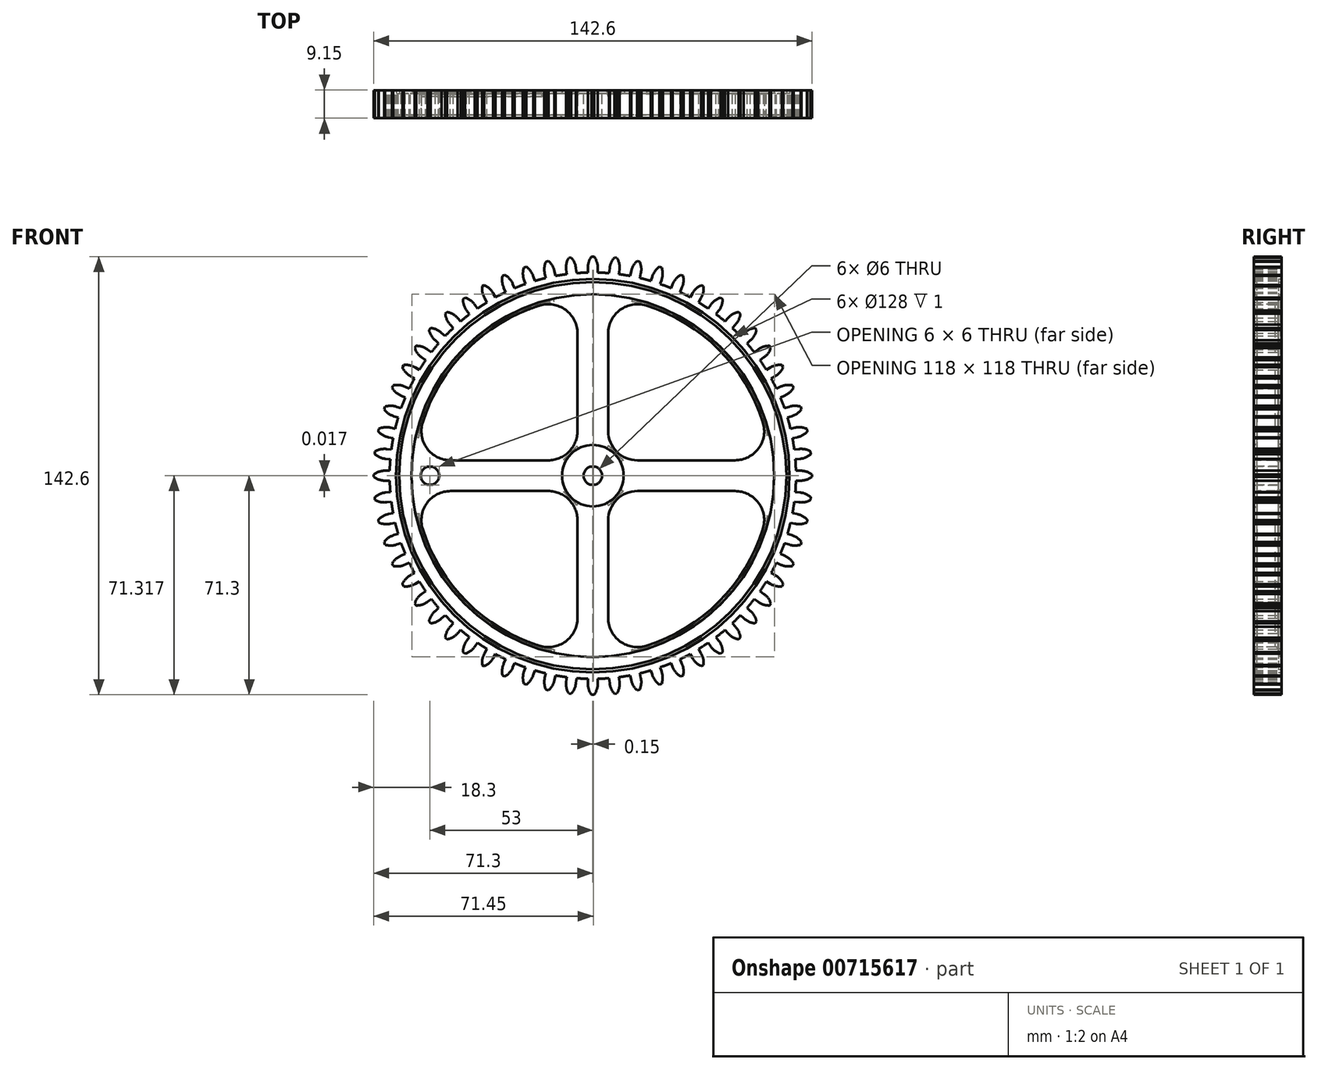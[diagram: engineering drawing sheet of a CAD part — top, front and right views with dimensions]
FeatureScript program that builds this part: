
annotation { "Feature Type Name" : "Feature", "Feature Type Description" : "" }
export const myFeature = defineFeature(function(context is Context, id is Id, definition is map)
    precondition{}
    {
        {
            var Q0;
            Q0=qCreatedBy(makeId("Front.planeOp"),FACE);
            var sketch = newSketch(context, id + "F0", { "sketchPlane" : qUnion([Q0])});
            skCircle(sketch, "E0", {"center": v(0, 0) * mm, "radius": 3 * mm});
            skCircle(sketch, "E1", {"center": v(0, 0) * mm, "radius": 66.1 * mm});
            skLineSegment(sketch, "E2", {"start": v(0, -77.77) * mm, "end": v(0, 74.62) * mm, "construction": true});
            skLineSegment(sketch, "E3", {"start": v(1.6, 66.08) * mm, "end": v(1.6, 67.83) * mm});
            skLineSegment(sketch, "E4", {"start": v(-1.6, 67.83) * mm, "end": v(-1.6, 66.08) * mm});
            skArc(sketch, "E5", {"start": v(-0.4, 71.3) * mm, "mid": v(-1.31, 69.54) * mm, "end": v(-1.6, 67.58) * mm});
            skArc(sketch, "E6.trimOffspring", {"start": v(1.6, 67.58) * mm, "mid": v(1.31, 69.54) * mm, "end": v(0.4, 71.3) * mm});
            skLineSegment(sketch, "E7", {"start": v(-0.4, 71.3) * mm, "end": v(0.4, 71.3) * mm});
            skLineSegment(sketch, "E8.1.0", {"start": v(-7.86, 70.87) * mm, "end": v(-7.05, 70.95) * mm});
            skArc(sketch, "E8.1.1", {"start": v(-5.47, 67.38) * mm, "mid": v(-5.96, 69.3) * mm, "end": v(-7.05, 70.95) * mm});
            skArc(sketch, "E8.1.2", {"start": v(-7.86, 70.87) * mm, "mid": v(-8.58, 69.02) * mm, "end": v(-8.66, 67.05) * mm});
            skLineSegment(sketch, "E8.1.3", {"start": v(-8.68, 67.3) * mm, "end": v(-8.5, 65.55) * mm});
            skLineSegment(sketch, "E8.1.4", {"start": v(-5.32, 65.89) * mm, "end": v(-5.5, 67.63) * mm});
            skLineSegment(sketch, "E8.2.0", {"start": v(-15.22, 69.66) * mm, "end": v(-14.43, 69.83) * mm});
            skArc(sketch, "E8.2.1", {"start": v(-12.49, 66.44) * mm, "mid": v(-13.17, 68.3) * mm, "end": v(-14.43, 69.83) * mm});
            skArc(sketch, "E8.2.2", {"start": v(-15.22, 69.66) * mm, "mid": v(-15.74, 67.75) * mm, "end": v(-15.62, 65.77) * mm});
            skLineSegment(sketch, "E8.2.3", {"start": v(-15.67, 66.02) * mm, "end": v(-15.3, 64.3) * mm});
            skLineSegment(sketch, "E8.2.4", {"start": v(-12.17, 64.97) * mm, "end": v(-12.54, 66.68) * mm});
            skLineSegment(sketch, "E9.1.3.0", {"start": v(-22.42, 67.68) * mm, "end": v(-21.64, 67.94) * mm});
            skArc(sketch, "E9.3.3.0", {"start": v(-19.36, 64.77) * mm, "mid": v(-20.24, 66.54) * mm, "end": v(-21.64, 67.94) * mm});
            skArc(sketch, "E9.7.3.0", {"start": v(-22.42, 67.68) * mm, "mid": v(-22.74, 65.73) * mm, "end": v(-22.4, 63.78) * mm});
            skLineSegment(sketch, "E9.11.3.0", {"start": v(-22.48, 64.02) * mm, "end": v(-21.94, 62.35) * mm});
            skLineSegment(sketch, "E9.14.3.0", {"start": v(-18.9, 63.34) * mm, "end": v(-19.44, 65) * mm});
            skLineSegment(sketch, "E9.1.4.0", {"start": v(-29.37, 64.97) * mm, "end": v(-28.63, 65.3) * mm});
            skArc(sketch, "E9.3.4.0", {"start": v(-26.03, 62.4) * mm, "mid": v(-27.08, 64.06) * mm, "end": v(-28.63, 65.3) * mm});
            skArc(sketch, "E9.7.4.0", {"start": v(-29.37, 64.97) * mm, "mid": v(-29.49, 63) * mm, "end": v(-28.95, 61.09) * mm});
            skLineSegment(sketch, "E9.11.4.0", {"start": v(-29.05, 61.32) * mm, "end": v(-28.34, 59.72) * mm});
            skLineSegment(sketch, "E9.14.4.0", {"start": v(-25.42, 61.02) * mm, "end": v(-26.13, 62.62) * mm});
            skLineSegment(sketch, "E9.1.5.0", {"start": v(-36, 61.54) * mm, "end": v(-35.3, 61.95) * mm});
            skArc(sketch, "E9.3.5.0", {"start": v(-32.4, 59.33) * mm, "mid": v(-33.63, 60.88) * mm, "end": v(-35.3, 61.95) * mm});
            skArc(sketch, "E9.7.5.0", {"start": v(-36, 61.54) * mm, "mid": v(-35.9, 59.57) * mm, "end": v(-35.18, 57.73) * mm});
            skLineSegment(sketch, "E9.11.5.0", {"start": v(-35.3, 57.94) * mm, "end": v(-34.43, 56.43) * mm});
            skLineSegment(sketch, "E9.14.5.0", {"start": v(-31.65, 58.03) * mm, "end": v(-32.53, 59.54) * mm});
            skLineSegment(sketch, "E9.1.6.0", {"start": v(-42.24, 57.44) * mm, "end": v(-41.58, 57.92) * mm});
            skArc(sketch, "E9.3.6.0", {"start": v(-38.43, 55.62) * mm, "mid": v(-39.81, 57.03) * mm, "end": v(-41.58, 57.92) * mm});
            skArc(sketch, "E9.7.6.0", {"start": v(-42.24, 57.44) * mm, "mid": v(-41.94, 55.49) * mm, "end": v(-41.02, 53.74) * mm});
            skLineSegment(sketch, "E9.11.6.0", {"start": v(-41.16, 53.94) * mm, "end": v(-40.14, 52.52) * mm});
            skLineSegment(sketch, "E9.14.6.0", {"start": v(-37.55, 54.4) * mm, "end": v(-38.58, 55.82) * mm});
            skLineSegment(sketch, "E9.1.7.0", {"start": v(-48.01, 52.71) * mm, "end": v(-47.4, 53.26) * mm});
            skArc(sketch, "E9.3.7.0", {"start": v(-44.03, 51.3) * mm, "mid": v(-45.56, 52.56) * mm, "end": v(-47.4, 53.26) * mm});
            skArc(sketch, "E9.7.7.0", {"start": v(-48.01, 52.71) * mm, "mid": v(-47.5, 50.8) * mm, "end": v(-46.41, 49.15) * mm});
            skLineSegment(sketch, "E9.11.7.0", {"start": v(-46.58, 49.34) * mm, "end": v(-45.4, 48.04) * mm});
            skLineSegment(sketch, "E9.14.7.0", {"start": v(-43.03, 50.18) * mm, "end": v(-44.2, 51.48) * mm});
            skLineSegment(sketch, "E9.1.8.0", {"start": v(-53.26, 47.4) * mm, "end": v(-52.71, 48.01) * mm});
            skArc(sketch, "E9.3.8.0", {"start": v(-49.15, 46.41) * mm, "mid": v(-50.8, 47.5) * mm, "end": v(-52.71, 48.01) * mm});
            skArc(sketch, "E9.7.8.0", {"start": v(-53.26, 47.4) * mm, "mid": v(-52.56, 45.56) * mm, "end": v(-51.3, 44.03) * mm});
            skLineSegment(sketch, "E9.11.8.0", {"start": v(-51.48, 44.2) * mm, "end": v(-50.18, 43.03) * mm});
            skLineSegment(sketch, "E9.14.8.0", {"start": v(-48.04, 45.4) * mm, "end": v(-49.34, 46.58) * mm});
            skLineSegment(sketch, "E9.1.9.0", {"start": v(-57.92, 41.58) * mm, "end": v(-57.44, 42.24) * mm});
            skArc(sketch, "E9.3.9.0", {"start": v(-53.74, 41.02) * mm, "mid": v(-55.49, 41.94) * mm, "end": v(-57.44, 42.24) * mm});
            skArc(sketch, "E9.7.9.0", {"start": v(-57.92, 41.58) * mm, "mid": v(-57.03, 39.81) * mm, "end": v(-55.62, 38.43) * mm});
            skLineSegment(sketch, "E9.11.9.0", {"start": v(-55.82, 38.58) * mm, "end": v(-54.4, 37.55) * mm});
            skLineSegment(sketch, "E9.14.9.0", {"start": v(-52.52, 40.14) * mm, "end": v(-53.94, 41.16) * mm});
            skLineSegment(sketch, "E9.1.10.0", {"start": v(-61.95, 35.3) * mm, "end": v(-61.54, 36) * mm});
            skArc(sketch, "E9.3.10.0", {"start": v(-57.73, 35.18) * mm, "mid": v(-59.57, 35.9) * mm, "end": v(-61.54, 36) * mm});
            skArc(sketch, "E9.7.10.0", {"start": v(-61.95, 35.3) * mm, "mid": v(-60.88, 33.63) * mm, "end": v(-59.33, 32.4) * mm});
            skLineSegment(sketch, "E9.11.10.0", {"start": v(-59.54, 32.53) * mm, "end": v(-58.03, 31.65) * mm});
            skLineSegment(sketch, "E9.14.10.0", {"start": v(-56.43, 34.43) * mm, "end": v(-57.94, 35.3) * mm});
            skLineSegment(sketch, "E9.1.11.0", {"start": v(-65.3, 28.63) * mm, "end": v(-64.97, 29.37) * mm});
            skArc(sketch, "E9.3.11.0", {"start": v(-61.09, 28.95) * mm, "mid": v(-63, 29.49) * mm, "end": v(-64.97, 29.37) * mm});
            skArc(sketch, "E9.7.11.0", {"start": v(-65.3, 28.63) * mm, "mid": v(-64.06, 27.08) * mm, "end": v(-62.4, 26.03) * mm});
            skLineSegment(sketch, "E9.11.11.0", {"start": v(-62.62, 26.13) * mm, "end": v(-61.02, 25.42) * mm});
            skLineSegment(sketch, "E9.14.11.0", {"start": v(-59.72, 28.34) * mm, "end": v(-61.32, 29.05) * mm});
            skLineSegment(sketch, "E9.1.12.0", {"start": v(-67.94, 21.64) * mm, "end": v(-67.68, 22.42) * mm});
            skArc(sketch, "E9.3.12.0", {"start": v(-63.78, 22.4) * mm, "mid": v(-65.73, 22.74) * mm, "end": v(-67.68, 22.42) * mm});
            skArc(sketch, "E9.7.12.0", {"start": v(-67.94, 21.64) * mm, "mid": v(-66.54, 20.24) * mm, "end": v(-64.77, 19.36) * mm});
            skLineSegment(sketch, "E9.11.12.0", {"start": v(-65, 19.44) * mm, "end": v(-63.34, 18.9) * mm});
            skLineSegment(sketch, "E9.14.12.0", {"start": v(-62.35, 21.94) * mm, "end": v(-64.02, 22.48) * mm});
            skLineSegment(sketch, "E9.1.13.0", {"start": v(-69.83, 14.43) * mm, "end": v(-69.66, 15.22) * mm});
            skArc(sketch, "E9.3.13.0", {"start": v(-65.77, 15.62) * mm, "mid": v(-67.75, 15.74) * mm, "end": v(-69.66, 15.22) * mm});
            skArc(sketch, "E9.7.13.0", {"start": v(-69.83, 14.43) * mm, "mid": v(-68.3, 13.17) * mm, "end": v(-66.44, 12.49) * mm});
            skLineSegment(sketch, "E9.11.13.0", {"start": v(-66.68, 12.54) * mm, "end": v(-64.97, 12.17) * mm});
            skLineSegment(sketch, "E9.14.13.0", {"start": v(-64.3, 15.3) * mm, "end": v(-66.02, 15.67) * mm});
            skLineSegment(sketch, "E9.1.14.0", {"start": v(-70.95, 7.05) * mm, "end": v(-70.87, 7.86) * mm});
            skArc(sketch, "E9.3.14.0", {"start": v(-67.05, 8.66) * mm, "mid": v(-69.02, 8.58) * mm, "end": v(-70.87, 7.86) * mm});
            skArc(sketch, "E9.7.14.0", {"start": v(-70.95, 7.05) * mm, "mid": v(-69.3, 5.96) * mm, "end": v(-67.38, 5.47) * mm});
            skLineSegment(sketch, "E9.11.14.0", {"start": v(-67.63, 5.5) * mm, "end": v(-65.89, 5.32) * mm});
            skLineSegment(sketch, "E9.14.14.0", {"start": v(-65.55, 8.5) * mm, "end": v(-67.3, 8.68) * mm});
            skLineSegment(sketch, "E9.1.15.0", {"start": v(-71.3, -0.4) * mm, "end": v(-71.3, 0.4) * mm});
            skArc(sketch, "E9.3.15.0", {"start": v(-67.58, 1.6) * mm, "mid": v(-69.54, 1.31) * mm, "end": v(-71.3, 0.4) * mm});
            skArc(sketch, "E9.7.15.0", {"start": v(-71.3, -0.4) * mm, "mid": v(-69.54, -1.31) * mm, "end": v(-67.58, -1.6) * mm});
            skLineSegment(sketch, "E9.11.15.0", {"start": v(-67.83, -1.6) * mm, "end": v(-66.08, -1.6) * mm});
            skLineSegment(sketch, "E9.14.15.0", {"start": v(-66.08, 1.6) * mm, "end": v(-67.83, 1.6) * mm});
            skLineSegment(sketch, "E9.1.16.0", {"start": v(-70.87, -7.86) * mm, "end": v(-70.95, -7.05) * mm});
            skArc(sketch, "E9.3.16.0", {"start": v(-67.38, -5.47) * mm, "mid": v(-69.3, -5.96) * mm, "end": v(-70.95, -7.05) * mm});
            skArc(sketch, "E9.7.16.0", {"start": v(-70.87, -7.86) * mm, "mid": v(-69.02, -8.58) * mm, "end": v(-67.05, -8.66) * mm});
            skLineSegment(sketch, "E9.11.16.0", {"start": v(-67.3, -8.68) * mm, "end": v(-65.55, -8.5) * mm});
            skLineSegment(sketch, "E9.14.16.0", {"start": v(-65.89, -5.32) * mm, "end": v(-67.63, -5.5) * mm});
            skLineSegment(sketch, "E9.1.17.0", {"start": v(-69.66, -15.22) * mm, "end": v(-69.83, -14.43) * mm});
            skArc(sketch, "E9.3.17.0", {"start": v(-66.44, -12.49) * mm, "mid": v(-68.3, -13.17) * mm, "end": v(-69.83, -14.43) * mm});
            skArc(sketch, "E9.7.17.0", {"start": v(-69.66, -15.22) * mm, "mid": v(-67.75, -15.74) * mm, "end": v(-65.77, -15.62) * mm});
            skLineSegment(sketch, "E9.11.17.0", {"start": v(-66.02, -15.67) * mm, "end": v(-64.3, -15.3) * mm});
            skLineSegment(sketch, "E9.14.17.0", {"start": v(-64.97, -12.17) * mm, "end": v(-66.68, -12.54) * mm});
            skLineSegment(sketch, "E9.1.18.0", {"start": v(-67.68, -22.42) * mm, "end": v(-67.94, -21.64) * mm});
            skArc(sketch, "E9.3.18.0", {"start": v(-64.77, -19.36) * mm, "mid": v(-66.54, -20.24) * mm, "end": v(-67.94, -21.64) * mm});
            skArc(sketch, "E9.7.18.0", {"start": v(-67.68, -22.42) * mm, "mid": v(-65.73, -22.74) * mm, "end": v(-63.78, -22.4) * mm});
            skLineSegment(sketch, "E9.11.18.0", {"start": v(-64.02, -22.48) * mm, "end": v(-62.35, -21.94) * mm});
            skLineSegment(sketch, "E9.14.18.0", {"start": v(-63.34, -18.9) * mm, "end": v(-65, -19.44) * mm});
            skLineSegment(sketch, "E9.1.19.0", {"start": v(-64.97, -29.37) * mm, "end": v(-65.3, -28.63) * mm});
            skArc(sketch, "E9.3.19.0", {"start": v(-62.4, -26.03) * mm, "mid": v(-64.06, -27.08) * mm, "end": v(-65.3, -28.63) * mm});
            skArc(sketch, "E9.7.19.0", {"start": v(-64.97, -29.37) * mm, "mid": v(-63, -29.49) * mm, "end": v(-61.09, -28.95) * mm});
            skLineSegment(sketch, "E9.11.19.0", {"start": v(-61.32, -29.05) * mm, "end": v(-59.72, -28.34) * mm});
            skLineSegment(sketch, "E9.14.19.0", {"start": v(-61.02, -25.42) * mm, "end": v(-62.62, -26.13) * mm});
            skLineSegment(sketch, "E9.1.20.0", {"start": v(-61.54, -36) * mm, "end": v(-61.95, -35.3) * mm});
            skArc(sketch, "E9.3.20.0", {"start": v(-59.33, -32.4) * mm, "mid": v(-60.88, -33.63) * mm, "end": v(-61.95, -35.3) * mm});
            skArc(sketch, "E9.7.20.0", {"start": v(-61.54, -36) * mm, "mid": v(-59.57, -35.9) * mm, "end": v(-57.73, -35.18) * mm});
            skLineSegment(sketch, "E9.11.20.0", {"start": v(-57.94, -35.3) * mm, "end": v(-56.43, -34.43) * mm});
            skLineSegment(sketch, "E9.14.20.0", {"start": v(-58.03, -31.65) * mm, "end": v(-59.54, -32.53) * mm});
            skLineSegment(sketch, "E9.1.21.0", {"start": v(-57.44, -42.24) * mm, "end": v(-57.92, -41.58) * mm});
            skArc(sketch, "E9.3.21.0", {"start": v(-55.62, -38.43) * mm, "mid": v(-57.03, -39.81) * mm, "end": v(-57.92, -41.58) * mm});
            skArc(sketch, "E9.7.21.0", {"start": v(-57.44, -42.24) * mm, "mid": v(-55.49, -41.94) * mm, "end": v(-53.74, -41.02) * mm});
            skLineSegment(sketch, "E9.11.21.0", {"start": v(-53.94, -41.16) * mm, "end": v(-52.52, -40.14) * mm});
            skLineSegment(sketch, "E9.14.21.0", {"start": v(-54.4, -37.55) * mm, "end": v(-55.82, -38.58) * mm});
            skLineSegment(sketch, "E9.1.22.0", {"start": v(-52.71, -48.01) * mm, "end": v(-53.26, -47.4) * mm});
            skArc(sketch, "E9.3.22.0", {"start": v(-51.3, -44.03) * mm, "mid": v(-52.56, -45.56) * mm, "end": v(-53.26, -47.4) * mm});
            skArc(sketch, "E9.7.22.0", {"start": v(-52.71, -48.01) * mm, "mid": v(-50.8, -47.5) * mm, "end": v(-49.15, -46.41) * mm});
            skLineSegment(sketch, "E9.11.22.0", {"start": v(-49.34, -46.58) * mm, "end": v(-48.04, -45.4) * mm});
            skLineSegment(sketch, "E9.14.22.0", {"start": v(-50.18, -43.03) * mm, "end": v(-51.48, -44.2) * mm});
            skLineSegment(sketch, "E9.1.23.0", {"start": v(-47.4, -53.26) * mm, "end": v(-48.01, -52.71) * mm});
            skArc(sketch, "E9.3.23.0", {"start": v(-46.41, -49.15) * mm, "mid": v(-47.5, -50.8) * mm, "end": v(-48.01, -52.71) * mm});
            skArc(sketch, "E9.7.23.0", {"start": v(-47.4, -53.26) * mm, "mid": v(-45.56, -52.56) * mm, "end": v(-44.03, -51.3) * mm});
            skLineSegment(sketch, "E9.11.23.0", {"start": v(-44.2, -51.48) * mm, "end": v(-43.03, -50.18) * mm});
            skLineSegment(sketch, "E9.14.23.0", {"start": v(-45.4, -48.04) * mm, "end": v(-46.58, -49.34) * mm});
            skLineSegment(sketch, "E9.1.24.0", {"start": v(-41.58, -57.92) * mm, "end": v(-42.24, -57.44) * mm});
            skArc(sketch, "E9.3.24.0", {"start": v(-41.02, -53.74) * mm, "mid": v(-41.94, -55.49) * mm, "end": v(-42.24, -57.44) * mm});
            skArc(sketch, "E9.7.24.0", {"start": v(-41.58, -57.92) * mm, "mid": v(-39.81, -57.03) * mm, "end": v(-38.43, -55.62) * mm});
            skLineSegment(sketch, "E9.11.24.0", {"start": v(-38.58, -55.82) * mm, "end": v(-37.55, -54.4) * mm});
            skLineSegment(sketch, "E9.14.24.0", {"start": v(-40.14, -52.52) * mm, "end": v(-41.16, -53.94) * mm});
            skLineSegment(sketch, "E9.1.25.0", {"start": v(-35.3, -61.95) * mm, "end": v(-36, -61.54) * mm});
            skArc(sketch, "E9.3.25.0", {"start": v(-35.18, -57.73) * mm, "mid": v(-35.9, -59.57) * mm, "end": v(-36, -61.54) * mm});
            skArc(sketch, "E9.7.25.0", {"start": v(-35.3, -61.95) * mm, "mid": v(-33.63, -60.88) * mm, "end": v(-32.4, -59.33) * mm});
            skLineSegment(sketch, "E9.11.25.0", {"start": v(-32.53, -59.54) * mm, "end": v(-31.65, -58.03) * mm});
            skLineSegment(sketch, "E9.14.25.0", {"start": v(-34.43, -56.43) * mm, "end": v(-35.3, -57.94) * mm});
            skLineSegment(sketch, "E9.1.26.0", {"start": v(-28.63, -65.3) * mm, "end": v(-29.37, -64.97) * mm});
            skArc(sketch, "E9.3.26.0", {"start": v(-28.95, -61.09) * mm, "mid": v(-29.49, -63) * mm, "end": v(-29.37, -64.97) * mm});
            skArc(sketch, "E9.7.26.0", {"start": v(-28.63, -65.3) * mm, "mid": v(-27.08, -64.06) * mm, "end": v(-26.03, -62.4) * mm});
            skLineSegment(sketch, "E9.11.26.0", {"start": v(-26.13, -62.62) * mm, "end": v(-25.42, -61.02) * mm});
            skLineSegment(sketch, "E9.14.26.0", {"start": v(-28.34, -59.72) * mm, "end": v(-29.05, -61.32) * mm});
            skLineSegment(sketch, "E9.1.27.0", {"start": v(-21.64, -67.94) * mm, "end": v(-22.42, -67.68) * mm});
            skArc(sketch, "E9.3.27.0", {"start": v(-22.4, -63.78) * mm, "mid": v(-22.74, -65.73) * mm, "end": v(-22.42, -67.68) * mm});
            skArc(sketch, "E9.7.27.0", {"start": v(-21.64, -67.94) * mm, "mid": v(-20.24, -66.54) * mm, "end": v(-19.36, -64.77) * mm});
            skLineSegment(sketch, "E9.11.27.0", {"start": v(-19.44, -65) * mm, "end": v(-18.9, -63.34) * mm});
            skLineSegment(sketch, "E9.14.27.0", {"start": v(-21.94, -62.35) * mm, "end": v(-22.48, -64.02) * mm});
            skLineSegment(sketch, "E9.1.28.0", {"start": v(-14.43, -69.83) * mm, "end": v(-15.22, -69.66) * mm});
            skArc(sketch, "E9.3.28.0", {"start": v(-15.62, -65.77) * mm, "mid": v(-15.74, -67.75) * mm, "end": v(-15.22, -69.66) * mm});
            skArc(sketch, "E9.7.28.0", {"start": v(-14.43, -69.83) * mm, "mid": v(-13.17, -68.3) * mm, "end": v(-12.49, -66.44) * mm});
            skLineSegment(sketch, "E9.11.28.0", {"start": v(-12.54, -66.68) * mm, "end": v(-12.17, -64.97) * mm});
            skLineSegment(sketch, "E9.14.28.0", {"start": v(-15.3, -64.3) * mm, "end": v(-15.67, -66.02) * mm});
            skLineSegment(sketch, "E9.1.29.0", {"start": v(-7.05, -70.95) * mm, "end": v(-7.86, -70.87) * mm});
            skArc(sketch, "E9.3.29.0", {"start": v(-8.66, -67.05) * mm, "mid": v(-8.58, -69.02) * mm, "end": v(-7.86, -70.87) * mm});
            skArc(sketch, "E9.7.29.0", {"start": v(-7.05, -70.95) * mm, "mid": v(-5.96, -69.3) * mm, "end": v(-5.47, -67.38) * mm});
            skLineSegment(sketch, "E9.11.29.0", {"start": v(-5.5, -67.63) * mm, "end": v(-5.32, -65.89) * mm});
            skLineSegment(sketch, "E9.14.29.0", {"start": v(-8.5, -65.55) * mm, "end": v(-8.68, -67.3) * mm});
            skLineSegment(sketch, "E9.1.30.0", {"start": v(0.4, -71.3) * mm, "end": v(-0.4, -71.3) * mm});
            skArc(sketch, "E9.3.30.0", {"start": v(-1.6, -67.58) * mm, "mid": v(-1.31, -69.54) * mm, "end": v(-0.4, -71.3) * mm});
            skArc(sketch, "E9.7.30.0", {"start": v(0.4, -71.3) * mm, "mid": v(1.31, -69.54) * mm, "end": v(1.6, -67.58) * mm});
            skLineSegment(sketch, "E9.11.30.0", {"start": v(1.6, -67.83) * mm, "end": v(1.6, -66.08) * mm});
            skLineSegment(sketch, "E9.14.30.0", {"start": v(-1.6, -66.08) * mm, "end": v(-1.6, -67.83) * mm});
            skLineSegment(sketch, "E9.1.31.0", {"start": v(7.86, -70.87) * mm, "end": v(7.05, -70.95) * mm});
            skArc(sketch, "E9.3.31.0", {"start": v(5.47, -67.38) * mm, "mid": v(5.96, -69.3) * mm, "end": v(7.05, -70.95) * mm});
            skArc(sketch, "E9.7.31.0", {"start": v(7.86, -70.87) * mm, "mid": v(8.58, -69.02) * mm, "end": v(8.66, -67.05) * mm});
            skLineSegment(sketch, "E9.11.31.0", {"start": v(8.68, -67.3) * mm, "end": v(8.5, -65.55) * mm});
            skLineSegment(sketch, "E9.14.31.0", {"start": v(5.32, -65.89) * mm, "end": v(5.5, -67.63) * mm});
            skLineSegment(sketch, "E9.1.32.0", {"start": v(15.22, -69.66) * mm, "end": v(14.43, -69.83) * mm});
            skArc(sketch, "E9.3.32.0", {"start": v(12.49, -66.44) * mm, "mid": v(13.17, -68.3) * mm, "end": v(14.43, -69.83) * mm});
            skArc(sketch, "E9.7.32.0", {"start": v(15.22, -69.66) * mm, "mid": v(15.74, -67.75) * mm, "end": v(15.62, -65.77) * mm});
            skLineSegment(sketch, "E9.11.32.0", {"start": v(15.67, -66.02) * mm, "end": v(15.3, -64.3) * mm});
            skLineSegment(sketch, "E9.14.32.0", {"start": v(12.17, -64.97) * mm, "end": v(12.54, -66.68) * mm});
            skLineSegment(sketch, "E9.1.33.0", {"start": v(22.42, -67.68) * mm, "end": v(21.64, -67.94) * mm});
            skArc(sketch, "E9.3.33.0", {"start": v(19.36, -64.77) * mm, "mid": v(20.24, -66.54) * mm, "end": v(21.64, -67.94) * mm});
            skArc(sketch, "E9.7.33.0", {"start": v(22.42, -67.68) * mm, "mid": v(22.74, -65.73) * mm, "end": v(22.4, -63.78) * mm});
            skLineSegment(sketch, "E9.11.33.0", {"start": v(22.48, -64.02) * mm, "end": v(21.94, -62.35) * mm});
            skLineSegment(sketch, "E9.14.33.0", {"start": v(18.9, -63.34) * mm, "end": v(19.44, -65) * mm});
            skLineSegment(sketch, "E9.1.34.0", {"start": v(29.37, -64.97) * mm, "end": v(28.63, -65.3) * mm});
            skArc(sketch, "E9.3.34.0", {"start": v(26.03, -62.4) * mm, "mid": v(27.08, -64.06) * mm, "end": v(28.63, -65.3) * mm});
            skArc(sketch, "E9.7.34.0", {"start": v(29.37, -64.97) * mm, "mid": v(29.49, -63) * mm, "end": v(28.95, -61.09) * mm});
            skLineSegment(sketch, "E9.11.34.0", {"start": v(29.05, -61.32) * mm, "end": v(28.34, -59.72) * mm});
            skLineSegment(sketch, "E9.14.34.0", {"start": v(25.42, -61.02) * mm, "end": v(26.13, -62.62) * mm});
            skLineSegment(sketch, "E9.1.35.0", {"start": v(36, -61.54) * mm, "end": v(35.3, -61.95) * mm});
            skArc(sketch, "E9.3.35.0", {"start": v(32.4, -59.33) * mm, "mid": v(33.63, -60.88) * mm, "end": v(35.3, -61.95) * mm});
            skArc(sketch, "E9.7.35.0", {"start": v(36, -61.54) * mm, "mid": v(35.9, -59.57) * mm, "end": v(35.18, -57.73) * mm});
            skLineSegment(sketch, "E9.11.35.0", {"start": v(35.3, -57.94) * mm, "end": v(34.43, -56.43) * mm});
            skLineSegment(sketch, "E9.14.35.0", {"start": v(31.65, -58.03) * mm, "end": v(32.53, -59.54) * mm});
            skLineSegment(sketch, "E9.1.36.0", {"start": v(42.24, -57.44) * mm, "end": v(41.58, -57.92) * mm});
            skArc(sketch, "E9.3.36.0", {"start": v(38.43, -55.62) * mm, "mid": v(39.81, -57.03) * mm, "end": v(41.58, -57.92) * mm});
            skArc(sketch, "E9.7.36.0", {"start": v(42.24, -57.44) * mm, "mid": v(41.94, -55.49) * mm, "end": v(41.02, -53.74) * mm});
            skLineSegment(sketch, "E9.11.36.0", {"start": v(41.16, -53.94) * mm, "end": v(40.14, -52.52) * mm});
            skLineSegment(sketch, "E9.14.36.0", {"start": v(37.55, -54.4) * mm, "end": v(38.58, -55.82) * mm});
            skLineSegment(sketch, "E9.1.37.0", {"start": v(48.01, -52.71) * mm, "end": v(47.4, -53.26) * mm});
            skArc(sketch, "E9.3.37.0", {"start": v(44.03, -51.3) * mm, "mid": v(45.56, -52.56) * mm, "end": v(47.4, -53.26) * mm});
            skArc(sketch, "E9.7.37.0", {"start": v(48.01, -52.71) * mm, "mid": v(47.5, -50.8) * mm, "end": v(46.41, -49.15) * mm});
            skLineSegment(sketch, "E9.11.37.0", {"start": v(46.58, -49.34) * mm, "end": v(45.4, -48.04) * mm});
            skLineSegment(sketch, "E9.14.37.0", {"start": v(43.03, -50.18) * mm, "end": v(44.2, -51.48) * mm});
            skLineSegment(sketch, "E9.1.38.0", {"start": v(53.26, -47.4) * mm, "end": v(52.71, -48.01) * mm});
            skArc(sketch, "E9.3.38.0", {"start": v(49.15, -46.41) * mm, "mid": v(50.8, -47.5) * mm, "end": v(52.71, -48.01) * mm});
            skArc(sketch, "E9.7.38.0", {"start": v(53.26, -47.4) * mm, "mid": v(52.56, -45.56) * mm, "end": v(51.3, -44.03) * mm});
            skLineSegment(sketch, "E9.11.38.0", {"start": v(51.48, -44.2) * mm, "end": v(50.18, -43.03) * mm});
            skLineSegment(sketch, "E9.14.38.0", {"start": v(48.04, -45.4) * mm, "end": v(49.34, -46.58) * mm});
            skLineSegment(sketch, "E9.1.39.0", {"start": v(57.92, -41.58) * mm, "end": v(57.44, -42.24) * mm});
            skArc(sketch, "E9.3.39.0", {"start": v(53.74, -41.02) * mm, "mid": v(55.49, -41.94) * mm, "end": v(57.44, -42.24) * mm});
            skArc(sketch, "E9.7.39.0", {"start": v(57.92, -41.58) * mm, "mid": v(57.03, -39.81) * mm, "end": v(55.62, -38.43) * mm});
            skLineSegment(sketch, "E9.11.39.0", {"start": v(55.82, -38.58) * mm, "end": v(54.4, -37.55) * mm});
            skLineSegment(sketch, "E9.14.39.0", {"start": v(52.52, -40.14) * mm, "end": v(53.94, -41.16) * mm});
            skLineSegment(sketch, "E9.1.40.0", {"start": v(61.95, -35.3) * mm, "end": v(61.54, -36) * mm});
            skArc(sketch, "E9.3.40.0", {"start": v(57.73, -35.18) * mm, "mid": v(59.57, -35.9) * mm, "end": v(61.54, -36) * mm});
            skArc(sketch, "E9.7.40.0", {"start": v(61.95, -35.3) * mm, "mid": v(60.88, -33.63) * mm, "end": v(59.33, -32.4) * mm});
            skLineSegment(sketch, "E9.11.40.0", {"start": v(59.54, -32.53) * mm, "end": v(58.03, -31.65) * mm});
            skLineSegment(sketch, "E9.14.40.0", {"start": v(56.43, -34.43) * mm, "end": v(57.94, -35.3) * mm});
            skLineSegment(sketch, "E9.1.41.0", {"start": v(65.3, -28.63) * mm, "end": v(64.97, -29.37) * mm});
            skArc(sketch, "E9.3.41.0", {"start": v(61.09, -28.95) * mm, "mid": v(63, -29.49) * mm, "end": v(64.97, -29.37) * mm});
            skArc(sketch, "E9.7.41.0", {"start": v(65.3, -28.63) * mm, "mid": v(64.06, -27.08) * mm, "end": v(62.4, -26.03) * mm});
            skLineSegment(sketch, "E9.11.41.0", {"start": v(62.62, -26.13) * mm, "end": v(61.02, -25.42) * mm});
            skLineSegment(sketch, "E9.14.41.0", {"start": v(59.72, -28.34) * mm, "end": v(61.32, -29.05) * mm});
            skLineSegment(sketch, "E9.1.42.0", {"start": v(67.94, -21.64) * mm, "end": v(67.68, -22.42) * mm});
            skArc(sketch, "E9.3.42.0", {"start": v(63.78, -22.4) * mm, "mid": v(65.73, -22.74) * mm, "end": v(67.68, -22.42) * mm});
            skArc(sketch, "E9.7.42.0", {"start": v(67.94, -21.64) * mm, "mid": v(66.54, -20.24) * mm, "end": v(64.77, -19.36) * mm});
            skLineSegment(sketch, "E9.11.42.0", {"start": v(65, -19.44) * mm, "end": v(63.34, -18.9) * mm});
            skLineSegment(sketch, "E9.14.42.0", {"start": v(62.35, -21.94) * mm, "end": v(64.02, -22.48) * mm});
            skLineSegment(sketch, "E9.1.43.0", {"start": v(69.83, -14.43) * mm, "end": v(69.66, -15.22) * mm});
            skArc(sketch, "E9.3.43.0", {"start": v(65.77, -15.62) * mm, "mid": v(67.75, -15.74) * mm, "end": v(69.66, -15.22) * mm});
            skArc(sketch, "E9.7.43.0", {"start": v(69.83, -14.43) * mm, "mid": v(68.3, -13.17) * mm, "end": v(66.44, -12.49) * mm});
            skLineSegment(sketch, "E9.11.43.0", {"start": v(66.68, -12.54) * mm, "end": v(64.97, -12.17) * mm});
            skLineSegment(sketch, "E9.14.43.0", {"start": v(64.3, -15.3) * mm, "end": v(66.02, -15.67) * mm});
            skLineSegment(sketch, "E9.1.44.0", {"start": v(70.95, -7.05) * mm, "end": v(70.87, -7.86) * mm});
            skArc(sketch, "E9.3.44.0", {"start": v(67.05, -8.66) * mm, "mid": v(69.02, -8.58) * mm, "end": v(70.87, -7.86) * mm});
            skArc(sketch, "E9.7.44.0", {"start": v(70.95, -7.05) * mm, "mid": v(69.3, -5.96) * mm, "end": v(67.38, -5.47) * mm});
            skLineSegment(sketch, "E9.11.44.0", {"start": v(67.63, -5.5) * mm, "end": v(65.89, -5.32) * mm});
            skLineSegment(sketch, "E9.14.44.0", {"start": v(65.55, -8.5) * mm, "end": v(67.3, -8.68) * mm});
            skLineSegment(sketch, "E9.1.45.0", {"start": v(71.3, 0.4) * mm, "end": v(71.3, -0.4) * mm});
            skArc(sketch, "E9.3.45.0", {"start": v(67.58, -1.6) * mm, "mid": v(69.54, -1.31) * mm, "end": v(71.3, -0.4) * mm});
            skArc(sketch, "E9.7.45.0", {"start": v(71.3, 0.4) * mm, "mid": v(69.54, 1.31) * mm, "end": v(67.58, 1.6) * mm});
            skLineSegment(sketch, "E9.11.45.0", {"start": v(67.83, 1.6) * mm, "end": v(66.08, 1.6) * mm});
            skLineSegment(sketch, "E9.14.45.0", {"start": v(66.08, -1.6) * mm, "end": v(67.83, -1.6) * mm});
            skLineSegment(sketch, "E9.1.46.0", {"start": v(70.87, 7.86) * mm, "end": v(70.95, 7.05) * mm});
            skArc(sketch, "E9.3.46.0", {"start": v(67.38, 5.47) * mm, "mid": v(69.3, 5.96) * mm, "end": v(70.95, 7.05) * mm});
            skArc(sketch, "E9.7.46.0", {"start": v(70.87, 7.86) * mm, "mid": v(69.02, 8.58) * mm, "end": v(67.05, 8.66) * mm});
            skLineSegment(sketch, "E9.11.46.0", {"start": v(67.3, 8.68) * mm, "end": v(65.55, 8.5) * mm});
            skLineSegment(sketch, "E9.14.46.0", {"start": v(65.89, 5.32) * mm, "end": v(67.63, 5.5) * mm});
            skLineSegment(sketch, "E9.1.47.0", {"start": v(69.66, 15.22) * mm, "end": v(69.83, 14.43) * mm});
            skArc(sketch, "E9.3.47.0", {"start": v(66.44, 12.49) * mm, "mid": v(68.3, 13.17) * mm, "end": v(69.83, 14.43) * mm});
            skArc(sketch, "E9.7.47.0", {"start": v(69.66, 15.22) * mm, "mid": v(67.75, 15.74) * mm, "end": v(65.77, 15.62) * mm});
            skLineSegment(sketch, "E9.11.47.0", {"start": v(66.02, 15.67) * mm, "end": v(64.3, 15.3) * mm});
            skLineSegment(sketch, "E9.14.47.0", {"start": v(64.97, 12.17) * mm, "end": v(66.68, 12.54) * mm});
            skLineSegment(sketch, "E9.1.48.0", {"start": v(67.68, 22.42) * mm, "end": v(67.94, 21.64) * mm});
            skArc(sketch, "E9.3.48.0", {"start": v(64.77, 19.36) * mm, "mid": v(66.54, 20.24) * mm, "end": v(67.94, 21.64) * mm});
            skArc(sketch, "E9.7.48.0", {"start": v(67.68, 22.42) * mm, "mid": v(65.73, 22.74) * mm, "end": v(63.78, 22.4) * mm});
            skLineSegment(sketch, "E9.11.48.0", {"start": v(64.02, 22.48) * mm, "end": v(62.35, 21.94) * mm});
            skLineSegment(sketch, "E9.14.48.0", {"start": v(63.34, 18.9) * mm, "end": v(65, 19.44) * mm});
            skLineSegment(sketch, "E9.1.49.0", {"start": v(64.97, 29.37) * mm, "end": v(65.3, 28.63) * mm});
            skArc(sketch, "E9.3.49.0", {"start": v(62.4, 26.03) * mm, "mid": v(64.06, 27.08) * mm, "end": v(65.3, 28.63) * mm});
            skArc(sketch, "E9.7.49.0", {"start": v(64.97, 29.37) * mm, "mid": v(63, 29.49) * mm, "end": v(61.09, 28.95) * mm});
            skLineSegment(sketch, "E9.11.49.0", {"start": v(61.32, 29.05) * mm, "end": v(59.72, 28.34) * mm});
            skLineSegment(sketch, "E9.14.49.0", {"start": v(61.02, 25.42) * mm, "end": v(62.62, 26.13) * mm});
            skLineSegment(sketch, "E9.1.50.0", {"start": v(61.54, 36) * mm, "end": v(61.95, 35.3) * mm});
            skArc(sketch, "E9.3.50.0", {"start": v(59.33, 32.4) * mm, "mid": v(60.88, 33.63) * mm, "end": v(61.95, 35.3) * mm});
            skArc(sketch, "E9.7.50.0", {"start": v(61.54, 36) * mm, "mid": v(59.57, 35.9) * mm, "end": v(57.73, 35.18) * mm});
            skLineSegment(sketch, "E9.11.50.0", {"start": v(57.94, 35.3) * mm, "end": v(56.43, 34.43) * mm});
            skLineSegment(sketch, "E9.14.50.0", {"start": v(58.03, 31.65) * mm, "end": v(59.54, 32.53) * mm});
            skLineSegment(sketch, "E9.1.51.0", {"start": v(57.44, 42.24) * mm, "end": v(57.92, 41.58) * mm});
            skArc(sketch, "E9.3.51.0", {"start": v(55.62, 38.43) * mm, "mid": v(57.03, 39.81) * mm, "end": v(57.92, 41.58) * mm});
            skArc(sketch, "E9.7.51.0", {"start": v(57.44, 42.24) * mm, "mid": v(55.49, 41.94) * mm, "end": v(53.74, 41.02) * mm});
            skLineSegment(sketch, "E9.11.51.0", {"start": v(53.94, 41.16) * mm, "end": v(52.52, 40.14) * mm});
            skLineSegment(sketch, "E9.14.51.0", {"start": v(54.4, 37.55) * mm, "end": v(55.82, 38.58) * mm});
            skLineSegment(sketch, "E9.1.52.0", {"start": v(52.71, 48.01) * mm, "end": v(53.26, 47.4) * mm});
            skArc(sketch, "E9.3.52.0", {"start": v(51.3, 44.03) * mm, "mid": v(52.56, 45.56) * mm, "end": v(53.26, 47.4) * mm});
            skArc(sketch, "E9.7.52.0", {"start": v(52.71, 48.01) * mm, "mid": v(50.8, 47.5) * mm, "end": v(49.15, 46.41) * mm});
            skLineSegment(sketch, "E9.11.52.0", {"start": v(49.34, 46.58) * mm, "end": v(48.04, 45.4) * mm});
            skLineSegment(sketch, "E9.14.52.0", {"start": v(50.18, 43.03) * mm, "end": v(51.48, 44.2) * mm});
            skLineSegment(sketch, "E9.1.53.0", {"start": v(47.4, 53.26) * mm, "end": v(48.01, 52.71) * mm});
            skArc(sketch, "E9.3.53.0", {"start": v(46.41, 49.15) * mm, "mid": v(47.5, 50.8) * mm, "end": v(48.01, 52.71) * mm});
            skArc(sketch, "E9.7.53.0", {"start": v(47.4, 53.26) * mm, "mid": v(45.56, 52.56) * mm, "end": v(44.03, 51.3) * mm});
            skLineSegment(sketch, "E9.11.53.0", {"start": v(44.2, 51.48) * mm, "end": v(43.03, 50.18) * mm});
            skLineSegment(sketch, "E9.14.53.0", {"start": v(45.4, 48.04) * mm, "end": v(46.58, 49.34) * mm});
            skLineSegment(sketch, "E9.1.54.0", {"start": v(41.58, 57.92) * mm, "end": v(42.24, 57.44) * mm});
            skArc(sketch, "E9.3.54.0", {"start": v(41.02, 53.74) * mm, "mid": v(41.94, 55.49) * mm, "end": v(42.24, 57.44) * mm});
            skArc(sketch, "E9.7.54.0", {"start": v(41.58, 57.92) * mm, "mid": v(39.81, 57.03) * mm, "end": v(38.43, 55.62) * mm});
            skLineSegment(sketch, "E9.11.54.0", {"start": v(38.58, 55.82) * mm, "end": v(37.55, 54.4) * mm});
            skLineSegment(sketch, "E9.14.54.0", {"start": v(40.14, 52.52) * mm, "end": v(41.16, 53.94) * mm});
            skLineSegment(sketch, "E9.1.55.0", {"start": v(35.3, 61.95) * mm, "end": v(36, 61.54) * mm});
            skArc(sketch, "E9.3.55.0", {"start": v(35.18, 57.73) * mm, "mid": v(35.9, 59.57) * mm, "end": v(36, 61.54) * mm});
            skArc(sketch, "E9.7.55.0", {"start": v(35.3, 61.95) * mm, "mid": v(33.63, 60.88) * mm, "end": v(32.4, 59.33) * mm});
            skLineSegment(sketch, "E9.11.55.0", {"start": v(32.53, 59.54) * mm, "end": v(31.65, 58.03) * mm});
            skLineSegment(sketch, "E9.14.55.0", {"start": v(34.43, 56.43) * mm, "end": v(35.3, 57.94) * mm});
            skLineSegment(sketch, "E9.1.56.0", {"start": v(28.63, 65.3) * mm, "end": v(29.37, 64.97) * mm});
            skArc(sketch, "E9.3.56.0", {"start": v(28.95, 61.09) * mm, "mid": v(29.49, 63) * mm, "end": v(29.37, 64.97) * mm});
            skArc(sketch, "E9.7.56.0", {"start": v(28.63, 65.3) * mm, "mid": v(27.08, 64.06) * mm, "end": v(26.03, 62.4) * mm});
            skLineSegment(sketch, "E9.11.56.0", {"start": v(26.13, 62.62) * mm, "end": v(25.42, 61.02) * mm});
            skLineSegment(sketch, "E9.14.56.0", {"start": v(28.34, 59.72) * mm, "end": v(29.05, 61.32) * mm});
            skLineSegment(sketch, "E9.1.57.0", {"start": v(21.64, 67.94) * mm, "end": v(22.42, 67.68) * mm});
            skArc(sketch, "E9.3.57.0", {"start": v(22.4, 63.78) * mm, "mid": v(22.74, 65.73) * mm, "end": v(22.42, 67.68) * mm});
            skArc(sketch, "E9.7.57.0", {"start": v(21.64, 67.94) * mm, "mid": v(20.24, 66.54) * mm, "end": v(19.36, 64.77) * mm});
            skLineSegment(sketch, "E9.11.57.0", {"start": v(19.44, 65) * mm, "end": v(18.9, 63.34) * mm});
            skLineSegment(sketch, "E9.14.57.0", {"start": v(21.94, 62.35) * mm, "end": v(22.48, 64.02) * mm});
            skLineSegment(sketch, "E9.1.58.0", {"start": v(14.43, 69.83) * mm, "end": v(15.22, 69.66) * mm});
            skArc(sketch, "E9.3.58.0", {"start": v(15.62, 65.77) * mm, "mid": v(15.74, 67.75) * mm, "end": v(15.22, 69.66) * mm});
            skArc(sketch, "E9.7.58.0", {"start": v(14.43, 69.83) * mm, "mid": v(13.17, 68.3) * mm, "end": v(12.49, 66.44) * mm});
            skLineSegment(sketch, "E9.11.58.0", {"start": v(12.54, 66.68) * mm, "end": v(12.17, 64.97) * mm});
            skLineSegment(sketch, "E9.14.58.0", {"start": v(15.3, 64.3) * mm, "end": v(15.67, 66.02) * mm});
            skLineSegment(sketch, "E9.1.59.0", {"start": v(7.05, 70.95) * mm, "end": v(7.86, 70.87) * mm});
            skArc(sketch, "E9.3.59.0", {"start": v(8.66, 67.05) * mm, "mid": v(8.58, 69.02) * mm, "end": v(7.86, 70.87) * mm});
            skArc(sketch, "E9.7.59.0", {"start": v(7.05, 70.95) * mm, "mid": v(5.96, 69.3) * mm, "end": v(5.47, 67.38) * mm});
            skLineSegment(sketch, "E9.11.59.0", {"start": v(5.5, 67.63) * mm, "end": v(5.32, 65.89) * mm});
            skLineSegment(sketch, "E9.14.59.0", {"start": v(8.5, 65.55) * mm, "end": v(8.68, 67.3) * mm});
            skSolve(sketch);
        }
        {
            var Q0;
            Q0=qSketchRegion(id+"F0",true);
            extrude(context, id + "F1", {"entities" : qUnion([Q0]), "depth" : 10 * mm, "offsetDistance" : 25 * mm});
        }
        {
            var Q0;
            Q0=makeQuery(id+"F1.opExtrude","CAP_FACE",FACE,{"disambiguationData":[OSD([sQuery(id+"F0.wireOp",EDGE,"E0"),sQuery(id+"F0.wireOp",EDGE,"E1"),sQuery(id+"F0.wireOp",EDGE,"E3"),sQuery(id+"F0.wireOp",EDGE,"E4"),sQuery(id+"F0.wireOp",EDGE,"E5"),sQuery(id+"F0.wireOp",EDGE,"E6.trimOffspring"),sQuery(id+"F0.wireOp",EDGE,"E7"),sQuery(id+"F0.wireOp",EDGE,"E8.1.0"),sQuery(id+"F0.wireOp",EDGE,"E8.1.1"),sQuery(id+"F0.wireOp",EDGE,"E8.1.2"),sQuery(id+"F0.wireOp",EDGE,"E8.1.3"),sQuery(id+"F0.wireOp",EDGE,"E8.1.4"),sQuery(id+"F0.wireOp",EDGE,"E8.2.0"),sQuery(id+"F0.wireOp",EDGE,"E8.2.1"),sQuery(id+"F0.wireOp",EDGE,"E8.2.2"),sQuery(id+"F0.wireOp",EDGE,"E8.2.3"),sQuery(id+"F0.wireOp",EDGE,"E8.2.4"),sQuery(id+"F0.wireOp",EDGE,"E9.1.3.0"),sQuery(id+"F0.wireOp",EDGE,"E9.3.3.0"),sQuery(id+"F0.wireOp",EDGE,"E9.7.3.0"),sQuery(id+"F0.wireOp",EDGE,"E9.11.3.0"),sQuery(id+"F0.wireOp",EDGE,"E9.14.3.0"),sQuery(id+"F0.wireOp",EDGE,"E9.1.4.0"),sQuery(id+"F0.wireOp",EDGE,"E9.3.4.0"),sQuery(id+"F0.wireOp",EDGE,"E9.7.4.0"),sQuery(id+"F0.wireOp",EDGE,"E9.11.4.0"),sQuery(id+"F0.wireOp",EDGE,"E9.14.4.0"),sQuery(id+"F0.wireOp",EDGE,"E9.1.5.0"),sQuery(id+"F0.wireOp",EDGE,"E9.3.5.0"),sQuery(id+"F0.wireOp",EDGE,"E9.7.5.0"),sQuery(id+"F0.wireOp",EDGE,"E9.11.5.0"),sQuery(id+"F0.wireOp",EDGE,"E9.14.5.0"),sQuery(id+"F0.wireOp",EDGE,"E9.1.6.0"),sQuery(id+"F0.wireOp",EDGE,"E9.3.6.0"),sQuery(id+"F0.wireOp",EDGE,"E9.7.6.0"),sQuery(id+"F0.wireOp",EDGE,"E9.11.6.0"),sQuery(id+"F0.wireOp",EDGE,"E9.14.6.0"),sQuery(id+"F0.wireOp",EDGE,"E9.1.7.0"),sQuery(id+"F0.wireOp",EDGE,"E9.3.7.0"),sQuery(id+"F0.wireOp",EDGE,"E9.7.7.0"),sQuery(id+"F0.wireOp",EDGE,"E9.11.7.0"),sQuery(id+"F0.wireOp",EDGE,"E9.14.7.0"),sQuery(id+"F0.wireOp",EDGE,"E9.1.8.0"),sQuery(id+"F0.wireOp",EDGE,"E9.3.8.0"),sQuery(id+"F0.wireOp",EDGE,"E9.7.8.0"),sQuery(id+"F0.wireOp",EDGE,"E9.11.8.0"),sQuery(id+"F0.wireOp",EDGE,"E9.14.8.0"),sQuery(id+"F0.wireOp",EDGE,"E9.1.9.0"),sQuery(id+"F0.wireOp",EDGE,"E9.3.9.0"),sQuery(id+"F0.wireOp",EDGE,"E9.7.9.0"),sQuery(id+"F0.wireOp",EDGE,"E9.11.9.0"),sQuery(id+"F0.wireOp",EDGE,"E9.14.9.0"),sQuery(id+"F0.wireOp",EDGE,"E9.1.10.0"),sQuery(id+"F0.wireOp",EDGE,"E9.3.10.0"),sQuery(id+"F0.wireOp",EDGE,"E9.7.10.0"),sQuery(id+"F0.wireOp",EDGE,"E9.11.10.0"),sQuery(id+"F0.wireOp",EDGE,"E9.14.10.0"),sQuery(id+"F0.wireOp",EDGE,"E9.1.11.0"),sQuery(id+"F0.wireOp",EDGE,"E9.3.11.0"),sQuery(id+"F0.wireOp",EDGE,"E9.7.11.0"),sQuery(id+"F0.wireOp",EDGE,"E9.11.11.0"),sQuery(id+"F0.wireOp",EDGE,"E9.14.11.0"),sQuery(id+"F0.wireOp",EDGE,"E9.1.12.0"),sQuery(id+"F0.wireOp",EDGE,"E9.3.12.0"),sQuery(id+"F0.wireOp",EDGE,"E9.7.12.0"),sQuery(id+"F0.wireOp",EDGE,"E9.11.12.0"),sQuery(id+"F0.wireOp",EDGE,"E9.14.12.0"),sQuery(id+"F0.wireOp",EDGE,"E9.1.13.0"),sQuery(id+"F0.wireOp",EDGE,"E9.3.13.0"),sQuery(id+"F0.wireOp",EDGE,"E9.7.13.0"),sQuery(id+"F0.wireOp",EDGE,"E9.11.13.0"),sQuery(id+"F0.wireOp",EDGE,"E9.14.13.0"),sQuery(id+"F0.wireOp",EDGE,"E9.1.14.0"),sQuery(id+"F0.wireOp",EDGE,"E9.3.14.0"),sQuery(id+"F0.wireOp",EDGE,"E9.7.14.0"),sQuery(id+"F0.wireOp",EDGE,"E9.11.14.0"),sQuery(id+"F0.wireOp",EDGE,"E9.14.14.0"),sQuery(id+"F0.wireOp",EDGE,"E9.1.15.0"),sQuery(id+"F0.wireOp",EDGE,"E9.3.15.0"),sQuery(id+"F0.wireOp",EDGE,"E9.7.15.0"),sQuery(id+"F0.wireOp",EDGE,"E9.11.15.0"),sQuery(id+"F0.wireOp",EDGE,"E9.14.15.0"),sQuery(id+"F0.wireOp",EDGE,"E9.1.16.0"),sQuery(id+"F0.wireOp",EDGE,"E9.3.16.0"),sQuery(id+"F0.wireOp",EDGE,"E9.7.16.0"),sQuery(id+"F0.wireOp",EDGE,"E9.11.16.0"),sQuery(id+"F0.wireOp",EDGE,"E9.14.16.0"),sQuery(id+"F0.wireOp",EDGE,"E9.1.17.0"),sQuery(id+"F0.wireOp",EDGE,"E9.3.17.0"),sQuery(id+"F0.wireOp",EDGE,"E9.7.17.0"),sQuery(id+"F0.wireOp",EDGE,"E9.11.17.0"),sQuery(id+"F0.wireOp",EDGE,"E9.14.17.0"),sQuery(id+"F0.wireOp",EDGE,"E9.1.18.0"),sQuery(id+"F0.wireOp",EDGE,"E9.3.18.0"),sQuery(id+"F0.wireOp",EDGE,"E9.7.18.0"),sQuery(id+"F0.wireOp",EDGE,"E9.11.18.0"),sQuery(id+"F0.wireOp",EDGE,"E9.14.18.0"),sQuery(id+"F0.wireOp",EDGE,"E9.1.19.0"),sQuery(id+"F0.wireOp",EDGE,"E9.3.19.0"),sQuery(id+"F0.wireOp",EDGE,"E9.7.19.0"),sQuery(id+"F0.wireOp",EDGE,"E9.11.19.0"),sQuery(id+"F0.wireOp",EDGE,"E9.14.19.0"),sQuery(id+"F0.wireOp",EDGE,"E9.1.20.0"),sQuery(id+"F0.wireOp",EDGE,"E9.3.20.0"),sQuery(id+"F0.wireOp",EDGE,"E9.7.20.0"),sQuery(id+"F0.wireOp",EDGE,"E9.11.20.0"),sQuery(id+"F0.wireOp",EDGE,"E9.14.20.0"),sQuery(id+"F0.wireOp",EDGE,"E9.1.21.0"),sQuery(id+"F0.wireOp",EDGE,"E9.3.21.0"),sQuery(id+"F0.wireOp",EDGE,"E9.7.21.0"),sQuery(id+"F0.wireOp",EDGE,"E9.11.21.0"),sQuery(id+"F0.wireOp",EDGE,"E9.14.21.0"),sQuery(id+"F0.wireOp",EDGE,"E9.1.22.0"),sQuery(id+"F0.wireOp",EDGE,"E9.3.22.0"),sQuery(id+"F0.wireOp",EDGE,"E9.7.22.0"),sQuery(id+"F0.wireOp",EDGE,"E9.11.22.0"),sQuery(id+"F0.wireOp",EDGE,"E9.14.22.0"),sQuery(id+"F0.wireOp",EDGE,"E9.1.23.0"),sQuery(id+"F0.wireOp",EDGE,"E9.3.23.0"),sQuery(id+"F0.wireOp",EDGE,"E9.7.23.0"),sQuery(id+"F0.wireOp",EDGE,"E9.11.23.0"),sQuery(id+"F0.wireOp",EDGE,"E9.14.23.0"),sQuery(id+"F0.wireOp",EDGE,"E9.1.24.0"),sQuery(id+"F0.wireOp",EDGE,"E9.3.24.0"),sQuery(id+"F0.wireOp",EDGE,"E9.7.24.0"),sQuery(id+"F0.wireOp",EDGE,"E9.11.24.0"),sQuery(id+"F0.wireOp",EDGE,"E9.14.24.0"),sQuery(id+"F0.wireOp",EDGE,"E9.1.25.0"),sQuery(id+"F0.wireOp",EDGE,"E9.3.25.0"),sQuery(id+"F0.wireOp",EDGE,"E9.7.25.0"),sQuery(id+"F0.wireOp",EDGE,"E9.11.25.0"),sQuery(id+"F0.wireOp",EDGE,"E9.14.25.0"),sQuery(id+"F0.wireOp",EDGE,"E9.1.26.0"),sQuery(id+"F0.wireOp",EDGE,"E9.3.26.0"),sQuery(id+"F0.wireOp",EDGE,"E9.7.26.0"),sQuery(id+"F0.wireOp",EDGE,"E9.11.26.0"),sQuery(id+"F0.wireOp",EDGE,"E9.14.26.0"),sQuery(id+"F0.wireOp",EDGE,"E9.1.27.0"),sQuery(id+"F0.wireOp",EDGE,"E9.3.27.0"),sQuery(id+"F0.wireOp",EDGE,"E9.7.27.0"),sQuery(id+"F0.wireOp",EDGE,"E9.11.27.0"),sQuery(id+"F0.wireOp",EDGE,"E9.14.27.0"),sQuery(id+"F0.wireOp",EDGE,"E9.1.28.0"),sQuery(id+"F0.wireOp",EDGE,"E9.3.28.0"),sQuery(id+"F0.wireOp",EDGE,"E9.7.28.0"),sQuery(id+"F0.wireOp",EDGE,"E9.11.28.0"),sQuery(id+"F0.wireOp",EDGE,"E9.14.28.0"),sQuery(id+"F0.wireOp",EDGE,"E9.1.29.0"),sQuery(id+"F0.wireOp",EDGE,"E9.3.29.0"),sQuery(id+"F0.wireOp",EDGE,"E9.7.29.0"),sQuery(id+"F0.wireOp",EDGE,"E9.11.29.0"),sQuery(id+"F0.wireOp",EDGE,"E9.14.29.0"),sQuery(id+"F0.wireOp",EDGE,"E9.1.30.0"),sQuery(id+"F0.wireOp",EDGE,"E9.3.30.0"),sQuery(id+"F0.wireOp",EDGE,"E9.7.30.0"),sQuery(id+"F0.wireOp",EDGE,"E9.11.30.0"),sQuery(id+"F0.wireOp",EDGE,"E9.14.30.0"),sQuery(id+"F0.wireOp",EDGE,"E9.1.31.0"),sQuery(id+"F0.wireOp",EDGE,"E9.3.31.0"),sQuery(id+"F0.wireOp",EDGE,"E9.7.31.0"),sQuery(id+"F0.wireOp",EDGE,"E9.11.31.0"),sQuery(id+"F0.wireOp",EDGE,"E9.14.31.0"),sQuery(id+"F0.wireOp",EDGE,"E9.1.32.0"),sQuery(id+"F0.wireOp",EDGE,"E9.3.32.0"),sQuery(id+"F0.wireOp",EDGE,"E9.7.32.0"),sQuery(id+"F0.wireOp",EDGE,"E9.11.32.0"),sQuery(id+"F0.wireOp",EDGE,"E9.14.32.0"),sQuery(id+"F0.wireOp",EDGE,"E9.1.33.0"),sQuery(id+"F0.wireOp",EDGE,"E9.3.33.0"),sQuery(id+"F0.wireOp",EDGE,"E9.7.33.0"),sQuery(id+"F0.wireOp",EDGE,"E9.11.33.0"),sQuery(id+"F0.wireOp",EDGE,"E9.14.33.0"),sQuery(id+"F0.wireOp",EDGE,"E9.1.34.0"),sQuery(id+"F0.wireOp",EDGE,"E9.3.34.0"),sQuery(id+"F0.wireOp",EDGE,"E9.7.34.0"),sQuery(id+"F0.wireOp",EDGE,"E9.11.34.0"),sQuery(id+"F0.wireOp",EDGE,"E9.14.34.0"),sQuery(id+"F0.wireOp",EDGE,"E9.1.35.0"),sQuery(id+"F0.wireOp",EDGE,"E9.3.35.0"),sQuery(id+"F0.wireOp",EDGE,"E9.7.35.0"),sQuery(id+"F0.wireOp",EDGE,"E9.11.35.0"),sQuery(id+"F0.wireOp",EDGE,"E9.14.35.0"),sQuery(id+"F0.wireOp",EDGE,"E9.1.36.0"),sQuery(id+"F0.wireOp",EDGE,"E9.3.36.0"),sQuery(id+"F0.wireOp",EDGE,"E9.7.36.0"),sQuery(id+"F0.wireOp",EDGE,"E9.11.36.0"),sQuery(id+"F0.wireOp",EDGE,"E9.14.36.0"),sQuery(id+"F0.wireOp",EDGE,"E9.1.37.0"),sQuery(id+"F0.wireOp",EDGE,"E9.3.37.0"),sQuery(id+"F0.wireOp",EDGE,"E9.7.37.0"),sQuery(id+"F0.wireOp",EDGE,"E9.11.37.0"),sQuery(id+"F0.wireOp",EDGE,"E9.14.37.0"),sQuery(id+"F0.wireOp",EDGE,"E9.1.38.0"),sQuery(id+"F0.wireOp",EDGE,"E9.3.38.0"),sQuery(id+"F0.wireOp",EDGE,"E9.7.38.0"),sQuery(id+"F0.wireOp",EDGE,"E9.11.38.0"),sQuery(id+"F0.wireOp",EDGE,"E9.14.38.0"),sQuery(id+"F0.wireOp",EDGE,"E9.1.39.0"),sQuery(id+"F0.wireOp",EDGE,"E9.3.39.0"),sQuery(id+"F0.wireOp",EDGE,"E9.7.39.0"),sQuery(id+"F0.wireOp",EDGE,"E9.11.39.0"),sQuery(id+"F0.wireOp",EDGE,"E9.14.39.0"),sQuery(id+"F0.wireOp",EDGE,"E9.1.40.0"),sQuery(id+"F0.wireOp",EDGE,"E9.3.40.0"),sQuery(id+"F0.wireOp",EDGE,"E9.7.40.0"),sQuery(id+"F0.wireOp",EDGE,"E9.11.40.0"),sQuery(id+"F0.wireOp",EDGE,"E9.14.40.0"),sQuery(id+"F0.wireOp",EDGE,"E9.1.41.0"),sQuery(id+"F0.wireOp",EDGE,"E9.3.41.0"),sQuery(id+"F0.wireOp",EDGE,"E9.7.41.0"),sQuery(id+"F0.wireOp",EDGE,"E9.11.41.0"),sQuery(id+"F0.wireOp",EDGE,"E9.14.41.0"),sQuery(id+"F0.wireOp",EDGE,"E9.1.42.0"),sQuery(id+"F0.wireOp",EDGE,"E9.3.42.0"),sQuery(id+"F0.wireOp",EDGE,"E9.7.42.0"),sQuery(id+"F0.wireOp",EDGE,"E9.11.42.0"),sQuery(id+"F0.wireOp",EDGE,"E9.14.42.0"),sQuery(id+"F0.wireOp",EDGE,"E9.1.43.0"),sQuery(id+"F0.wireOp",EDGE,"E9.3.43.0"),sQuery(id+"F0.wireOp",EDGE,"E9.7.43.0"),sQuery(id+"F0.wireOp",EDGE,"E9.11.43.0"),sQuery(id+"F0.wireOp",EDGE,"E9.14.43.0"),sQuery(id+"F0.wireOp",EDGE,"E9.1.44.0"),sQuery(id+"F0.wireOp",EDGE,"E9.3.44.0"),sQuery(id+"F0.wireOp",EDGE,"E9.7.44.0"),sQuery(id+"F0.wireOp",EDGE,"E9.11.44.0"),sQuery(id+"F0.wireOp",EDGE,"E9.14.44.0"),sQuery(id+"F0.wireOp",EDGE,"E9.1.45.0"),sQuery(id+"F0.wireOp",EDGE,"E9.3.45.0"),sQuery(id+"F0.wireOp",EDGE,"E9.7.45.0"),sQuery(id+"F0.wireOp",EDGE,"E9.11.45.0"),sQuery(id+"F0.wireOp",EDGE,"E9.14.45.0"),sQuery(id+"F0.wireOp",EDGE,"E9.1.46.0"),sQuery(id+"F0.wireOp",EDGE,"E9.3.46.0"),sQuery(id+"F0.wireOp",EDGE,"E9.7.46.0"),sQuery(id+"F0.wireOp",EDGE,"E9.11.46.0"),sQuery(id+"F0.wireOp",EDGE,"E9.14.46.0"),sQuery(id+"F0.wireOp",EDGE,"E9.1.47.0"),sQuery(id+"F0.wireOp",EDGE,"E9.3.47.0"),sQuery(id+"F0.wireOp",EDGE,"E9.7.47.0"),sQuery(id+"F0.wireOp",EDGE,"E9.11.47.0"),sQuery(id+"F0.wireOp",EDGE,"E9.14.47.0"),sQuery(id+"F0.wireOp",EDGE,"E9.1.48.0"),sQuery(id+"F0.wireOp",EDGE,"E9.3.48.0"),sQuery(id+"F0.wireOp",EDGE,"E9.7.48.0"),sQuery(id+"F0.wireOp",EDGE,"E9.11.48.0"),sQuery(id+"F0.wireOp",EDGE,"E9.14.48.0"),sQuery(id+"F0.wireOp",EDGE,"E9.1.49.0"),sQuery(id+"F0.wireOp",EDGE,"E9.3.49.0"),sQuery(id+"F0.wireOp",EDGE,"E9.7.49.0"),sQuery(id+"F0.wireOp",EDGE,"E9.11.49.0"),sQuery(id+"F0.wireOp",EDGE,"E9.14.49.0"),sQuery(id+"F0.wireOp",EDGE,"E9.1.50.0"),sQuery(id+"F0.wireOp",EDGE,"E9.3.50.0"),sQuery(id+"F0.wireOp",EDGE,"E9.7.50.0"),sQuery(id+"F0.wireOp",EDGE,"E9.11.50.0"),sQuery(id+"F0.wireOp",EDGE,"E9.14.50.0"),sQuery(id+"F0.wireOp",EDGE,"E9.1.51.0"),sQuery(id+"F0.wireOp",EDGE,"E9.3.51.0"),sQuery(id+"F0.wireOp",EDGE,"E9.7.51.0"),sQuery(id+"F0.wireOp",EDGE,"E9.11.51.0"),sQuery(id+"F0.wireOp",EDGE,"E9.14.51.0"),sQuery(id+"F0.wireOp",EDGE,"E9.1.52.0"),sQuery(id+"F0.wireOp",EDGE,"E9.3.52.0"),sQuery(id+"F0.wireOp",EDGE,"E9.7.52.0"),sQuery(id+"F0.wireOp",EDGE,"E9.11.52.0"),sQuery(id+"F0.wireOp",EDGE,"E9.14.52.0"),sQuery(id+"F0.wireOp",EDGE,"E9.1.53.0"),sQuery(id+"F0.wireOp",EDGE,"E9.3.53.0"),sQuery(id+"F0.wireOp",EDGE,"E9.7.53.0"),sQuery(id+"F0.wireOp",EDGE,"E9.11.53.0"),sQuery(id+"F0.wireOp",EDGE,"E9.14.53.0"),sQuery(id+"F0.wireOp",EDGE,"E9.1.54.0"),sQuery(id+"F0.wireOp",EDGE,"E9.3.54.0"),sQuery(id+"F0.wireOp",EDGE,"E9.7.54.0"),sQuery(id+"F0.wireOp",EDGE,"E9.11.54.0"),sQuery(id+"F0.wireOp",EDGE,"E9.14.54.0"),sQuery(id+"F0.wireOp",EDGE,"E9.1.55.0"),sQuery(id+"F0.wireOp",EDGE,"E9.3.55.0"),sQuery(id+"F0.wireOp",EDGE,"E9.7.55.0"),sQuery(id+"F0.wireOp",EDGE,"E9.11.55.0"),sQuery(id+"F0.wireOp",EDGE,"E9.14.55.0"),sQuery(id+"F0.wireOp",EDGE,"E9.1.56.0"),sQuery(id+"F0.wireOp",EDGE,"E9.3.56.0"),sQuery(id+"F0.wireOp",EDGE,"E9.7.56.0"),sQuery(id+"F0.wireOp",EDGE,"E9.11.56.0"),sQuery(id+"F0.wireOp",EDGE,"E9.14.56.0"),sQuery(id+"F0.wireOp",EDGE,"E9.1.57.0"),sQuery(id+"F0.wireOp",EDGE,"E9.3.57.0"),sQuery(id+"F0.wireOp",EDGE,"E9.7.57.0"),sQuery(id+"F0.wireOp",EDGE,"E9.11.57.0"),sQuery(id+"F0.wireOp",EDGE,"E9.14.57.0"),sQuery(id+"F0.wireOp",EDGE,"E9.1.58.0"),sQuery(id+"F0.wireOp",EDGE,"E9.3.58.0"),sQuery(id+"F0.wireOp",EDGE,"E9.7.58.0"),sQuery(id+"F0.wireOp",EDGE,"E9.11.58.0"),sQuery(id+"F0.wireOp",EDGE,"E9.14.58.0"),sQuery(id+"F0.wireOp",EDGE,"E9.1.59.0"),sQuery(id+"F0.wireOp",EDGE,"E9.3.59.0"),sQuery(id+"F0.wireOp",EDGE,"E9.7.59.0"),sQuery(id+"F0.wireOp",EDGE,"E9.11.59.0"),sQuery(id+"F0.wireOp",EDGE,"E9.14.59.0")])],"isStart":false});
            var sketch = newSketch(context, id + "F2", { "sketchPlane" : qUnion([Q0])});
            skCircle(sketch, "E10", {"center": v(0, 0) * mm, "radius": 64 * mm});
            skCircle(sketch, "E11", {"center": v(0, 0) * mm, "radius": 63 * mm});
            skCircle(sketch, "E12", {"center": v(0, 0) * mm, "radius": 60 * mm});
            skCircle(sketch, "E13", {"center": v(0, 0) * mm, "radius": 59 * mm});
            skCircle(sketch, "E14", {"center": v(0, 0) * mm, "radius": 10 * mm});
            skCircle(sketch, "E15", {"center": v(0, 0) * mm, "radius": 58 * mm});
            skCircle(sketch, "E16", {"center": v(0, 0) * mm, "radius": 11 * mm});
            skLineSegment(sketch, "E17", {"start": v(0, -58) * mm, "end": v(0, 58) * mm, "construction": true});
            skLineSegment(sketch, "E18", {"start": v(58, 0) * mm, "end": v(-58, 0) * mm, "construction": true});
            skLineSegment(sketch, "E19", {"start": v(-46.28, 5) * mm, "end": v(-14.5, 5) * mm});
            skLineSegment(sketch, "E20.0", {"start": v(-46.28, -5) * mm, "end": v(-14.5, -5) * mm});
            skLineSegment(sketch, "E21", {"start": v(-5, -46.28) * mm, "end": v(-5, -14.5) * mm});
            skLineSegment(sketch, "E22.0", {"start": v(5, -46.28) * mm, "end": v(5, -14.5) * mm});
            skArc(sketch, "E23", {"start": v(5, 14.5) * mm, "mid": v(7.8, 7.78) * mm, "end": v(14.5, 5) * mm});
            skArc(sketch, "E24", {"start": v(-14.5, 5) * mm, "mid": v(-7.77, 7.78) * mm, "end": v(-5, 14.5) * mm});
            skArc(sketch, "E25", {"start": v(-5, -14.5) * mm, "mid": v(-7.77, -7.78) * mm, "end": v(-14.5, -5) * mm});
            skArc(sketch, "E26", {"start": v(14.5, -5) * mm, "mid": v(7.8, -7.78) * mm, "end": v(5, -14.5) * mm});
            skArc(sketch, "E27", {"start": v(46.28, 5) * mm, "mid": v(53.94, 8.88) * mm, "end": v(55.35, 17.34) * mm});
            skArc(sketch, "E28", {"start": v(17.35, 55.34) * mm, "mid": v(8.88, 53.94) * mm, "end": v(5, 46.28) * mm});
            skArc(sketch, "E29", {"start": v(-5, 46.28) * mm, "mid": v(-8.87, 53.94) * mm, "end": v(-17.33, 55.35) * mm});
            skArc(sketch, "E30", {"start": v(-55.35, 17.34) * mm, "mid": v(-53.94, 8.88) * mm, "end": v(-46.28, 5) * mm});
            skArc(sketch, "E31", {"start": v(-46.28, -5) * mm, "mid": v(-53.94, -8.88) * mm, "end": v(-55.35, -17.34) * mm});
            skArc(sketch, "E32", {"start": v(-17.33, -55.35) * mm, "mid": v(-8.87, -53.94) * mm, "end": v(-5, -46.28) * mm});
            skArc(sketch, "E33", {"start": v(5, -46.28) * mm, "mid": v(8.88, -53.94) * mm, "end": v(17.35, -55.34) * mm});
            skArc(sketch, "E34", {"start": v(55.35, -17.34) * mm, "mid": v(53.94, -8.88) * mm, "end": v(46.28, -5) * mm});
            skLineSegment(sketch, "E35.trimOffspring", {"start": v(-5, 14.5) * mm, "end": v(-5, 46.28) * mm});
            skLineSegment(sketch, "E36.trimOffspring", {"start": v(14.5, 5) * mm, "end": v(46.28, 5) * mm});
            skLineSegment(sketch, "E37.trimOffspring", {"start": v(5, 14.5) * mm, "end": v(5, 46.28) * mm});
            skLineSegment(sketch, "E38.trimOffspring", {"start": v(14.5, -5) * mm, "end": v(46.28, -5) * mm});
            skSolve(sketch);
        }
        {
            var Q0;
            Q0=makeQuery(id+"F1.opExtrude","CAP_FACE",FACE,{"disambiguationData":[OSD([sQuery(id+"F0.wireOp",EDGE,"E0"),sQuery(id+"F0.wireOp",EDGE,"E1"),sQuery(id+"F0.wireOp",EDGE,"E3"),sQuery(id+"F0.wireOp",EDGE,"E4"),sQuery(id+"F0.wireOp",EDGE,"E5"),sQuery(id+"F0.wireOp",EDGE,"E6.trimOffspring"),sQuery(id+"F0.wireOp",EDGE,"E7"),sQuery(id+"F0.wireOp",EDGE,"E8.1.0"),sQuery(id+"F0.wireOp",EDGE,"E8.1.1"),sQuery(id+"F0.wireOp",EDGE,"E8.1.2"),sQuery(id+"F0.wireOp",EDGE,"E8.1.3"),sQuery(id+"F0.wireOp",EDGE,"E8.1.4"),sQuery(id+"F0.wireOp",EDGE,"E8.2.0"),sQuery(id+"F0.wireOp",EDGE,"E8.2.1"),sQuery(id+"F0.wireOp",EDGE,"E8.2.2"),sQuery(id+"F0.wireOp",EDGE,"E8.2.3"),sQuery(id+"F0.wireOp",EDGE,"E8.2.4"),sQuery(id+"F0.wireOp",EDGE,"E9.1.3.0"),sQuery(id+"F0.wireOp",EDGE,"E9.3.3.0"),sQuery(id+"F0.wireOp",EDGE,"E9.7.3.0"),sQuery(id+"F0.wireOp",EDGE,"E9.11.3.0"),sQuery(id+"F0.wireOp",EDGE,"E9.14.3.0"),sQuery(id+"F0.wireOp",EDGE,"E9.1.4.0"),sQuery(id+"F0.wireOp",EDGE,"E9.3.4.0"),sQuery(id+"F0.wireOp",EDGE,"E9.7.4.0"),sQuery(id+"F0.wireOp",EDGE,"E9.11.4.0"),sQuery(id+"F0.wireOp",EDGE,"E9.14.4.0"),sQuery(id+"F0.wireOp",EDGE,"E9.1.5.0"),sQuery(id+"F0.wireOp",EDGE,"E9.3.5.0"),sQuery(id+"F0.wireOp",EDGE,"E9.7.5.0"),sQuery(id+"F0.wireOp",EDGE,"E9.11.5.0"),sQuery(id+"F0.wireOp",EDGE,"E9.14.5.0"),sQuery(id+"F0.wireOp",EDGE,"E9.1.6.0"),sQuery(id+"F0.wireOp",EDGE,"E9.3.6.0"),sQuery(id+"F0.wireOp",EDGE,"E9.7.6.0"),sQuery(id+"F0.wireOp",EDGE,"E9.11.6.0"),sQuery(id+"F0.wireOp",EDGE,"E9.14.6.0"),sQuery(id+"F0.wireOp",EDGE,"E9.1.7.0"),sQuery(id+"F0.wireOp",EDGE,"E9.3.7.0"),sQuery(id+"F0.wireOp",EDGE,"E9.7.7.0"),sQuery(id+"F0.wireOp",EDGE,"E9.11.7.0"),sQuery(id+"F0.wireOp",EDGE,"E9.14.7.0"),sQuery(id+"F0.wireOp",EDGE,"E9.1.8.0"),sQuery(id+"F0.wireOp",EDGE,"E9.3.8.0"),sQuery(id+"F0.wireOp",EDGE,"E9.7.8.0"),sQuery(id+"F0.wireOp",EDGE,"E9.11.8.0"),sQuery(id+"F0.wireOp",EDGE,"E9.14.8.0"),sQuery(id+"F0.wireOp",EDGE,"E9.1.9.0"),sQuery(id+"F0.wireOp",EDGE,"E9.3.9.0"),sQuery(id+"F0.wireOp",EDGE,"E9.7.9.0"),sQuery(id+"F0.wireOp",EDGE,"E9.11.9.0"),sQuery(id+"F0.wireOp",EDGE,"E9.14.9.0"),sQuery(id+"F0.wireOp",EDGE,"E9.1.10.0"),sQuery(id+"F0.wireOp",EDGE,"E9.3.10.0"),sQuery(id+"F0.wireOp",EDGE,"E9.7.10.0"),sQuery(id+"F0.wireOp",EDGE,"E9.11.10.0"),sQuery(id+"F0.wireOp",EDGE,"E9.14.10.0"),sQuery(id+"F0.wireOp",EDGE,"E9.1.11.0"),sQuery(id+"F0.wireOp",EDGE,"E9.3.11.0"),sQuery(id+"F0.wireOp",EDGE,"E9.7.11.0"),sQuery(id+"F0.wireOp",EDGE,"E9.11.11.0"),sQuery(id+"F0.wireOp",EDGE,"E9.14.11.0"),sQuery(id+"F0.wireOp",EDGE,"E9.1.12.0"),sQuery(id+"F0.wireOp",EDGE,"E9.3.12.0"),sQuery(id+"F0.wireOp",EDGE,"E9.7.12.0"),sQuery(id+"F0.wireOp",EDGE,"E9.11.12.0"),sQuery(id+"F0.wireOp",EDGE,"E9.14.12.0"),sQuery(id+"F0.wireOp",EDGE,"E9.1.13.0"),sQuery(id+"F0.wireOp",EDGE,"E9.3.13.0"),sQuery(id+"F0.wireOp",EDGE,"E9.7.13.0"),sQuery(id+"F0.wireOp",EDGE,"E9.11.13.0"),sQuery(id+"F0.wireOp",EDGE,"E9.14.13.0"),sQuery(id+"F0.wireOp",EDGE,"E9.1.14.0"),sQuery(id+"F0.wireOp",EDGE,"E9.3.14.0"),sQuery(id+"F0.wireOp",EDGE,"E9.7.14.0"),sQuery(id+"F0.wireOp",EDGE,"E9.11.14.0"),sQuery(id+"F0.wireOp",EDGE,"E9.14.14.0"),sQuery(id+"F0.wireOp",EDGE,"E9.1.15.0"),sQuery(id+"F0.wireOp",EDGE,"E9.3.15.0"),sQuery(id+"F0.wireOp",EDGE,"E9.7.15.0"),sQuery(id+"F0.wireOp",EDGE,"E9.11.15.0"),sQuery(id+"F0.wireOp",EDGE,"E9.14.15.0"),sQuery(id+"F0.wireOp",EDGE,"E9.1.16.0"),sQuery(id+"F0.wireOp",EDGE,"E9.3.16.0"),sQuery(id+"F0.wireOp",EDGE,"E9.7.16.0"),sQuery(id+"F0.wireOp",EDGE,"E9.11.16.0"),sQuery(id+"F0.wireOp",EDGE,"E9.14.16.0"),sQuery(id+"F0.wireOp",EDGE,"E9.1.17.0"),sQuery(id+"F0.wireOp",EDGE,"E9.3.17.0"),sQuery(id+"F0.wireOp",EDGE,"E9.7.17.0"),sQuery(id+"F0.wireOp",EDGE,"E9.11.17.0"),sQuery(id+"F0.wireOp",EDGE,"E9.14.17.0"),sQuery(id+"F0.wireOp",EDGE,"E9.1.18.0"),sQuery(id+"F0.wireOp",EDGE,"E9.3.18.0"),sQuery(id+"F0.wireOp",EDGE,"E9.7.18.0"),sQuery(id+"F0.wireOp",EDGE,"E9.11.18.0"),sQuery(id+"F0.wireOp",EDGE,"E9.14.18.0"),sQuery(id+"F0.wireOp",EDGE,"E9.1.19.0"),sQuery(id+"F0.wireOp",EDGE,"E9.3.19.0"),sQuery(id+"F0.wireOp",EDGE,"E9.7.19.0"),sQuery(id+"F0.wireOp",EDGE,"E9.11.19.0"),sQuery(id+"F0.wireOp",EDGE,"E9.14.19.0"),sQuery(id+"F0.wireOp",EDGE,"E9.1.20.0"),sQuery(id+"F0.wireOp",EDGE,"E9.3.20.0"),sQuery(id+"F0.wireOp",EDGE,"E9.7.20.0"),sQuery(id+"F0.wireOp",EDGE,"E9.11.20.0"),sQuery(id+"F0.wireOp",EDGE,"E9.14.20.0"),sQuery(id+"F0.wireOp",EDGE,"E9.1.21.0"),sQuery(id+"F0.wireOp",EDGE,"E9.3.21.0"),sQuery(id+"F0.wireOp",EDGE,"E9.7.21.0"),sQuery(id+"F0.wireOp",EDGE,"E9.11.21.0"),sQuery(id+"F0.wireOp",EDGE,"E9.14.21.0"),sQuery(id+"F0.wireOp",EDGE,"E9.1.22.0"),sQuery(id+"F0.wireOp",EDGE,"E9.3.22.0"),sQuery(id+"F0.wireOp",EDGE,"E9.7.22.0"),sQuery(id+"F0.wireOp",EDGE,"E9.11.22.0"),sQuery(id+"F0.wireOp",EDGE,"E9.14.22.0"),sQuery(id+"F0.wireOp",EDGE,"E9.1.23.0"),sQuery(id+"F0.wireOp",EDGE,"E9.3.23.0"),sQuery(id+"F0.wireOp",EDGE,"E9.7.23.0"),sQuery(id+"F0.wireOp",EDGE,"E9.11.23.0"),sQuery(id+"F0.wireOp",EDGE,"E9.14.23.0"),sQuery(id+"F0.wireOp",EDGE,"E9.1.24.0"),sQuery(id+"F0.wireOp",EDGE,"E9.3.24.0"),sQuery(id+"F0.wireOp",EDGE,"E9.7.24.0"),sQuery(id+"F0.wireOp",EDGE,"E9.11.24.0"),sQuery(id+"F0.wireOp",EDGE,"E9.14.24.0"),sQuery(id+"F0.wireOp",EDGE,"E9.1.25.0"),sQuery(id+"F0.wireOp",EDGE,"E9.3.25.0"),sQuery(id+"F0.wireOp",EDGE,"E9.7.25.0"),sQuery(id+"F0.wireOp",EDGE,"E9.11.25.0"),sQuery(id+"F0.wireOp",EDGE,"E9.14.25.0"),sQuery(id+"F0.wireOp",EDGE,"E9.1.26.0"),sQuery(id+"F0.wireOp",EDGE,"E9.3.26.0"),sQuery(id+"F0.wireOp",EDGE,"E9.7.26.0"),sQuery(id+"F0.wireOp",EDGE,"E9.11.26.0"),sQuery(id+"F0.wireOp",EDGE,"E9.14.26.0"),sQuery(id+"F0.wireOp",EDGE,"E9.1.27.0"),sQuery(id+"F0.wireOp",EDGE,"E9.3.27.0"),sQuery(id+"F0.wireOp",EDGE,"E9.7.27.0"),sQuery(id+"F0.wireOp",EDGE,"E9.11.27.0"),sQuery(id+"F0.wireOp",EDGE,"E9.14.27.0"),sQuery(id+"F0.wireOp",EDGE,"E9.1.28.0"),sQuery(id+"F0.wireOp",EDGE,"E9.3.28.0"),sQuery(id+"F0.wireOp",EDGE,"E9.7.28.0"),sQuery(id+"F0.wireOp",EDGE,"E9.11.28.0"),sQuery(id+"F0.wireOp",EDGE,"E9.14.28.0"),sQuery(id+"F0.wireOp",EDGE,"E9.1.29.0"),sQuery(id+"F0.wireOp",EDGE,"E9.3.29.0"),sQuery(id+"F0.wireOp",EDGE,"E9.7.29.0"),sQuery(id+"F0.wireOp",EDGE,"E9.11.29.0"),sQuery(id+"F0.wireOp",EDGE,"E9.14.29.0"),sQuery(id+"F0.wireOp",EDGE,"E9.1.30.0"),sQuery(id+"F0.wireOp",EDGE,"E9.3.30.0"),sQuery(id+"F0.wireOp",EDGE,"E9.7.30.0"),sQuery(id+"F0.wireOp",EDGE,"E9.11.30.0"),sQuery(id+"F0.wireOp",EDGE,"E9.14.30.0"),sQuery(id+"F0.wireOp",EDGE,"E9.1.31.0"),sQuery(id+"F0.wireOp",EDGE,"E9.3.31.0"),sQuery(id+"F0.wireOp",EDGE,"E9.7.31.0"),sQuery(id+"F0.wireOp",EDGE,"E9.11.31.0"),sQuery(id+"F0.wireOp",EDGE,"E9.14.31.0"),sQuery(id+"F0.wireOp",EDGE,"E9.1.32.0"),sQuery(id+"F0.wireOp",EDGE,"E9.3.32.0"),sQuery(id+"F0.wireOp",EDGE,"E9.7.32.0"),sQuery(id+"F0.wireOp",EDGE,"E9.11.32.0"),sQuery(id+"F0.wireOp",EDGE,"E9.14.32.0"),sQuery(id+"F0.wireOp",EDGE,"E9.1.33.0"),sQuery(id+"F0.wireOp",EDGE,"E9.3.33.0"),sQuery(id+"F0.wireOp",EDGE,"E9.7.33.0"),sQuery(id+"F0.wireOp",EDGE,"E9.11.33.0"),sQuery(id+"F0.wireOp",EDGE,"E9.14.33.0"),sQuery(id+"F0.wireOp",EDGE,"E9.1.34.0"),sQuery(id+"F0.wireOp",EDGE,"E9.3.34.0"),sQuery(id+"F0.wireOp",EDGE,"E9.7.34.0"),sQuery(id+"F0.wireOp",EDGE,"E9.11.34.0"),sQuery(id+"F0.wireOp",EDGE,"E9.14.34.0"),sQuery(id+"F0.wireOp",EDGE,"E9.1.35.0"),sQuery(id+"F0.wireOp",EDGE,"E9.3.35.0"),sQuery(id+"F0.wireOp",EDGE,"E9.7.35.0"),sQuery(id+"F0.wireOp",EDGE,"E9.11.35.0"),sQuery(id+"F0.wireOp",EDGE,"E9.14.35.0"),sQuery(id+"F0.wireOp",EDGE,"E9.1.36.0"),sQuery(id+"F0.wireOp",EDGE,"E9.3.36.0"),sQuery(id+"F0.wireOp",EDGE,"E9.7.36.0"),sQuery(id+"F0.wireOp",EDGE,"E9.11.36.0"),sQuery(id+"F0.wireOp",EDGE,"E9.14.36.0"),sQuery(id+"F0.wireOp",EDGE,"E9.1.37.0"),sQuery(id+"F0.wireOp",EDGE,"E9.3.37.0"),sQuery(id+"F0.wireOp",EDGE,"E9.7.37.0"),sQuery(id+"F0.wireOp",EDGE,"E9.11.37.0"),sQuery(id+"F0.wireOp",EDGE,"E9.14.37.0"),sQuery(id+"F0.wireOp",EDGE,"E9.1.38.0"),sQuery(id+"F0.wireOp",EDGE,"E9.3.38.0"),sQuery(id+"F0.wireOp",EDGE,"E9.7.38.0"),sQuery(id+"F0.wireOp",EDGE,"E9.11.38.0"),sQuery(id+"F0.wireOp",EDGE,"E9.14.38.0"),sQuery(id+"F0.wireOp",EDGE,"E9.1.39.0"),sQuery(id+"F0.wireOp",EDGE,"E9.3.39.0"),sQuery(id+"F0.wireOp",EDGE,"E9.7.39.0"),sQuery(id+"F0.wireOp",EDGE,"E9.11.39.0"),sQuery(id+"F0.wireOp",EDGE,"E9.14.39.0"),sQuery(id+"F0.wireOp",EDGE,"E9.1.40.0"),sQuery(id+"F0.wireOp",EDGE,"E9.3.40.0"),sQuery(id+"F0.wireOp",EDGE,"E9.7.40.0"),sQuery(id+"F0.wireOp",EDGE,"E9.11.40.0"),sQuery(id+"F0.wireOp",EDGE,"E9.14.40.0"),sQuery(id+"F0.wireOp",EDGE,"E9.1.41.0"),sQuery(id+"F0.wireOp",EDGE,"E9.3.41.0"),sQuery(id+"F0.wireOp",EDGE,"E9.7.41.0"),sQuery(id+"F0.wireOp",EDGE,"E9.11.41.0"),sQuery(id+"F0.wireOp",EDGE,"E9.14.41.0"),sQuery(id+"F0.wireOp",EDGE,"E9.1.42.0"),sQuery(id+"F0.wireOp",EDGE,"E9.3.42.0"),sQuery(id+"F0.wireOp",EDGE,"E9.7.42.0"),sQuery(id+"F0.wireOp",EDGE,"E9.11.42.0"),sQuery(id+"F0.wireOp",EDGE,"E9.14.42.0"),sQuery(id+"F0.wireOp",EDGE,"E9.1.43.0"),sQuery(id+"F0.wireOp",EDGE,"E9.3.43.0"),sQuery(id+"F0.wireOp",EDGE,"E9.7.43.0"),sQuery(id+"F0.wireOp",EDGE,"E9.11.43.0"),sQuery(id+"F0.wireOp",EDGE,"E9.14.43.0"),sQuery(id+"F0.wireOp",EDGE,"E9.1.44.0"),sQuery(id+"F0.wireOp",EDGE,"E9.3.44.0"),sQuery(id+"F0.wireOp",EDGE,"E9.7.44.0"),sQuery(id+"F0.wireOp",EDGE,"E9.11.44.0"),sQuery(id+"F0.wireOp",EDGE,"E9.14.44.0"),sQuery(id+"F0.wireOp",EDGE,"E9.1.45.0"),sQuery(id+"F0.wireOp",EDGE,"E9.3.45.0"),sQuery(id+"F0.wireOp",EDGE,"E9.7.45.0"),sQuery(id+"F0.wireOp",EDGE,"E9.11.45.0"),sQuery(id+"F0.wireOp",EDGE,"E9.14.45.0"),sQuery(id+"F0.wireOp",EDGE,"E9.1.46.0"),sQuery(id+"F0.wireOp",EDGE,"E9.3.46.0"),sQuery(id+"F0.wireOp",EDGE,"E9.7.46.0"),sQuery(id+"F0.wireOp",EDGE,"E9.11.46.0"),sQuery(id+"F0.wireOp",EDGE,"E9.14.46.0"),sQuery(id+"F0.wireOp",EDGE,"E9.1.47.0"),sQuery(id+"F0.wireOp",EDGE,"E9.3.47.0"),sQuery(id+"F0.wireOp",EDGE,"E9.7.47.0"),sQuery(id+"F0.wireOp",EDGE,"E9.11.47.0"),sQuery(id+"F0.wireOp",EDGE,"E9.14.47.0"),sQuery(id+"F0.wireOp",EDGE,"E9.1.48.0"),sQuery(id+"F0.wireOp",EDGE,"E9.3.48.0"),sQuery(id+"F0.wireOp",EDGE,"E9.7.48.0"),sQuery(id+"F0.wireOp",EDGE,"E9.11.48.0"),sQuery(id+"F0.wireOp",EDGE,"E9.14.48.0"),sQuery(id+"F0.wireOp",EDGE,"E9.1.49.0"),sQuery(id+"F0.wireOp",EDGE,"E9.3.49.0"),sQuery(id+"F0.wireOp",EDGE,"E9.7.49.0"),sQuery(id+"F0.wireOp",EDGE,"E9.11.49.0"),sQuery(id+"F0.wireOp",EDGE,"E9.14.49.0"),sQuery(id+"F0.wireOp",EDGE,"E9.1.50.0"),sQuery(id+"F0.wireOp",EDGE,"E9.3.50.0"),sQuery(id+"F0.wireOp",EDGE,"E9.7.50.0"),sQuery(id+"F0.wireOp",EDGE,"E9.11.50.0"),sQuery(id+"F0.wireOp",EDGE,"E9.14.50.0"),sQuery(id+"F0.wireOp",EDGE,"E9.1.51.0"),sQuery(id+"F0.wireOp",EDGE,"E9.3.51.0"),sQuery(id+"F0.wireOp",EDGE,"E9.7.51.0"),sQuery(id+"F0.wireOp",EDGE,"E9.11.51.0"),sQuery(id+"F0.wireOp",EDGE,"E9.14.51.0"),sQuery(id+"F0.wireOp",EDGE,"E9.1.52.0"),sQuery(id+"F0.wireOp",EDGE,"E9.3.52.0"),sQuery(id+"F0.wireOp",EDGE,"E9.7.52.0"),sQuery(id+"F0.wireOp",EDGE,"E9.11.52.0"),sQuery(id+"F0.wireOp",EDGE,"E9.14.52.0"),sQuery(id+"F0.wireOp",EDGE,"E9.1.53.0"),sQuery(id+"F0.wireOp",EDGE,"E9.3.53.0"),sQuery(id+"F0.wireOp",EDGE,"E9.7.53.0"),sQuery(id+"F0.wireOp",EDGE,"E9.11.53.0"),sQuery(id+"F0.wireOp",EDGE,"E9.14.53.0"),sQuery(id+"F0.wireOp",EDGE,"E9.1.54.0"),sQuery(id+"F0.wireOp",EDGE,"E9.3.54.0"),sQuery(id+"F0.wireOp",EDGE,"E9.7.54.0"),sQuery(id+"F0.wireOp",EDGE,"E9.11.54.0"),sQuery(id+"F0.wireOp",EDGE,"E9.14.54.0"),sQuery(id+"F0.wireOp",EDGE,"E9.1.55.0"),sQuery(id+"F0.wireOp",EDGE,"E9.3.55.0"),sQuery(id+"F0.wireOp",EDGE,"E9.7.55.0"),sQuery(id+"F0.wireOp",EDGE,"E9.11.55.0"),sQuery(id+"F0.wireOp",EDGE,"E9.14.55.0"),sQuery(id+"F0.wireOp",EDGE,"E9.1.56.0"),sQuery(id+"F0.wireOp",EDGE,"E9.3.56.0"),sQuery(id+"F0.wireOp",EDGE,"E9.7.56.0"),sQuery(id+"F0.wireOp",EDGE,"E9.11.56.0"),sQuery(id+"F0.wireOp",EDGE,"E9.14.56.0"),sQuery(id+"F0.wireOp",EDGE,"E9.1.57.0"),sQuery(id+"F0.wireOp",EDGE,"E9.3.57.0"),sQuery(id+"F0.wireOp",EDGE,"E9.7.57.0"),sQuery(id+"F0.wireOp",EDGE,"E9.11.57.0"),sQuery(id+"F0.wireOp",EDGE,"E9.14.57.0"),sQuery(id+"F0.wireOp",EDGE,"E9.1.58.0"),sQuery(id+"F0.wireOp",EDGE,"E9.3.58.0"),sQuery(id+"F0.wireOp",EDGE,"E9.7.58.0"),sQuery(id+"F0.wireOp",EDGE,"E9.11.58.0"),sQuery(id+"F0.wireOp",EDGE,"E9.14.58.0"),sQuery(id+"F0.wireOp",EDGE,"E9.1.59.0"),sQuery(id+"F0.wireOp",EDGE,"E9.3.59.0"),sQuery(id+"F0.wireOp",EDGE,"E9.7.59.0"),sQuery(id+"F0.wireOp",EDGE,"E9.11.59.0"),sQuery(id+"F0.wireOp",EDGE,"E9.14.59.0")])],"isStart":true});
            var sketch = newSketch(context, id + "F3", { "sketchPlane" : qUnion([Q0])});
            skCircle(sketch, "E39", {"center": v(-0.15, 0.02) * mm, "radius": 64 * mm});
            skCircle(sketch, "E40", {"center": v(-0.15, 0.02) * mm, "radius": 63 * mm});
            skCircle(sketch, "E41", {"center": v(-0.15, 0.02) * mm, "radius": 60 * mm});
            skCircle(sketch, "E42", {"center": v(-0.15, 0.02) * mm, "radius": 59 * mm});
            skCircle(sketch, "E43", {"center": v(-0.15, 0.02) * mm, "radius": 10 * mm});
            skSolve(sketch);
        }
        {
            var Q0;
            Q0=makeQuery(id+"F3.imprint","IMPRINT",FACE,{"disambiguationData":[TD([[makeQuery(id+"F3.imprint","IMPRINT",EDGE,{"derivedFrom":sQuery(id+"F3.wireOp",EDGE,"E39")}),1.0]])]});
            var Q1;
            Q1=makeQuery(id+"F3.imprint","IMPRINT",FACE,{"disambiguationData":[TD([[makeQuery(id+"F3.imprint","IMPRINT",EDGE,{"derivedFrom":sQuery(id+"F3.wireOp",EDGE,"E42")}),1.0]])]});
            var Q2;
            Q2=qConstructionFilter(qBodyType(qCreatedBy(id+"F3",EDGE),BodyType.WIRE),ConstructionObject.NO);
            extrude(context, id + "F4", {"entities" : qUnion([Q0, Q1]), "operationType" : NewBodyOperationType.REMOVE, "surfaceEntities" : qUnion([Q2]), "oppositeDirection" : true, "depth" : 1 * mm, "offsetDistance" : 25 * mm});
        }
        {
            var Q0;
            Q0=makeQuery(id+"FLAiNYIGUJVPJrN_1.boolean.opBoolean","SPLIT",FACE,{"disambiguationData":[TD([makeQuery(id+"FLAiNYIGUJVPJrN_1.opExtrude","SWEPT_FACE",FACE,{"disambiguationData":[OSD([sQuery(id+"F2.wireOp",EDGE,"E15")])]})])],"derivedFrom":makeQuery(id+"F1.opExtrude","CAP_FACE",FACE,{"disambiguationData":[OSD([sQuery(id+"F0.wireOp",EDGE,"E0"),sQuery(id+"F0.wireOp",EDGE,"E1"),sQuery(id+"F0.wireOp",EDGE,"E3"),sQuery(id+"F0.wireOp",EDGE,"E4"),sQuery(id+"F0.wireOp",EDGE,"E5"),sQuery(id+"F0.wireOp",EDGE,"E6.trimOffspring"),sQuery(id+"F0.wireOp",EDGE,"E7"),sQuery(id+"F0.wireOp",EDGE,"E8.1.0"),sQuery(id+"F0.wireOp",EDGE,"E8.1.1"),sQuery(id+"F0.wireOp",EDGE,"E8.1.2"),sQuery(id+"F0.wireOp",EDGE,"E8.1.3"),sQuery(id+"F0.wireOp",EDGE,"E8.1.4"),sQuery(id+"F0.wireOp",EDGE,"E8.2.0"),sQuery(id+"F0.wireOp",EDGE,"E8.2.1"),sQuery(id+"F0.wireOp",EDGE,"E8.2.2"),sQuery(id+"F0.wireOp",EDGE,"E8.2.3"),sQuery(id+"F0.wireOp",EDGE,"E8.2.4"),sQuery(id+"F0.wireOp",EDGE,"E9.1.3.0"),sQuery(id+"F0.wireOp",EDGE,"E9.3.3.0"),sQuery(id+"F0.wireOp",EDGE,"E9.7.3.0"),sQuery(id+"F0.wireOp",EDGE,"E9.11.3.0"),sQuery(id+"F0.wireOp",EDGE,"E9.14.3.0"),sQuery(id+"F0.wireOp",EDGE,"E9.1.4.0"),sQuery(id+"F0.wireOp",EDGE,"E9.3.4.0"),sQuery(id+"F0.wireOp",EDGE,"E9.7.4.0"),sQuery(id+"F0.wireOp",EDGE,"E9.11.4.0"),sQuery(id+"F0.wireOp",EDGE,"E9.14.4.0"),sQuery(id+"F0.wireOp",EDGE,"E9.1.5.0"),sQuery(id+"F0.wireOp",EDGE,"E9.3.5.0"),sQuery(id+"F0.wireOp",EDGE,"E9.7.5.0"),sQuery(id+"F0.wireOp",EDGE,"E9.11.5.0"),sQuery(id+"F0.wireOp",EDGE,"E9.14.5.0"),sQuery(id+"F0.wireOp",EDGE,"E9.1.6.0"),sQuery(id+"F0.wireOp",EDGE,"E9.3.6.0"),sQuery(id+"F0.wireOp",EDGE,"E9.7.6.0"),sQuery(id+"F0.wireOp",EDGE,"E9.11.6.0"),sQuery(id+"F0.wireOp",EDGE,"E9.14.6.0"),sQuery(id+"F0.wireOp",EDGE,"E9.1.7.0"),sQuery(id+"F0.wireOp",EDGE,"E9.3.7.0"),sQuery(id+"F0.wireOp",EDGE,"E9.7.7.0"),sQuery(id+"F0.wireOp",EDGE,"E9.11.7.0"),sQuery(id+"F0.wireOp",EDGE,"E9.14.7.0"),sQuery(id+"F0.wireOp",EDGE,"E9.1.8.0"),sQuery(id+"F0.wireOp",EDGE,"E9.3.8.0"),sQuery(id+"F0.wireOp",EDGE,"E9.7.8.0"),sQuery(id+"F0.wireOp",EDGE,"E9.11.8.0"),sQuery(id+"F0.wireOp",EDGE,"E9.14.8.0"),sQuery(id+"F0.wireOp",EDGE,"E9.1.9.0"),sQuery(id+"F0.wireOp",EDGE,"E9.3.9.0"),sQuery(id+"F0.wireOp",EDGE,"E9.7.9.0"),sQuery(id+"F0.wireOp",EDGE,"E9.11.9.0"),sQuery(id+"F0.wireOp",EDGE,"E9.14.9.0"),sQuery(id+"F0.wireOp",EDGE,"E9.1.10.0"),sQuery(id+"F0.wireOp",EDGE,"E9.3.10.0"),sQuery(id+"F0.wireOp",EDGE,"E9.7.10.0"),sQuery(id+"F0.wireOp",EDGE,"E9.11.10.0"),sQuery(id+"F0.wireOp",EDGE,"E9.14.10.0"),sQuery(id+"F0.wireOp",EDGE,"E9.1.11.0"),sQuery(id+"F0.wireOp",EDGE,"E9.3.11.0"),sQuery(id+"F0.wireOp",EDGE,"E9.7.11.0"),sQuery(id+"F0.wireOp",EDGE,"E9.11.11.0"),sQuery(id+"F0.wireOp",EDGE,"E9.14.11.0"),sQuery(id+"F0.wireOp",EDGE,"E9.1.12.0"),sQuery(id+"F0.wireOp",EDGE,"E9.3.12.0"),sQuery(id+"F0.wireOp",EDGE,"E9.7.12.0"),sQuery(id+"F0.wireOp",EDGE,"E9.11.12.0"),sQuery(id+"F0.wireOp",EDGE,"E9.14.12.0"),sQuery(id+"F0.wireOp",EDGE,"E9.1.13.0"),sQuery(id+"F0.wireOp",EDGE,"E9.3.13.0"),sQuery(id+"F0.wireOp",EDGE,"E9.7.13.0"),sQuery(id+"F0.wireOp",EDGE,"E9.11.13.0"),sQuery(id+"F0.wireOp",EDGE,"E9.14.13.0"),sQuery(id+"F0.wireOp",EDGE,"E9.1.14.0"),sQuery(id+"F0.wireOp",EDGE,"E9.3.14.0"),sQuery(id+"F0.wireOp",EDGE,"E9.7.14.0"),sQuery(id+"F0.wireOp",EDGE,"E9.11.14.0"),sQuery(id+"F0.wireOp",EDGE,"E9.14.14.0"),sQuery(id+"F0.wireOp",EDGE,"E9.1.15.0"),sQuery(id+"F0.wireOp",EDGE,"E9.3.15.0"),sQuery(id+"F0.wireOp",EDGE,"E9.7.15.0"),sQuery(id+"F0.wireOp",EDGE,"E9.11.15.0"),sQuery(id+"F0.wireOp",EDGE,"E9.14.15.0"),sQuery(id+"F0.wireOp",EDGE,"E9.1.16.0"),sQuery(id+"F0.wireOp",EDGE,"E9.3.16.0"),sQuery(id+"F0.wireOp",EDGE,"E9.7.16.0"),sQuery(id+"F0.wireOp",EDGE,"E9.11.16.0"),sQuery(id+"F0.wireOp",EDGE,"E9.14.16.0"),sQuery(id+"F0.wireOp",EDGE,"E9.1.17.0"),sQuery(id+"F0.wireOp",EDGE,"E9.3.17.0"),sQuery(id+"F0.wireOp",EDGE,"E9.7.17.0"),sQuery(id+"F0.wireOp",EDGE,"E9.11.17.0"),sQuery(id+"F0.wireOp",EDGE,"E9.14.17.0"),sQuery(id+"F0.wireOp",EDGE,"E9.1.18.0"),sQuery(id+"F0.wireOp",EDGE,"E9.3.18.0"),sQuery(id+"F0.wireOp",EDGE,"E9.7.18.0"),sQuery(id+"F0.wireOp",EDGE,"E9.11.18.0"),sQuery(id+"F0.wireOp",EDGE,"E9.14.18.0"),sQuery(id+"F0.wireOp",EDGE,"E9.1.19.0"),sQuery(id+"F0.wireOp",EDGE,"E9.3.19.0"),sQuery(id+"F0.wireOp",EDGE,"E9.7.19.0"),sQuery(id+"F0.wireOp",EDGE,"E9.11.19.0"),sQuery(id+"F0.wireOp",EDGE,"E9.14.19.0"),sQuery(id+"F0.wireOp",EDGE,"E9.1.20.0"),sQuery(id+"F0.wireOp",EDGE,"E9.3.20.0"),sQuery(id+"F0.wireOp",EDGE,"E9.7.20.0"),sQuery(id+"F0.wireOp",EDGE,"E9.11.20.0"),sQuery(id+"F0.wireOp",EDGE,"E9.14.20.0"),sQuery(id+"F0.wireOp",EDGE,"E9.1.21.0"),sQuery(id+"F0.wireOp",EDGE,"E9.3.21.0"),sQuery(id+"F0.wireOp",EDGE,"E9.7.21.0"),sQuery(id+"F0.wireOp",EDGE,"E9.11.21.0"),sQuery(id+"F0.wireOp",EDGE,"E9.14.21.0"),sQuery(id+"F0.wireOp",EDGE,"E9.1.22.0"),sQuery(id+"F0.wireOp",EDGE,"E9.3.22.0"),sQuery(id+"F0.wireOp",EDGE,"E9.7.22.0"),sQuery(id+"F0.wireOp",EDGE,"E9.11.22.0"),sQuery(id+"F0.wireOp",EDGE,"E9.14.22.0"),sQuery(id+"F0.wireOp",EDGE,"E9.1.23.0"),sQuery(id+"F0.wireOp",EDGE,"E9.3.23.0"),sQuery(id+"F0.wireOp",EDGE,"E9.7.23.0"),sQuery(id+"F0.wireOp",EDGE,"E9.11.23.0"),sQuery(id+"F0.wireOp",EDGE,"E9.14.23.0"),sQuery(id+"F0.wireOp",EDGE,"E9.1.24.0"),sQuery(id+"F0.wireOp",EDGE,"E9.3.24.0"),sQuery(id+"F0.wireOp",EDGE,"E9.7.24.0"),sQuery(id+"F0.wireOp",EDGE,"E9.11.24.0"),sQuery(id+"F0.wireOp",EDGE,"E9.14.24.0"),sQuery(id+"F0.wireOp",EDGE,"E9.1.25.0"),sQuery(id+"F0.wireOp",EDGE,"E9.3.25.0"),sQuery(id+"F0.wireOp",EDGE,"E9.7.25.0"),sQuery(id+"F0.wireOp",EDGE,"E9.11.25.0"),sQuery(id+"F0.wireOp",EDGE,"E9.14.25.0"),sQuery(id+"F0.wireOp",EDGE,"E9.1.26.0"),sQuery(id+"F0.wireOp",EDGE,"E9.3.26.0"),sQuery(id+"F0.wireOp",EDGE,"E9.7.26.0"),sQuery(id+"F0.wireOp",EDGE,"E9.11.26.0"),sQuery(id+"F0.wireOp",EDGE,"E9.14.26.0"),sQuery(id+"F0.wireOp",EDGE,"E9.1.27.0"),sQuery(id+"F0.wireOp",EDGE,"E9.3.27.0"),sQuery(id+"F0.wireOp",EDGE,"E9.7.27.0"),sQuery(id+"F0.wireOp",EDGE,"E9.11.27.0"),sQuery(id+"F0.wireOp",EDGE,"E9.14.27.0"),sQuery(id+"F0.wireOp",EDGE,"E9.1.28.0"),sQuery(id+"F0.wireOp",EDGE,"E9.3.28.0"),sQuery(id+"F0.wireOp",EDGE,"E9.7.28.0"),sQuery(id+"F0.wireOp",EDGE,"E9.11.28.0"),sQuery(id+"F0.wireOp",EDGE,"E9.14.28.0"),sQuery(id+"F0.wireOp",EDGE,"E9.1.29.0"),sQuery(id+"F0.wireOp",EDGE,"E9.3.29.0"),sQuery(id+"F0.wireOp",EDGE,"E9.7.29.0"),sQuery(id+"F0.wireOp",EDGE,"E9.11.29.0"),sQuery(id+"F0.wireOp",EDGE,"E9.14.29.0"),sQuery(id+"F0.wireOp",EDGE,"E9.1.30.0"),sQuery(id+"F0.wireOp",EDGE,"E9.3.30.0"),sQuery(id+"F0.wireOp",EDGE,"E9.7.30.0"),sQuery(id+"F0.wireOp",EDGE,"E9.11.30.0"),sQuery(id+"F0.wireOp",EDGE,"E9.14.30.0"),sQuery(id+"F0.wireOp",EDGE,"E9.1.31.0"),sQuery(id+"F0.wireOp",EDGE,"E9.3.31.0"),sQuery(id+"F0.wireOp",EDGE,"E9.7.31.0"),sQuery(id+"F0.wireOp",EDGE,"E9.11.31.0"),sQuery(id+"F0.wireOp",EDGE,"E9.14.31.0"),sQuery(id+"F0.wireOp",EDGE,"E9.1.32.0"),sQuery(id+"F0.wireOp",EDGE,"E9.3.32.0"),sQuery(id+"F0.wireOp",EDGE,"E9.7.32.0"),sQuery(id+"F0.wireOp",EDGE,"E9.11.32.0"),sQuery(id+"F0.wireOp",EDGE,"E9.14.32.0"),sQuery(id+"F0.wireOp",EDGE,"E9.1.33.0"),sQuery(id+"F0.wireOp",EDGE,"E9.3.33.0"),sQuery(id+"F0.wireOp",EDGE,"E9.7.33.0"),sQuery(id+"F0.wireOp",EDGE,"E9.11.33.0"),sQuery(id+"F0.wireOp",EDGE,"E9.14.33.0"),sQuery(id+"F0.wireOp",EDGE,"E9.1.34.0"),sQuery(id+"F0.wireOp",EDGE,"E9.3.34.0"),sQuery(id+"F0.wireOp",EDGE,"E9.7.34.0"),sQuery(id+"F0.wireOp",EDGE,"E9.11.34.0"),sQuery(id+"F0.wireOp",EDGE,"E9.14.34.0"),sQuery(id+"F0.wireOp",EDGE,"E9.1.35.0"),sQuery(id+"F0.wireOp",EDGE,"E9.3.35.0"),sQuery(id+"F0.wireOp",EDGE,"E9.7.35.0"),sQuery(id+"F0.wireOp",EDGE,"E9.11.35.0"),sQuery(id+"F0.wireOp",EDGE,"E9.14.35.0"),sQuery(id+"F0.wireOp",EDGE,"E9.1.36.0"),sQuery(id+"F0.wireOp",EDGE,"E9.3.36.0"),sQuery(id+"F0.wireOp",EDGE,"E9.7.36.0"),sQuery(id+"F0.wireOp",EDGE,"E9.11.36.0"),sQuery(id+"F0.wireOp",EDGE,"E9.14.36.0"),sQuery(id+"F0.wireOp",EDGE,"E9.1.37.0"),sQuery(id+"F0.wireOp",EDGE,"E9.3.37.0"),sQuery(id+"F0.wireOp",EDGE,"E9.7.37.0"),sQuery(id+"F0.wireOp",EDGE,"E9.11.37.0"),sQuery(id+"F0.wireOp",EDGE,"E9.14.37.0"),sQuery(id+"F0.wireOp",EDGE,"E9.1.38.0"),sQuery(id+"F0.wireOp",EDGE,"E9.3.38.0"),sQuery(id+"F0.wireOp",EDGE,"E9.7.38.0"),sQuery(id+"F0.wireOp",EDGE,"E9.11.38.0"),sQuery(id+"F0.wireOp",EDGE,"E9.14.38.0"),sQuery(id+"F0.wireOp",EDGE,"E9.1.39.0"),sQuery(id+"F0.wireOp",EDGE,"E9.3.39.0"),sQuery(id+"F0.wireOp",EDGE,"E9.7.39.0"),sQuery(id+"F0.wireOp",EDGE,"E9.11.39.0"),sQuery(id+"F0.wireOp",EDGE,"E9.14.39.0"),sQuery(id+"F0.wireOp",EDGE,"E9.1.40.0"),sQuery(id+"F0.wireOp",EDGE,"E9.3.40.0"),sQuery(id+"F0.wireOp",EDGE,"E9.7.40.0"),sQuery(id+"F0.wireOp",EDGE,"E9.11.40.0"),sQuery(id+"F0.wireOp",EDGE,"E9.14.40.0"),sQuery(id+"F0.wireOp",EDGE,"E9.1.41.0"),sQuery(id+"F0.wireOp",EDGE,"E9.3.41.0"),sQuery(id+"F0.wireOp",EDGE,"E9.7.41.0"),sQuery(id+"F0.wireOp",EDGE,"E9.11.41.0"),sQuery(id+"F0.wireOp",EDGE,"E9.14.41.0"),sQuery(id+"F0.wireOp",EDGE,"E9.1.42.0"),sQuery(id+"F0.wireOp",EDGE,"E9.3.42.0"),sQuery(id+"F0.wireOp",EDGE,"E9.7.42.0"),sQuery(id+"F0.wireOp",EDGE,"E9.11.42.0"),sQuery(id+"F0.wireOp",EDGE,"E9.14.42.0"),sQuery(id+"F0.wireOp",EDGE,"E9.1.43.0"),sQuery(id+"F0.wireOp",EDGE,"E9.3.43.0"),sQuery(id+"F0.wireOp",EDGE,"E9.7.43.0"),sQuery(id+"F0.wireOp",EDGE,"E9.11.43.0"),sQuery(id+"F0.wireOp",EDGE,"E9.14.43.0"),sQuery(id+"F0.wireOp",EDGE,"E9.1.44.0"),sQuery(id+"F0.wireOp",EDGE,"E9.3.44.0"),sQuery(id+"F0.wireOp",EDGE,"E9.7.44.0"),sQuery(id+"F0.wireOp",EDGE,"E9.11.44.0"),sQuery(id+"F0.wireOp",EDGE,"E9.14.44.0"),sQuery(id+"F0.wireOp",EDGE,"E9.1.45.0"),sQuery(id+"F0.wireOp",EDGE,"E9.3.45.0"),sQuery(id+"F0.wireOp",EDGE,"E9.7.45.0"),sQuery(id+"F0.wireOp",EDGE,"E9.11.45.0"),sQuery(id+"F0.wireOp",EDGE,"E9.14.45.0"),sQuery(id+"F0.wireOp",EDGE,"E9.1.46.0"),sQuery(id+"F0.wireOp",EDGE,"E9.3.46.0"),sQuery(id+"F0.wireOp",EDGE,"E9.7.46.0"),sQuery(id+"F0.wireOp",EDGE,"E9.11.46.0"),sQuery(id+"F0.wireOp",EDGE,"E9.14.46.0"),sQuery(id+"F0.wireOp",EDGE,"E9.1.47.0"),sQuery(id+"F0.wireOp",EDGE,"E9.3.47.0"),sQuery(id+"F0.wireOp",EDGE,"E9.7.47.0"),sQuery(id+"F0.wireOp",EDGE,"E9.11.47.0"),sQuery(id+"F0.wireOp",EDGE,"E9.14.47.0"),sQuery(id+"F0.wireOp",EDGE,"E9.1.48.0"),sQuery(id+"F0.wireOp",EDGE,"E9.3.48.0"),sQuery(id+"F0.wireOp",EDGE,"E9.7.48.0"),sQuery(id+"F0.wireOp",EDGE,"E9.11.48.0"),sQuery(id+"F0.wireOp",EDGE,"E9.14.48.0"),sQuery(id+"F0.wireOp",EDGE,"E9.1.49.0"),sQuery(id+"F0.wireOp",EDGE,"E9.3.49.0"),sQuery(id+"F0.wireOp",EDGE,"E9.7.49.0"),sQuery(id+"F0.wireOp",EDGE,"E9.11.49.0"),sQuery(id+"F0.wireOp",EDGE,"E9.14.49.0"),sQuery(id+"F0.wireOp",EDGE,"E9.1.50.0"),sQuery(id+"F0.wireOp",EDGE,"E9.3.50.0"),sQuery(id+"F0.wireOp",EDGE,"E9.7.50.0"),sQuery(id+"F0.wireOp",EDGE,"E9.11.50.0"),sQuery(id+"F0.wireOp",EDGE,"E9.14.50.0"),sQuery(id+"F0.wireOp",EDGE,"E9.1.51.0"),sQuery(id+"F0.wireOp",EDGE,"E9.3.51.0"),sQuery(id+"F0.wireOp",EDGE,"E9.7.51.0"),sQuery(id+"F0.wireOp",EDGE,"E9.11.51.0"),sQuery(id+"F0.wireOp",EDGE,"E9.14.51.0"),sQuery(id+"F0.wireOp",EDGE,"E9.1.52.0"),sQuery(id+"F0.wireOp",EDGE,"E9.3.52.0"),sQuery(id+"F0.wireOp",EDGE,"E9.7.52.0"),sQuery(id+"F0.wireOp",EDGE,"E9.11.52.0"),sQuery(id+"F0.wireOp",EDGE,"E9.14.52.0"),sQuery(id+"F0.wireOp",EDGE,"E9.1.53.0"),sQuery(id+"F0.wireOp",EDGE,"E9.3.53.0"),sQuery(id+"F0.wireOp",EDGE,"E9.7.53.0"),sQuery(id+"F0.wireOp",EDGE,"E9.11.53.0"),sQuery(id+"F0.wireOp",EDGE,"E9.14.53.0"),sQuery(id+"F0.wireOp",EDGE,"E9.1.54.0"),sQuery(id+"F0.wireOp",EDGE,"E9.3.54.0"),sQuery(id+"F0.wireOp",EDGE,"E9.7.54.0"),sQuery(id+"F0.wireOp",EDGE,"E9.11.54.0"),sQuery(id+"F0.wireOp",EDGE,"E9.14.54.0"),sQuery(id+"F0.wireOp",EDGE,"E9.1.55.0"),sQuery(id+"F0.wireOp",EDGE,"E9.3.55.0"),sQuery(id+"F0.wireOp",EDGE,"E9.7.55.0"),sQuery(id+"F0.wireOp",EDGE,"E9.11.55.0"),sQuery(id+"F0.wireOp",EDGE,"E9.14.55.0"),sQuery(id+"F0.wireOp",EDGE,"E9.1.56.0"),sQuery(id+"F0.wireOp",EDGE,"E9.3.56.0"),sQuery(id+"F0.wireOp",EDGE,"E9.7.56.0"),sQuery(id+"F0.wireOp",EDGE,"E9.11.56.0"),sQuery(id+"F0.wireOp",EDGE,"E9.14.56.0"),sQuery(id+"F0.wireOp",EDGE,"E9.1.57.0"),sQuery(id+"F0.wireOp",EDGE,"E9.3.57.0"),sQuery(id+"F0.wireOp",EDGE,"E9.7.57.0"),sQuery(id+"F0.wireOp",EDGE,"E9.11.57.0"),sQuery(id+"F0.wireOp",EDGE,"E9.14.57.0"),sQuery(id+"F0.wireOp",EDGE,"E9.1.58.0"),sQuery(id+"F0.wireOp",EDGE,"E9.3.58.0"),sQuery(id+"F0.wireOp",EDGE,"E9.7.58.0"),sQuery(id+"F0.wireOp",EDGE,"E9.11.58.0"),sQuery(id+"F0.wireOp",EDGE,"E9.14.58.0"),sQuery(id+"F0.wireOp",EDGE,"E9.1.59.0"),sQuery(id+"F0.wireOp",EDGE,"E9.3.59.0"),sQuery(id+"F0.wireOp",EDGE,"E9.7.59.0"),sQuery(id+"F0.wireOp",EDGE,"E9.11.59.0"),sQuery(id+"F0.wireOp",EDGE,"E9.14.59.0")])],"isStart":false})});
            extrude(context, id + "F5", {"entities" : qUnion([Q0]), "operationType" : NewBodyOperationType.REMOVE, "oppositeDirection" : true, "depth" : 1 * mm, "offsetDistance" : 25 * mm});
        }
        {
            var Q0;
            Q0=makeQuery(id+"F2.imprint","IMPRINT",FACE,{"disambiguationData":[TD([[makeQuery(id+"F2.imprint","IMPRINT",EDGE,{"derivedFrom":sQuery(id+"F2.wireOp",EDGE,"E19")}),1.0]])]});
            var Q1;
            Q1=makeQuery(id+"F2.imprint","IMPRINT",FACE,{"disambiguationData":[TD([[makeQuery(id+"F2.imprint","IMPRINT",EDGE,{"derivedFrom":sQuery(id+"F2.wireOp",EDGE,"E23")}),1.0]])]});
            var Q2;
            Q2=makeQuery(id+"F2.imprint","IMPRINT",FACE,{"disambiguationData":[TD([[makeQuery(id+"F2.imprint","IMPRINT",EDGE,{"derivedFrom":sQuery(id+"F2.wireOp",EDGE,"E22.0")}),-1.0]])]});
            var Q3;
            Q3=makeQuery(id+"F2.imprint","IMPRINT",FACE,{"disambiguationData":[TD([[makeQuery(id+"F2.imprint","IMPRINT",EDGE,{"derivedFrom":sQuery(id+"F2.wireOp",EDGE,"E20.0")}),-1.0]])]});
            extrude(context, id + "F6", {"entities" : qUnion([Q0, Q1, Q2, Q3]), "operationType" : NewBodyOperationType.REMOVE, "endBound" : BoundingType.THROUGH_ALL, "oppositeDirection" : true, "depth" : 25 * mm, "offsetDistance" : 25 * mm});
        }
        {
            var Q0;
            Q0=makeQuery(id+"F5.boolean.opBoolean","COPY",FACE,{"derivedFrom":makeQuery(id+"F5.opExtrude","CAP_FACE",FACE,{"disambiguationData":[OSD([sQuery(id+"F0.wireOp",EDGE,"E0"),sQuery(id+"F0.wireOp",EDGE,"E1"),sQuery(id+"F0.wireOp",EDGE,"E3"),sQuery(id+"F0.wireOp",EDGE,"E4"),sQuery(id+"F0.wireOp",EDGE,"E5"),sQuery(id+"F0.wireOp",EDGE,"E6.trimOffspring"),sQuery(id+"F0.wireOp",EDGE,"E7"),sQuery(id+"F0.wireOp",EDGE,"E8.1.0"),sQuery(id+"F0.wireOp",EDGE,"E8.1.1"),sQuery(id+"F0.wireOp",EDGE,"E8.1.2"),sQuery(id+"F0.wireOp",EDGE,"E8.1.3"),sQuery(id+"F0.wireOp",EDGE,"E8.1.4"),sQuery(id+"F0.wireOp",EDGE,"E8.2.0"),sQuery(id+"F0.wireOp",EDGE,"E8.2.1"),sQuery(id+"F0.wireOp",EDGE,"E8.2.2"),sQuery(id+"F0.wireOp",EDGE,"E8.2.3"),sQuery(id+"F0.wireOp",EDGE,"E8.2.4"),sQuery(id+"F0.wireOp",EDGE,"E9.1.3.0"),sQuery(id+"F0.wireOp",EDGE,"E9.3.3.0"),sQuery(id+"F0.wireOp",EDGE,"E9.7.3.0"),sQuery(id+"F0.wireOp",EDGE,"E9.11.3.0"),sQuery(id+"F0.wireOp",EDGE,"E9.14.3.0"),sQuery(id+"F0.wireOp",EDGE,"E9.1.4.0"),sQuery(id+"F0.wireOp",EDGE,"E9.3.4.0"),sQuery(id+"F0.wireOp",EDGE,"E9.7.4.0"),sQuery(id+"F0.wireOp",EDGE,"E9.11.4.0"),sQuery(id+"F0.wireOp",EDGE,"E9.14.4.0"),sQuery(id+"F0.wireOp",EDGE,"E9.1.5.0"),sQuery(id+"F0.wireOp",EDGE,"E9.3.5.0"),sQuery(id+"F0.wireOp",EDGE,"E9.7.5.0"),sQuery(id+"F0.wireOp",EDGE,"E9.11.5.0"),sQuery(id+"F0.wireOp",EDGE,"E9.14.5.0"),sQuery(id+"F0.wireOp",EDGE,"E9.1.6.0"),sQuery(id+"F0.wireOp",EDGE,"E9.3.6.0"),sQuery(id+"F0.wireOp",EDGE,"E9.7.6.0"),sQuery(id+"F0.wireOp",EDGE,"E9.11.6.0"),sQuery(id+"F0.wireOp",EDGE,"E9.14.6.0"),sQuery(id+"F0.wireOp",EDGE,"E9.1.7.0"),sQuery(id+"F0.wireOp",EDGE,"E9.3.7.0"),sQuery(id+"F0.wireOp",EDGE,"E9.7.7.0"),sQuery(id+"F0.wireOp",EDGE,"E9.11.7.0"),sQuery(id+"F0.wireOp",EDGE,"E9.14.7.0"),sQuery(id+"F0.wireOp",EDGE,"E9.1.8.0"),sQuery(id+"F0.wireOp",EDGE,"E9.3.8.0"),sQuery(id+"F0.wireOp",EDGE,"E9.7.8.0"),sQuery(id+"F0.wireOp",EDGE,"E9.11.8.0"),sQuery(id+"F0.wireOp",EDGE,"E9.14.8.0"),sQuery(id+"F0.wireOp",EDGE,"E9.1.9.0"),sQuery(id+"F0.wireOp",EDGE,"E9.3.9.0"),sQuery(id+"F0.wireOp",EDGE,"E9.7.9.0"),sQuery(id+"F0.wireOp",EDGE,"E9.11.9.0"),sQuery(id+"F0.wireOp",EDGE,"E9.14.9.0"),sQuery(id+"F0.wireOp",EDGE,"E9.1.10.0"),sQuery(id+"F0.wireOp",EDGE,"E9.3.10.0"),sQuery(id+"F0.wireOp",EDGE,"E9.7.10.0"),sQuery(id+"F0.wireOp",EDGE,"E9.11.10.0"),sQuery(id+"F0.wireOp",EDGE,"E9.14.10.0"),sQuery(id+"F0.wireOp",EDGE,"E9.1.11.0"),sQuery(id+"F0.wireOp",EDGE,"E9.3.11.0"),sQuery(id+"F0.wireOp",EDGE,"E9.7.11.0"),sQuery(id+"F0.wireOp",EDGE,"E9.11.11.0"),sQuery(id+"F0.wireOp",EDGE,"E9.14.11.0"),sQuery(id+"F0.wireOp",EDGE,"E9.1.12.0"),sQuery(id+"F0.wireOp",EDGE,"E9.3.12.0"),sQuery(id+"F0.wireOp",EDGE,"E9.7.12.0"),sQuery(id+"F0.wireOp",EDGE,"E9.11.12.0"),sQuery(id+"F0.wireOp",EDGE,"E9.14.12.0"),sQuery(id+"F0.wireOp",EDGE,"E9.1.13.0"),sQuery(id+"F0.wireOp",EDGE,"E9.3.13.0"),sQuery(id+"F0.wireOp",EDGE,"E9.7.13.0"),sQuery(id+"F0.wireOp",EDGE,"E9.11.13.0"),sQuery(id+"F0.wireOp",EDGE,"E9.14.13.0"),sQuery(id+"F0.wireOp",EDGE,"E9.1.14.0"),sQuery(id+"F0.wireOp",EDGE,"E9.3.14.0"),sQuery(id+"F0.wireOp",EDGE,"E9.7.14.0"),sQuery(id+"F0.wireOp",EDGE,"E9.11.14.0"),sQuery(id+"F0.wireOp",EDGE,"E9.14.14.0"),sQuery(id+"F0.wireOp",EDGE,"E9.1.15.0"),sQuery(id+"F0.wireOp",EDGE,"E9.3.15.0"),sQuery(id+"F0.wireOp",EDGE,"E9.7.15.0"),sQuery(id+"F0.wireOp",EDGE,"E9.11.15.0"),sQuery(id+"F0.wireOp",EDGE,"E9.14.15.0"),sQuery(id+"F0.wireOp",EDGE,"E9.1.16.0"),sQuery(id+"F0.wireOp",EDGE,"E9.3.16.0"),sQuery(id+"F0.wireOp",EDGE,"E9.7.16.0"),sQuery(id+"F0.wireOp",EDGE,"E9.11.16.0"),sQuery(id+"F0.wireOp",EDGE,"E9.14.16.0"),sQuery(id+"F0.wireOp",EDGE,"E9.1.17.0"),sQuery(id+"F0.wireOp",EDGE,"E9.3.17.0"),sQuery(id+"F0.wireOp",EDGE,"E9.7.17.0"),sQuery(id+"F0.wireOp",EDGE,"E9.11.17.0"),sQuery(id+"F0.wireOp",EDGE,"E9.14.17.0"),sQuery(id+"F0.wireOp",EDGE,"E9.1.18.0"),sQuery(id+"F0.wireOp",EDGE,"E9.3.18.0"),sQuery(id+"F0.wireOp",EDGE,"E9.7.18.0"),sQuery(id+"F0.wireOp",EDGE,"E9.11.18.0"),sQuery(id+"F0.wireOp",EDGE,"E9.14.18.0"),sQuery(id+"F0.wireOp",EDGE,"E9.1.19.0"),sQuery(id+"F0.wireOp",EDGE,"E9.3.19.0"),sQuery(id+"F0.wireOp",EDGE,"E9.7.19.0"),sQuery(id+"F0.wireOp",EDGE,"E9.11.19.0"),sQuery(id+"F0.wireOp",EDGE,"E9.14.19.0"),sQuery(id+"F0.wireOp",EDGE,"E9.1.20.0"),sQuery(id+"F0.wireOp",EDGE,"E9.3.20.0"),sQuery(id+"F0.wireOp",EDGE,"E9.7.20.0"),sQuery(id+"F0.wireOp",EDGE,"E9.11.20.0"),sQuery(id+"F0.wireOp",EDGE,"E9.14.20.0"),sQuery(id+"F0.wireOp",EDGE,"E9.1.21.0"),sQuery(id+"F0.wireOp",EDGE,"E9.3.21.0"),sQuery(id+"F0.wireOp",EDGE,"E9.7.21.0"),sQuery(id+"F0.wireOp",EDGE,"E9.11.21.0"),sQuery(id+"F0.wireOp",EDGE,"E9.14.21.0"),sQuery(id+"F0.wireOp",EDGE,"E9.1.22.0"),sQuery(id+"F0.wireOp",EDGE,"E9.3.22.0"),sQuery(id+"F0.wireOp",EDGE,"E9.7.22.0"),sQuery(id+"F0.wireOp",EDGE,"E9.11.22.0"),sQuery(id+"F0.wireOp",EDGE,"E9.14.22.0"),sQuery(id+"F0.wireOp",EDGE,"E9.1.23.0"),sQuery(id+"F0.wireOp",EDGE,"E9.3.23.0"),sQuery(id+"F0.wireOp",EDGE,"E9.7.23.0"),sQuery(id+"F0.wireOp",EDGE,"E9.11.23.0"),sQuery(id+"F0.wireOp",EDGE,"E9.14.23.0"),sQuery(id+"F0.wireOp",EDGE,"E9.1.24.0"),sQuery(id+"F0.wireOp",EDGE,"E9.3.24.0"),sQuery(id+"F0.wireOp",EDGE,"E9.7.24.0"),sQuery(id+"F0.wireOp",EDGE,"E9.11.24.0"),sQuery(id+"F0.wireOp",EDGE,"E9.14.24.0"),sQuery(id+"F0.wireOp",EDGE,"E9.1.25.0"),sQuery(id+"F0.wireOp",EDGE,"E9.3.25.0"),sQuery(id+"F0.wireOp",EDGE,"E9.7.25.0"),sQuery(id+"F0.wireOp",EDGE,"E9.11.25.0"),sQuery(id+"F0.wireOp",EDGE,"E9.14.25.0"),sQuery(id+"F0.wireOp",EDGE,"E9.1.26.0"),sQuery(id+"F0.wireOp",EDGE,"E9.3.26.0"),sQuery(id+"F0.wireOp",EDGE,"E9.7.26.0"),sQuery(id+"F0.wireOp",EDGE,"E9.11.26.0"),sQuery(id+"F0.wireOp",EDGE,"E9.14.26.0"),sQuery(id+"F0.wireOp",EDGE,"E9.1.27.0"),sQuery(id+"F0.wireOp",EDGE,"E9.3.27.0"),sQuery(id+"F0.wireOp",EDGE,"E9.7.27.0"),sQuery(id+"F0.wireOp",EDGE,"E9.11.27.0"),sQuery(id+"F0.wireOp",EDGE,"E9.14.27.0"),sQuery(id+"F0.wireOp",EDGE,"E9.1.28.0"),sQuery(id+"F0.wireOp",EDGE,"E9.3.28.0"),sQuery(id+"F0.wireOp",EDGE,"E9.7.28.0"),sQuery(id+"F0.wireOp",EDGE,"E9.11.28.0"),sQuery(id+"F0.wireOp",EDGE,"E9.14.28.0"),sQuery(id+"F0.wireOp",EDGE,"E9.1.29.0"),sQuery(id+"F0.wireOp",EDGE,"E9.3.29.0"),sQuery(id+"F0.wireOp",EDGE,"E9.7.29.0"),sQuery(id+"F0.wireOp",EDGE,"E9.11.29.0"),sQuery(id+"F0.wireOp",EDGE,"E9.14.29.0"),sQuery(id+"F0.wireOp",EDGE,"E9.1.30.0"),sQuery(id+"F0.wireOp",EDGE,"E9.3.30.0"),sQuery(id+"F0.wireOp",EDGE,"E9.7.30.0"),sQuery(id+"F0.wireOp",EDGE,"E9.11.30.0"),sQuery(id+"F0.wireOp",EDGE,"E9.14.30.0"),sQuery(id+"F0.wireOp",EDGE,"E9.1.31.0"),sQuery(id+"F0.wireOp",EDGE,"E9.3.31.0"),sQuery(id+"F0.wireOp",EDGE,"E9.7.31.0"),sQuery(id+"F0.wireOp",EDGE,"E9.11.31.0"),sQuery(id+"F0.wireOp",EDGE,"E9.14.31.0"),sQuery(id+"F0.wireOp",EDGE,"E9.1.32.0"),sQuery(id+"F0.wireOp",EDGE,"E9.3.32.0"),sQuery(id+"F0.wireOp",EDGE,"E9.7.32.0"),sQuery(id+"F0.wireOp",EDGE,"E9.11.32.0"),sQuery(id+"F0.wireOp",EDGE,"E9.14.32.0"),sQuery(id+"F0.wireOp",EDGE,"E9.1.33.0"),sQuery(id+"F0.wireOp",EDGE,"E9.3.33.0"),sQuery(id+"F0.wireOp",EDGE,"E9.7.33.0"),sQuery(id+"F0.wireOp",EDGE,"E9.11.33.0"),sQuery(id+"F0.wireOp",EDGE,"E9.14.33.0"),sQuery(id+"F0.wireOp",EDGE,"E9.1.34.0"),sQuery(id+"F0.wireOp",EDGE,"E9.3.34.0"),sQuery(id+"F0.wireOp",EDGE,"E9.7.34.0"),sQuery(id+"F0.wireOp",EDGE,"E9.11.34.0"),sQuery(id+"F0.wireOp",EDGE,"E9.14.34.0"),sQuery(id+"F0.wireOp",EDGE,"E9.1.35.0"),sQuery(id+"F0.wireOp",EDGE,"E9.3.35.0"),sQuery(id+"F0.wireOp",EDGE,"E9.7.35.0"),sQuery(id+"F0.wireOp",EDGE,"E9.11.35.0"),sQuery(id+"F0.wireOp",EDGE,"E9.14.35.0"),sQuery(id+"F0.wireOp",EDGE,"E9.1.36.0"),sQuery(id+"F0.wireOp",EDGE,"E9.3.36.0"),sQuery(id+"F0.wireOp",EDGE,"E9.7.36.0"),sQuery(id+"F0.wireOp",EDGE,"E9.11.36.0"),sQuery(id+"F0.wireOp",EDGE,"E9.14.36.0"),sQuery(id+"F0.wireOp",EDGE,"E9.1.37.0"),sQuery(id+"F0.wireOp",EDGE,"E9.3.37.0"),sQuery(id+"F0.wireOp",EDGE,"E9.7.37.0"),sQuery(id+"F0.wireOp",EDGE,"E9.11.37.0"),sQuery(id+"F0.wireOp",EDGE,"E9.14.37.0"),sQuery(id+"F0.wireOp",EDGE,"E9.1.38.0"),sQuery(id+"F0.wireOp",EDGE,"E9.3.38.0"),sQuery(id+"F0.wireOp",EDGE,"E9.7.38.0"),sQuery(id+"F0.wireOp",EDGE,"E9.11.38.0"),sQuery(id+"F0.wireOp",EDGE,"E9.14.38.0"),sQuery(id+"F0.wireOp",EDGE,"E9.1.39.0"),sQuery(id+"F0.wireOp",EDGE,"E9.3.39.0"),sQuery(id+"F0.wireOp",EDGE,"E9.7.39.0"),sQuery(id+"F0.wireOp",EDGE,"E9.11.39.0"),sQuery(id+"F0.wireOp",EDGE,"E9.14.39.0"),sQuery(id+"F0.wireOp",EDGE,"E9.1.40.0"),sQuery(id+"F0.wireOp",EDGE,"E9.3.40.0"),sQuery(id+"F0.wireOp",EDGE,"E9.7.40.0"),sQuery(id+"F0.wireOp",EDGE,"E9.11.40.0"),sQuery(id+"F0.wireOp",EDGE,"E9.14.40.0"),sQuery(id+"F0.wireOp",EDGE,"E9.1.41.0"),sQuery(id+"F0.wireOp",EDGE,"E9.3.41.0"),sQuery(id+"F0.wireOp",EDGE,"E9.7.41.0"),sQuery(id+"F0.wireOp",EDGE,"E9.11.41.0"),sQuery(id+"F0.wireOp",EDGE,"E9.14.41.0"),sQuery(id+"F0.wireOp",EDGE,"E9.1.42.0"),sQuery(id+"F0.wireOp",EDGE,"E9.3.42.0"),sQuery(id+"F0.wireOp",EDGE,"E9.7.42.0"),sQuery(id+"F0.wireOp",EDGE,"E9.11.42.0"),sQuery(id+"F0.wireOp",EDGE,"E9.14.42.0"),sQuery(id+"F0.wireOp",EDGE,"E9.1.43.0"),sQuery(id+"F0.wireOp",EDGE,"E9.3.43.0"),sQuery(id+"F0.wireOp",EDGE,"E9.7.43.0"),sQuery(id+"F0.wireOp",EDGE,"E9.11.43.0"),sQuery(id+"F0.wireOp",EDGE,"E9.14.43.0"),sQuery(id+"F0.wireOp",EDGE,"E9.1.44.0"),sQuery(id+"F0.wireOp",EDGE,"E9.3.44.0"),sQuery(id+"F0.wireOp",EDGE,"E9.7.44.0"),sQuery(id+"F0.wireOp",EDGE,"E9.11.44.0"),sQuery(id+"F0.wireOp",EDGE,"E9.14.44.0"),sQuery(id+"F0.wireOp",EDGE,"E9.1.45.0"),sQuery(id+"F0.wireOp",EDGE,"E9.3.45.0"),sQuery(id+"F0.wireOp",EDGE,"E9.7.45.0"),sQuery(id+"F0.wireOp",EDGE,"E9.11.45.0"),sQuery(id+"F0.wireOp",EDGE,"E9.14.45.0"),sQuery(id+"F0.wireOp",EDGE,"E9.1.46.0"),sQuery(id+"F0.wireOp",EDGE,"E9.3.46.0"),sQuery(id+"F0.wireOp",EDGE,"E9.7.46.0"),sQuery(id+"F0.wireOp",EDGE,"E9.11.46.0"),sQuery(id+"F0.wireOp",EDGE,"E9.14.46.0"),sQuery(id+"F0.wireOp",EDGE,"E9.1.47.0"),sQuery(id+"F0.wireOp",EDGE,"E9.3.47.0"),sQuery(id+"F0.wireOp",EDGE,"E9.7.47.0"),sQuery(id+"F0.wireOp",EDGE,"E9.11.47.0"),sQuery(id+"F0.wireOp",EDGE,"E9.14.47.0"),sQuery(id+"F0.wireOp",EDGE,"E9.1.48.0"),sQuery(id+"F0.wireOp",EDGE,"E9.3.48.0"),sQuery(id+"F0.wireOp",EDGE,"E9.7.48.0"),sQuery(id+"F0.wireOp",EDGE,"E9.11.48.0"),sQuery(id+"F0.wireOp",EDGE,"E9.14.48.0"),sQuery(id+"F0.wireOp",EDGE,"E9.1.49.0"),sQuery(id+"F0.wireOp",EDGE,"E9.3.49.0"),sQuery(id+"F0.wireOp",EDGE,"E9.7.49.0"),sQuery(id+"F0.wireOp",EDGE,"E9.11.49.0"),sQuery(id+"F0.wireOp",EDGE,"E9.14.49.0"),sQuery(id+"F0.wireOp",EDGE,"E9.1.50.0"),sQuery(id+"F0.wireOp",EDGE,"E9.3.50.0"),sQuery(id+"F0.wireOp",EDGE,"E9.7.50.0"),sQuery(id+"F0.wireOp",EDGE,"E9.11.50.0"),sQuery(id+"F0.wireOp",EDGE,"E9.14.50.0"),sQuery(id+"F0.wireOp",EDGE,"E9.1.51.0"),sQuery(id+"F0.wireOp",EDGE,"E9.3.51.0"),sQuery(id+"F0.wireOp",EDGE,"E9.7.51.0"),sQuery(id+"F0.wireOp",EDGE,"E9.11.51.0"),sQuery(id+"F0.wireOp",EDGE,"E9.14.51.0"),sQuery(id+"F0.wireOp",EDGE,"E9.1.52.0"),sQuery(id+"F0.wireOp",EDGE,"E9.3.52.0"),sQuery(id+"F0.wireOp",EDGE,"E9.7.52.0"),sQuery(id+"F0.wireOp",EDGE,"E9.11.52.0"),sQuery(id+"F0.wireOp",EDGE,"E9.14.52.0"),sQuery(id+"F0.wireOp",EDGE,"E9.1.53.0"),sQuery(id+"F0.wireOp",EDGE,"E9.3.53.0"),sQuery(id+"F0.wireOp",EDGE,"E9.7.53.0"),sQuery(id+"F0.wireOp",EDGE,"E9.11.53.0"),sQuery(id+"F0.wireOp",EDGE,"E9.14.53.0"),sQuery(id+"F0.wireOp",EDGE,"E9.1.54.0"),sQuery(id+"F0.wireOp",EDGE,"E9.3.54.0"),sQuery(id+"F0.wireOp",EDGE,"E9.7.54.0"),sQuery(id+"F0.wireOp",EDGE,"E9.11.54.0"),sQuery(id+"F0.wireOp",EDGE,"E9.14.54.0"),sQuery(id+"F0.wireOp",EDGE,"E9.1.55.0"),sQuery(id+"F0.wireOp",EDGE,"E9.3.55.0"),sQuery(id+"F0.wireOp",EDGE,"E9.7.55.0"),sQuery(id+"F0.wireOp",EDGE,"E9.11.55.0"),sQuery(id+"F0.wireOp",EDGE,"E9.14.55.0"),sQuery(id+"F0.wireOp",EDGE,"E9.1.56.0"),sQuery(id+"F0.wireOp",EDGE,"E9.3.56.0"),sQuery(id+"F0.wireOp",EDGE,"E9.7.56.0"),sQuery(id+"F0.wireOp",EDGE,"E9.11.56.0"),sQuery(id+"F0.wireOp",EDGE,"E9.14.56.0"),sQuery(id+"F0.wireOp",EDGE,"E9.1.57.0"),sQuery(id+"F0.wireOp",EDGE,"E9.3.57.0"),sQuery(id+"F0.wireOp",EDGE,"E9.7.57.0"),sQuery(id+"F0.wireOp",EDGE,"E9.11.57.0"),sQuery(id+"F0.wireOp",EDGE,"E9.14.57.0"),sQuery(id+"F0.wireOp",EDGE,"E9.1.58.0"),sQuery(id+"F0.wireOp",EDGE,"E9.3.58.0"),sQuery(id+"F0.wireOp",EDGE,"E9.7.58.0"),sQuery(id+"F0.wireOp",EDGE,"E9.11.58.0"),sQuery(id+"F0.wireOp",EDGE,"E9.14.58.0"),sQuery(id+"F0.wireOp",EDGE,"E9.1.59.0"),sQuery(id+"F0.wireOp",EDGE,"E9.3.59.0"),sQuery(id+"F0.wireOp",EDGE,"E9.7.59.0"),sQuery(id+"F0.wireOp",EDGE,"E9.11.59.0"),sQuery(id+"F0.wireOp",EDGE,"E9.14.59.0")])],"isStart":false})});
            var sketch = newSketch(context, id + "F7", { "sketchPlane" : qUnion([Q0])});
            skCircle(sketch, "E44", {"center": v(0, 0) * mm, "radius": 59 * mm});
            skCircle(sketch, "E45", {"center": v(0, 0) * mm, "radius": 64 * mm});
            skCircle(sketch, "E46", {"center": v(0, 0) * mm, "radius": 63 * mm});
            skCircle(sketch, "E47", {"center": v(0, 0) * mm, "radius": 10 * mm});
            skSolve(sketch);
        }
        {
            var Q0;
            Q0=qSketchRegion(id+"F7",true);
            var Q1;
            Q1=makeQuery(id+"F7.imprint","IMPRINT",FACE,{"disambiguationData":[TD([[makeQuery(id+"F7.imprint","IMPRINT",EDGE,{"derivedFrom":sQuery(id+"F7.wireOp",EDGE,"E44")}),1.0]])]});
            extrude(context, id + "F8", {"entities" : qUnion([Q0, Q1]), "operationType" : NewBodyOperationType.REMOVE, "oppositeDirection" : true, "depth" : 1 * mm, "offsetDistance" : 25 * mm});
        }
        {
            var Q0;
            Q0=makeQuery(id+"F8.boolean.opBoolean","COPY",EDGE,{"derivedFrom":makeQuery(id+"F8.opExtrude","CAP_EDGE",EDGE,{"disambiguationData":[OSD([sQuery(id+"F0.wireOp",EDGE,"E0"),sQuery(id+"F0.wireOp",EDGE,"E1"),sQuery(id+"F0.wireOp",EDGE,"E3"),sQuery(id+"F0.wireOp",EDGE,"E4"),sQuery(id+"F0.wireOp",EDGE,"E5"),sQuery(id+"F0.wireOp",EDGE,"E6.trimOffspring"),sQuery(id+"F0.wireOp",EDGE,"E7"),sQuery(id+"F0.wireOp",EDGE,"E8.1.0"),sQuery(id+"F0.wireOp",EDGE,"E8.1.1"),sQuery(id+"F0.wireOp",EDGE,"E8.1.2"),sQuery(id+"F0.wireOp",EDGE,"E8.1.3"),sQuery(id+"F0.wireOp",EDGE,"E8.1.4"),sQuery(id+"F0.wireOp",EDGE,"E8.2.0"),sQuery(id+"F0.wireOp",EDGE,"E8.2.1"),sQuery(id+"F0.wireOp",EDGE,"E8.2.2"),sQuery(id+"F0.wireOp",EDGE,"E8.2.3"),sQuery(id+"F0.wireOp",EDGE,"E8.2.4"),sQuery(id+"F0.wireOp",EDGE,"E9.1.3.0"),sQuery(id+"F0.wireOp",EDGE,"E9.3.3.0"),sQuery(id+"F0.wireOp",EDGE,"E9.7.3.0"),sQuery(id+"F0.wireOp",EDGE,"E9.11.3.0"),sQuery(id+"F0.wireOp",EDGE,"E9.14.3.0"),sQuery(id+"F0.wireOp",EDGE,"E9.1.4.0"),sQuery(id+"F0.wireOp",EDGE,"E9.3.4.0"),sQuery(id+"F0.wireOp",EDGE,"E9.7.4.0"),sQuery(id+"F0.wireOp",EDGE,"E9.11.4.0"),sQuery(id+"F0.wireOp",EDGE,"E9.14.4.0"),sQuery(id+"F0.wireOp",EDGE,"E9.1.5.0"),sQuery(id+"F0.wireOp",EDGE,"E9.3.5.0"),sQuery(id+"F0.wireOp",EDGE,"E9.7.5.0"),sQuery(id+"F0.wireOp",EDGE,"E9.11.5.0"),sQuery(id+"F0.wireOp",EDGE,"E9.14.5.0"),sQuery(id+"F0.wireOp",EDGE,"E9.1.6.0"),sQuery(id+"F0.wireOp",EDGE,"E9.3.6.0"),sQuery(id+"F0.wireOp",EDGE,"E9.7.6.0"),sQuery(id+"F0.wireOp",EDGE,"E9.11.6.0"),sQuery(id+"F0.wireOp",EDGE,"E9.14.6.0"),sQuery(id+"F0.wireOp",EDGE,"E9.1.7.0"),sQuery(id+"F0.wireOp",EDGE,"E9.3.7.0"),sQuery(id+"F0.wireOp",EDGE,"E9.7.7.0"),sQuery(id+"F0.wireOp",EDGE,"E9.11.7.0"),sQuery(id+"F0.wireOp",EDGE,"E9.14.7.0"),sQuery(id+"F0.wireOp",EDGE,"E9.1.8.0"),sQuery(id+"F0.wireOp",EDGE,"E9.3.8.0"),sQuery(id+"F0.wireOp",EDGE,"E9.7.8.0"),sQuery(id+"F0.wireOp",EDGE,"E9.11.8.0"),sQuery(id+"F0.wireOp",EDGE,"E9.14.8.0"),sQuery(id+"F0.wireOp",EDGE,"E9.1.9.0"),sQuery(id+"F0.wireOp",EDGE,"E9.3.9.0"),sQuery(id+"F0.wireOp",EDGE,"E9.7.9.0"),sQuery(id+"F0.wireOp",EDGE,"E9.11.9.0"),sQuery(id+"F0.wireOp",EDGE,"E9.14.9.0"),sQuery(id+"F0.wireOp",EDGE,"E9.1.10.0"),sQuery(id+"F0.wireOp",EDGE,"E9.3.10.0"),sQuery(id+"F0.wireOp",EDGE,"E9.7.10.0"),sQuery(id+"F0.wireOp",EDGE,"E9.11.10.0"),sQuery(id+"F0.wireOp",EDGE,"E9.14.10.0"),sQuery(id+"F0.wireOp",EDGE,"E9.1.11.0"),sQuery(id+"F0.wireOp",EDGE,"E9.3.11.0"),sQuery(id+"F0.wireOp",EDGE,"E9.7.11.0"),sQuery(id+"F0.wireOp",EDGE,"E9.11.11.0"),sQuery(id+"F0.wireOp",EDGE,"E9.14.11.0"),sQuery(id+"F0.wireOp",EDGE,"E9.1.12.0"),sQuery(id+"F0.wireOp",EDGE,"E9.3.12.0"),sQuery(id+"F0.wireOp",EDGE,"E9.7.12.0"),sQuery(id+"F0.wireOp",EDGE,"E9.11.12.0"),sQuery(id+"F0.wireOp",EDGE,"E9.14.12.0"),sQuery(id+"F0.wireOp",EDGE,"E9.1.13.0"),sQuery(id+"F0.wireOp",EDGE,"E9.3.13.0"),sQuery(id+"F0.wireOp",EDGE,"E9.7.13.0"),sQuery(id+"F0.wireOp",EDGE,"E9.11.13.0"),sQuery(id+"F0.wireOp",EDGE,"E9.14.13.0"),sQuery(id+"F0.wireOp",EDGE,"E9.1.14.0"),sQuery(id+"F0.wireOp",EDGE,"E9.3.14.0"),sQuery(id+"F0.wireOp",EDGE,"E9.7.14.0"),sQuery(id+"F0.wireOp",EDGE,"E9.11.14.0"),sQuery(id+"F0.wireOp",EDGE,"E9.14.14.0"),sQuery(id+"F0.wireOp",EDGE,"E9.1.15.0"),sQuery(id+"F0.wireOp",EDGE,"E9.3.15.0"),sQuery(id+"F0.wireOp",EDGE,"E9.7.15.0"),sQuery(id+"F0.wireOp",EDGE,"E9.11.15.0"),sQuery(id+"F0.wireOp",EDGE,"E9.14.15.0"),sQuery(id+"F0.wireOp",EDGE,"E9.1.16.0"),sQuery(id+"F0.wireOp",EDGE,"E9.3.16.0"),sQuery(id+"F0.wireOp",EDGE,"E9.7.16.0"),sQuery(id+"F0.wireOp",EDGE,"E9.11.16.0"),sQuery(id+"F0.wireOp",EDGE,"E9.14.16.0"),sQuery(id+"F0.wireOp",EDGE,"E9.1.17.0"),sQuery(id+"F0.wireOp",EDGE,"E9.3.17.0"),sQuery(id+"F0.wireOp",EDGE,"E9.7.17.0"),sQuery(id+"F0.wireOp",EDGE,"E9.11.17.0"),sQuery(id+"F0.wireOp",EDGE,"E9.14.17.0"),sQuery(id+"F0.wireOp",EDGE,"E9.1.18.0"),sQuery(id+"F0.wireOp",EDGE,"E9.3.18.0"),sQuery(id+"F0.wireOp",EDGE,"E9.7.18.0"),sQuery(id+"F0.wireOp",EDGE,"E9.11.18.0"),sQuery(id+"F0.wireOp",EDGE,"E9.14.18.0"),sQuery(id+"F0.wireOp",EDGE,"E9.1.19.0"),sQuery(id+"F0.wireOp",EDGE,"E9.3.19.0"),sQuery(id+"F0.wireOp",EDGE,"E9.7.19.0"),sQuery(id+"F0.wireOp",EDGE,"E9.11.19.0"),sQuery(id+"F0.wireOp",EDGE,"E9.14.19.0"),sQuery(id+"F0.wireOp",EDGE,"E9.1.20.0"),sQuery(id+"F0.wireOp",EDGE,"E9.3.20.0"),sQuery(id+"F0.wireOp",EDGE,"E9.7.20.0"),sQuery(id+"F0.wireOp",EDGE,"E9.11.20.0"),sQuery(id+"F0.wireOp",EDGE,"E9.14.20.0"),sQuery(id+"F0.wireOp",EDGE,"E9.1.21.0"),sQuery(id+"F0.wireOp",EDGE,"E9.3.21.0"),sQuery(id+"F0.wireOp",EDGE,"E9.7.21.0"),sQuery(id+"F0.wireOp",EDGE,"E9.11.21.0"),sQuery(id+"F0.wireOp",EDGE,"E9.14.21.0"),sQuery(id+"F0.wireOp",EDGE,"E9.1.22.0"),sQuery(id+"F0.wireOp",EDGE,"E9.3.22.0"),sQuery(id+"F0.wireOp",EDGE,"E9.7.22.0"),sQuery(id+"F0.wireOp",EDGE,"E9.11.22.0"),sQuery(id+"F0.wireOp",EDGE,"E9.14.22.0"),sQuery(id+"F0.wireOp",EDGE,"E9.1.23.0"),sQuery(id+"F0.wireOp",EDGE,"E9.3.23.0"),sQuery(id+"F0.wireOp",EDGE,"E9.7.23.0"),sQuery(id+"F0.wireOp",EDGE,"E9.11.23.0"),sQuery(id+"F0.wireOp",EDGE,"E9.14.23.0"),sQuery(id+"F0.wireOp",EDGE,"E9.1.24.0"),sQuery(id+"F0.wireOp",EDGE,"E9.3.24.0"),sQuery(id+"F0.wireOp",EDGE,"E9.7.24.0"),sQuery(id+"F0.wireOp",EDGE,"E9.11.24.0"),sQuery(id+"F0.wireOp",EDGE,"E9.14.24.0"),sQuery(id+"F0.wireOp",EDGE,"E9.1.25.0"),sQuery(id+"F0.wireOp",EDGE,"E9.3.25.0"),sQuery(id+"F0.wireOp",EDGE,"E9.7.25.0"),sQuery(id+"F0.wireOp",EDGE,"E9.11.25.0"),sQuery(id+"F0.wireOp",EDGE,"E9.14.25.0"),sQuery(id+"F0.wireOp",EDGE,"E9.1.26.0"),sQuery(id+"F0.wireOp",EDGE,"E9.3.26.0"),sQuery(id+"F0.wireOp",EDGE,"E9.7.26.0"),sQuery(id+"F0.wireOp",EDGE,"E9.11.26.0"),sQuery(id+"F0.wireOp",EDGE,"E9.14.26.0"),sQuery(id+"F0.wireOp",EDGE,"E9.1.27.0"),sQuery(id+"F0.wireOp",EDGE,"E9.3.27.0"),sQuery(id+"F0.wireOp",EDGE,"E9.7.27.0"),sQuery(id+"F0.wireOp",EDGE,"E9.11.27.0"),sQuery(id+"F0.wireOp",EDGE,"E9.14.27.0"),sQuery(id+"F0.wireOp",EDGE,"E9.1.28.0"),sQuery(id+"F0.wireOp",EDGE,"E9.3.28.0"),sQuery(id+"F0.wireOp",EDGE,"E9.7.28.0"),sQuery(id+"F0.wireOp",EDGE,"E9.11.28.0"),sQuery(id+"F0.wireOp",EDGE,"E9.14.28.0"),sQuery(id+"F0.wireOp",EDGE,"E9.1.29.0"),sQuery(id+"F0.wireOp",EDGE,"E9.3.29.0"),sQuery(id+"F0.wireOp",EDGE,"E9.7.29.0"),sQuery(id+"F0.wireOp",EDGE,"E9.11.29.0"),sQuery(id+"F0.wireOp",EDGE,"E9.14.29.0"),sQuery(id+"F0.wireOp",EDGE,"E9.1.30.0"),sQuery(id+"F0.wireOp",EDGE,"E9.3.30.0"),sQuery(id+"F0.wireOp",EDGE,"E9.7.30.0"),sQuery(id+"F0.wireOp",EDGE,"E9.11.30.0"),sQuery(id+"F0.wireOp",EDGE,"E9.14.30.0"),sQuery(id+"F0.wireOp",EDGE,"E9.1.31.0"),sQuery(id+"F0.wireOp",EDGE,"E9.3.31.0"),sQuery(id+"F0.wireOp",EDGE,"E9.7.31.0"),sQuery(id+"F0.wireOp",EDGE,"E9.11.31.0"),sQuery(id+"F0.wireOp",EDGE,"E9.14.31.0"),sQuery(id+"F0.wireOp",EDGE,"E9.1.32.0"),sQuery(id+"F0.wireOp",EDGE,"E9.3.32.0"),sQuery(id+"F0.wireOp",EDGE,"E9.7.32.0"),sQuery(id+"F0.wireOp",EDGE,"E9.11.32.0"),sQuery(id+"F0.wireOp",EDGE,"E9.14.32.0"),sQuery(id+"F0.wireOp",EDGE,"E9.1.33.0"),sQuery(id+"F0.wireOp",EDGE,"E9.3.33.0"),sQuery(id+"F0.wireOp",EDGE,"E9.7.33.0"),sQuery(id+"F0.wireOp",EDGE,"E9.11.33.0"),sQuery(id+"F0.wireOp",EDGE,"E9.14.33.0"),sQuery(id+"F0.wireOp",EDGE,"E9.1.34.0"),sQuery(id+"F0.wireOp",EDGE,"E9.3.34.0"),sQuery(id+"F0.wireOp",EDGE,"E9.7.34.0"),sQuery(id+"F0.wireOp",EDGE,"E9.11.34.0"),sQuery(id+"F0.wireOp",EDGE,"E9.14.34.0"),sQuery(id+"F0.wireOp",EDGE,"E9.1.35.0"),sQuery(id+"F0.wireOp",EDGE,"E9.3.35.0"),sQuery(id+"F0.wireOp",EDGE,"E9.7.35.0"),sQuery(id+"F0.wireOp",EDGE,"E9.11.35.0"),sQuery(id+"F0.wireOp",EDGE,"E9.14.35.0"),sQuery(id+"F0.wireOp",EDGE,"E9.1.36.0"),sQuery(id+"F0.wireOp",EDGE,"E9.3.36.0"),sQuery(id+"F0.wireOp",EDGE,"E9.7.36.0"),sQuery(id+"F0.wireOp",EDGE,"E9.11.36.0"),sQuery(id+"F0.wireOp",EDGE,"E9.14.36.0"),sQuery(id+"F0.wireOp",EDGE,"E9.1.37.0"),sQuery(id+"F0.wireOp",EDGE,"E9.3.37.0"),sQuery(id+"F0.wireOp",EDGE,"E9.7.37.0"),sQuery(id+"F0.wireOp",EDGE,"E9.11.37.0"),sQuery(id+"F0.wireOp",EDGE,"E9.14.37.0"),sQuery(id+"F0.wireOp",EDGE,"E9.1.38.0"),sQuery(id+"F0.wireOp",EDGE,"E9.3.38.0"),sQuery(id+"F0.wireOp",EDGE,"E9.7.38.0"),sQuery(id+"F0.wireOp",EDGE,"E9.11.38.0"),sQuery(id+"F0.wireOp",EDGE,"E9.14.38.0"),sQuery(id+"F0.wireOp",EDGE,"E9.1.39.0"),sQuery(id+"F0.wireOp",EDGE,"E9.3.39.0"),sQuery(id+"F0.wireOp",EDGE,"E9.7.39.0"),sQuery(id+"F0.wireOp",EDGE,"E9.11.39.0"),sQuery(id+"F0.wireOp",EDGE,"E9.14.39.0"),sQuery(id+"F0.wireOp",EDGE,"E9.1.40.0"),sQuery(id+"F0.wireOp",EDGE,"E9.3.40.0"),sQuery(id+"F0.wireOp",EDGE,"E9.7.40.0"),sQuery(id+"F0.wireOp",EDGE,"E9.11.40.0"),sQuery(id+"F0.wireOp",EDGE,"E9.14.40.0"),sQuery(id+"F0.wireOp",EDGE,"E9.1.41.0"),sQuery(id+"F0.wireOp",EDGE,"E9.3.41.0"),sQuery(id+"F0.wireOp",EDGE,"E9.7.41.0"),sQuery(id+"F0.wireOp",EDGE,"E9.11.41.0"),sQuery(id+"F0.wireOp",EDGE,"E9.14.41.0"),sQuery(id+"F0.wireOp",EDGE,"E9.1.42.0"),sQuery(id+"F0.wireOp",EDGE,"E9.3.42.0"),sQuery(id+"F0.wireOp",EDGE,"E9.7.42.0"),sQuery(id+"F0.wireOp",EDGE,"E9.11.42.0"),sQuery(id+"F0.wireOp",EDGE,"E9.14.42.0"),sQuery(id+"F0.wireOp",EDGE,"E9.1.43.0"),sQuery(id+"F0.wireOp",EDGE,"E9.3.43.0"),sQuery(id+"F0.wireOp",EDGE,"E9.7.43.0"),sQuery(id+"F0.wireOp",EDGE,"E9.11.43.0"),sQuery(id+"F0.wireOp",EDGE,"E9.14.43.0"),sQuery(id+"F0.wireOp",EDGE,"E9.1.44.0"),sQuery(id+"F0.wireOp",EDGE,"E9.3.44.0"),sQuery(id+"F0.wireOp",EDGE,"E9.7.44.0"),sQuery(id+"F0.wireOp",EDGE,"E9.11.44.0"),sQuery(id+"F0.wireOp",EDGE,"E9.14.44.0"),sQuery(id+"F0.wireOp",EDGE,"E9.1.45.0"),sQuery(id+"F0.wireOp",EDGE,"E9.3.45.0"),sQuery(id+"F0.wireOp",EDGE,"E9.7.45.0"),sQuery(id+"F0.wireOp",EDGE,"E9.11.45.0"),sQuery(id+"F0.wireOp",EDGE,"E9.14.45.0"),sQuery(id+"F0.wireOp",EDGE,"E9.1.46.0"),sQuery(id+"F0.wireOp",EDGE,"E9.3.46.0"),sQuery(id+"F0.wireOp",EDGE,"E9.7.46.0"),sQuery(id+"F0.wireOp",EDGE,"E9.11.46.0"),sQuery(id+"F0.wireOp",EDGE,"E9.14.46.0"),sQuery(id+"F0.wireOp",EDGE,"E9.1.47.0"),sQuery(id+"F0.wireOp",EDGE,"E9.3.47.0"),sQuery(id+"F0.wireOp",EDGE,"E9.7.47.0"),sQuery(id+"F0.wireOp",EDGE,"E9.11.47.0"),sQuery(id+"F0.wireOp",EDGE,"E9.14.47.0"),sQuery(id+"F0.wireOp",EDGE,"E9.1.48.0"),sQuery(id+"F0.wireOp",EDGE,"E9.3.48.0"),sQuery(id+"F0.wireOp",EDGE,"E9.7.48.0"),sQuery(id+"F0.wireOp",EDGE,"E9.11.48.0"),sQuery(id+"F0.wireOp",EDGE,"E9.14.48.0"),sQuery(id+"F0.wireOp",EDGE,"E9.1.49.0"),sQuery(id+"F0.wireOp",EDGE,"E9.3.49.0"),sQuery(id+"F0.wireOp",EDGE,"E9.7.49.0"),sQuery(id+"F0.wireOp",EDGE,"E9.11.49.0"),sQuery(id+"F0.wireOp",EDGE,"E9.14.49.0"),sQuery(id+"F0.wireOp",EDGE,"E9.1.50.0"),sQuery(id+"F0.wireOp",EDGE,"E9.3.50.0"),sQuery(id+"F0.wireOp",EDGE,"E9.7.50.0"),sQuery(id+"F0.wireOp",EDGE,"E9.11.50.0"),sQuery(id+"F0.wireOp",EDGE,"E9.14.50.0"),sQuery(id+"F0.wireOp",EDGE,"E9.1.51.0"),sQuery(id+"F0.wireOp",EDGE,"E9.3.51.0"),sQuery(id+"F0.wireOp",EDGE,"E9.7.51.0"),sQuery(id+"F0.wireOp",EDGE,"E9.11.51.0"),sQuery(id+"F0.wireOp",EDGE,"E9.14.51.0"),sQuery(id+"F0.wireOp",EDGE,"E9.1.52.0"),sQuery(id+"F0.wireOp",EDGE,"E9.3.52.0"),sQuery(id+"F0.wireOp",EDGE,"E9.7.52.0"),sQuery(id+"F0.wireOp",EDGE,"E9.11.52.0"),sQuery(id+"F0.wireOp",EDGE,"E9.14.52.0"),sQuery(id+"F0.wireOp",EDGE,"E9.1.53.0"),sQuery(id+"F0.wireOp",EDGE,"E9.3.53.0"),sQuery(id+"F0.wireOp",EDGE,"E9.7.53.0"),sQuery(id+"F0.wireOp",EDGE,"E9.11.53.0"),sQuery(id+"F0.wireOp",EDGE,"E9.14.53.0"),sQuery(id+"F0.wireOp",EDGE,"E9.1.54.0"),sQuery(id+"F0.wireOp",EDGE,"E9.3.54.0"),sQuery(id+"F0.wireOp",EDGE,"E9.7.54.0"),sQuery(id+"F0.wireOp",EDGE,"E9.11.54.0"),sQuery(id+"F0.wireOp",EDGE,"E9.14.54.0"),sQuery(id+"F0.wireOp",EDGE,"E9.1.55.0"),sQuery(id+"F0.wireOp",EDGE,"E9.3.55.0"),sQuery(id+"F0.wireOp",EDGE,"E9.7.55.0"),sQuery(id+"F0.wireOp",EDGE,"E9.11.55.0"),sQuery(id+"F0.wireOp",EDGE,"E9.14.55.0"),sQuery(id+"F0.wireOp",EDGE,"E9.1.56.0"),sQuery(id+"F0.wireOp",EDGE,"E9.3.56.0"),sQuery(id+"F0.wireOp",EDGE,"E9.7.56.0"),sQuery(id+"F0.wireOp",EDGE,"E9.11.56.0"),sQuery(id+"F0.wireOp",EDGE,"E9.14.56.0"),sQuery(id+"F0.wireOp",EDGE,"E9.1.57.0"),sQuery(id+"F0.wireOp",EDGE,"E9.3.57.0"),sQuery(id+"F0.wireOp",EDGE,"E9.7.57.0"),sQuery(id+"F0.wireOp",EDGE,"E9.11.57.0"),sQuery(id+"F0.wireOp",EDGE,"E9.14.57.0"),sQuery(id+"F0.wireOp",EDGE,"E9.1.58.0"),sQuery(id+"F0.wireOp",EDGE,"E9.3.58.0"),sQuery(id+"F0.wireOp",EDGE,"E9.7.58.0"),sQuery(id+"F0.wireOp",EDGE,"E9.11.58.0"),sQuery(id+"F0.wireOp",EDGE,"E9.14.58.0"),sQuery(id+"F0.wireOp",EDGE,"E9.1.59.0"),sQuery(id+"F0.wireOp",EDGE,"E9.3.59.0"),sQuery(id+"F0.wireOp",EDGE,"E9.7.59.0"),sQuery(id+"F0.wireOp",EDGE,"E9.11.59.0"),sQuery(id+"F0.wireOp",EDGE,"E9.14.59.0"),sQuery(id+"F2.wireOp",EDGE,"E19")])],"isStart":false})});
            var Q1;
            Q1=makeQuery(id+"F8.boolean.opBoolean","COPY",EDGE,{"derivedFrom":makeQuery(id+"F8.opExtrude","CAP_EDGE",EDGE,{"disambiguationData":[OSD([sQuery(id+"F0.wireOp",EDGE,"E0"),sQuery(id+"F0.wireOp",EDGE,"E1"),sQuery(id+"F0.wireOp",EDGE,"E3"),sQuery(id+"F0.wireOp",EDGE,"E4"),sQuery(id+"F0.wireOp",EDGE,"E5"),sQuery(id+"F0.wireOp",EDGE,"E6.trimOffspring"),sQuery(id+"F0.wireOp",EDGE,"E7"),sQuery(id+"F0.wireOp",EDGE,"E8.1.0"),sQuery(id+"F0.wireOp",EDGE,"E8.1.1"),sQuery(id+"F0.wireOp",EDGE,"E8.1.2"),sQuery(id+"F0.wireOp",EDGE,"E8.1.3"),sQuery(id+"F0.wireOp",EDGE,"E8.1.4"),sQuery(id+"F0.wireOp",EDGE,"E8.2.0"),sQuery(id+"F0.wireOp",EDGE,"E8.2.1"),sQuery(id+"F0.wireOp",EDGE,"E8.2.2"),sQuery(id+"F0.wireOp",EDGE,"E8.2.3"),sQuery(id+"F0.wireOp",EDGE,"E8.2.4"),sQuery(id+"F0.wireOp",EDGE,"E9.1.3.0"),sQuery(id+"F0.wireOp",EDGE,"E9.3.3.0"),sQuery(id+"F0.wireOp",EDGE,"E9.7.3.0"),sQuery(id+"F0.wireOp",EDGE,"E9.11.3.0"),sQuery(id+"F0.wireOp",EDGE,"E9.14.3.0"),sQuery(id+"F0.wireOp",EDGE,"E9.1.4.0"),sQuery(id+"F0.wireOp",EDGE,"E9.3.4.0"),sQuery(id+"F0.wireOp",EDGE,"E9.7.4.0"),sQuery(id+"F0.wireOp",EDGE,"E9.11.4.0"),sQuery(id+"F0.wireOp",EDGE,"E9.14.4.0"),sQuery(id+"F0.wireOp",EDGE,"E9.1.5.0"),sQuery(id+"F0.wireOp",EDGE,"E9.3.5.0"),sQuery(id+"F0.wireOp",EDGE,"E9.7.5.0"),sQuery(id+"F0.wireOp",EDGE,"E9.11.5.0"),sQuery(id+"F0.wireOp",EDGE,"E9.14.5.0"),sQuery(id+"F0.wireOp",EDGE,"E9.1.6.0"),sQuery(id+"F0.wireOp",EDGE,"E9.3.6.0"),sQuery(id+"F0.wireOp",EDGE,"E9.7.6.0"),sQuery(id+"F0.wireOp",EDGE,"E9.11.6.0"),sQuery(id+"F0.wireOp",EDGE,"E9.14.6.0"),sQuery(id+"F0.wireOp",EDGE,"E9.1.7.0"),sQuery(id+"F0.wireOp",EDGE,"E9.3.7.0"),sQuery(id+"F0.wireOp",EDGE,"E9.7.7.0"),sQuery(id+"F0.wireOp",EDGE,"E9.11.7.0"),sQuery(id+"F0.wireOp",EDGE,"E9.14.7.0"),sQuery(id+"F0.wireOp",EDGE,"E9.1.8.0"),sQuery(id+"F0.wireOp",EDGE,"E9.3.8.0"),sQuery(id+"F0.wireOp",EDGE,"E9.7.8.0"),sQuery(id+"F0.wireOp",EDGE,"E9.11.8.0"),sQuery(id+"F0.wireOp",EDGE,"E9.14.8.0"),sQuery(id+"F0.wireOp",EDGE,"E9.1.9.0"),sQuery(id+"F0.wireOp",EDGE,"E9.3.9.0"),sQuery(id+"F0.wireOp",EDGE,"E9.7.9.0"),sQuery(id+"F0.wireOp",EDGE,"E9.11.9.0"),sQuery(id+"F0.wireOp",EDGE,"E9.14.9.0"),sQuery(id+"F0.wireOp",EDGE,"E9.1.10.0"),sQuery(id+"F0.wireOp",EDGE,"E9.3.10.0"),sQuery(id+"F0.wireOp",EDGE,"E9.7.10.0"),sQuery(id+"F0.wireOp",EDGE,"E9.11.10.0"),sQuery(id+"F0.wireOp",EDGE,"E9.14.10.0"),sQuery(id+"F0.wireOp",EDGE,"E9.1.11.0"),sQuery(id+"F0.wireOp",EDGE,"E9.3.11.0"),sQuery(id+"F0.wireOp",EDGE,"E9.7.11.0"),sQuery(id+"F0.wireOp",EDGE,"E9.11.11.0"),sQuery(id+"F0.wireOp",EDGE,"E9.14.11.0"),sQuery(id+"F0.wireOp",EDGE,"E9.1.12.0"),sQuery(id+"F0.wireOp",EDGE,"E9.3.12.0"),sQuery(id+"F0.wireOp",EDGE,"E9.7.12.0"),sQuery(id+"F0.wireOp",EDGE,"E9.11.12.0"),sQuery(id+"F0.wireOp",EDGE,"E9.14.12.0"),sQuery(id+"F0.wireOp",EDGE,"E9.1.13.0"),sQuery(id+"F0.wireOp",EDGE,"E9.3.13.0"),sQuery(id+"F0.wireOp",EDGE,"E9.7.13.0"),sQuery(id+"F0.wireOp",EDGE,"E9.11.13.0"),sQuery(id+"F0.wireOp",EDGE,"E9.14.13.0"),sQuery(id+"F0.wireOp",EDGE,"E9.1.14.0"),sQuery(id+"F0.wireOp",EDGE,"E9.3.14.0"),sQuery(id+"F0.wireOp",EDGE,"E9.7.14.0"),sQuery(id+"F0.wireOp",EDGE,"E9.11.14.0"),sQuery(id+"F0.wireOp",EDGE,"E9.14.14.0"),sQuery(id+"F0.wireOp",EDGE,"E9.1.15.0"),sQuery(id+"F0.wireOp",EDGE,"E9.3.15.0"),sQuery(id+"F0.wireOp",EDGE,"E9.7.15.0"),sQuery(id+"F0.wireOp",EDGE,"E9.11.15.0"),sQuery(id+"F0.wireOp",EDGE,"E9.14.15.0"),sQuery(id+"F0.wireOp",EDGE,"E9.1.16.0"),sQuery(id+"F0.wireOp",EDGE,"E9.3.16.0"),sQuery(id+"F0.wireOp",EDGE,"E9.7.16.0"),sQuery(id+"F0.wireOp",EDGE,"E9.11.16.0"),sQuery(id+"F0.wireOp",EDGE,"E9.14.16.0"),sQuery(id+"F0.wireOp",EDGE,"E9.1.17.0"),sQuery(id+"F0.wireOp",EDGE,"E9.3.17.0"),sQuery(id+"F0.wireOp",EDGE,"E9.7.17.0"),sQuery(id+"F0.wireOp",EDGE,"E9.11.17.0"),sQuery(id+"F0.wireOp",EDGE,"E9.14.17.0"),sQuery(id+"F0.wireOp",EDGE,"E9.1.18.0"),sQuery(id+"F0.wireOp",EDGE,"E9.3.18.0"),sQuery(id+"F0.wireOp",EDGE,"E9.7.18.0"),sQuery(id+"F0.wireOp",EDGE,"E9.11.18.0"),sQuery(id+"F0.wireOp",EDGE,"E9.14.18.0"),sQuery(id+"F0.wireOp",EDGE,"E9.1.19.0"),sQuery(id+"F0.wireOp",EDGE,"E9.3.19.0"),sQuery(id+"F0.wireOp",EDGE,"E9.7.19.0"),sQuery(id+"F0.wireOp",EDGE,"E9.11.19.0"),sQuery(id+"F0.wireOp",EDGE,"E9.14.19.0"),sQuery(id+"F0.wireOp",EDGE,"E9.1.20.0"),sQuery(id+"F0.wireOp",EDGE,"E9.3.20.0"),sQuery(id+"F0.wireOp",EDGE,"E9.7.20.0"),sQuery(id+"F0.wireOp",EDGE,"E9.11.20.0"),sQuery(id+"F0.wireOp",EDGE,"E9.14.20.0"),sQuery(id+"F0.wireOp",EDGE,"E9.1.21.0"),sQuery(id+"F0.wireOp",EDGE,"E9.3.21.0"),sQuery(id+"F0.wireOp",EDGE,"E9.7.21.0"),sQuery(id+"F0.wireOp",EDGE,"E9.11.21.0"),sQuery(id+"F0.wireOp",EDGE,"E9.14.21.0"),sQuery(id+"F0.wireOp",EDGE,"E9.1.22.0"),sQuery(id+"F0.wireOp",EDGE,"E9.3.22.0"),sQuery(id+"F0.wireOp",EDGE,"E9.7.22.0"),sQuery(id+"F0.wireOp",EDGE,"E9.11.22.0"),sQuery(id+"F0.wireOp",EDGE,"E9.14.22.0"),sQuery(id+"F0.wireOp",EDGE,"E9.1.23.0"),sQuery(id+"F0.wireOp",EDGE,"E9.3.23.0"),sQuery(id+"F0.wireOp",EDGE,"E9.7.23.0"),sQuery(id+"F0.wireOp",EDGE,"E9.11.23.0"),sQuery(id+"F0.wireOp",EDGE,"E9.14.23.0"),sQuery(id+"F0.wireOp",EDGE,"E9.1.24.0"),sQuery(id+"F0.wireOp",EDGE,"E9.3.24.0"),sQuery(id+"F0.wireOp",EDGE,"E9.7.24.0"),sQuery(id+"F0.wireOp",EDGE,"E9.11.24.0"),sQuery(id+"F0.wireOp",EDGE,"E9.14.24.0"),sQuery(id+"F0.wireOp",EDGE,"E9.1.25.0"),sQuery(id+"F0.wireOp",EDGE,"E9.3.25.0"),sQuery(id+"F0.wireOp",EDGE,"E9.7.25.0"),sQuery(id+"F0.wireOp",EDGE,"E9.11.25.0"),sQuery(id+"F0.wireOp",EDGE,"E9.14.25.0"),sQuery(id+"F0.wireOp",EDGE,"E9.1.26.0"),sQuery(id+"F0.wireOp",EDGE,"E9.3.26.0"),sQuery(id+"F0.wireOp",EDGE,"E9.7.26.0"),sQuery(id+"F0.wireOp",EDGE,"E9.11.26.0"),sQuery(id+"F0.wireOp",EDGE,"E9.14.26.0"),sQuery(id+"F0.wireOp",EDGE,"E9.1.27.0"),sQuery(id+"F0.wireOp",EDGE,"E9.3.27.0"),sQuery(id+"F0.wireOp",EDGE,"E9.7.27.0"),sQuery(id+"F0.wireOp",EDGE,"E9.11.27.0"),sQuery(id+"F0.wireOp",EDGE,"E9.14.27.0"),sQuery(id+"F0.wireOp",EDGE,"E9.1.28.0"),sQuery(id+"F0.wireOp",EDGE,"E9.3.28.0"),sQuery(id+"F0.wireOp",EDGE,"E9.7.28.0"),sQuery(id+"F0.wireOp",EDGE,"E9.11.28.0"),sQuery(id+"F0.wireOp",EDGE,"E9.14.28.0"),sQuery(id+"F0.wireOp",EDGE,"E9.1.29.0"),sQuery(id+"F0.wireOp",EDGE,"E9.3.29.0"),sQuery(id+"F0.wireOp",EDGE,"E9.7.29.0"),sQuery(id+"F0.wireOp",EDGE,"E9.11.29.0"),sQuery(id+"F0.wireOp",EDGE,"E9.14.29.0"),sQuery(id+"F0.wireOp",EDGE,"E9.1.30.0"),sQuery(id+"F0.wireOp",EDGE,"E9.3.30.0"),sQuery(id+"F0.wireOp",EDGE,"E9.7.30.0"),sQuery(id+"F0.wireOp",EDGE,"E9.11.30.0"),sQuery(id+"F0.wireOp",EDGE,"E9.14.30.0"),sQuery(id+"F0.wireOp",EDGE,"E9.1.31.0"),sQuery(id+"F0.wireOp",EDGE,"E9.3.31.0"),sQuery(id+"F0.wireOp",EDGE,"E9.7.31.0"),sQuery(id+"F0.wireOp",EDGE,"E9.11.31.0"),sQuery(id+"F0.wireOp",EDGE,"E9.14.31.0"),sQuery(id+"F0.wireOp",EDGE,"E9.1.32.0"),sQuery(id+"F0.wireOp",EDGE,"E9.3.32.0"),sQuery(id+"F0.wireOp",EDGE,"E9.7.32.0"),sQuery(id+"F0.wireOp",EDGE,"E9.11.32.0"),sQuery(id+"F0.wireOp",EDGE,"E9.14.32.0"),sQuery(id+"F0.wireOp",EDGE,"E9.1.33.0"),sQuery(id+"F0.wireOp",EDGE,"E9.3.33.0"),sQuery(id+"F0.wireOp",EDGE,"E9.7.33.0"),sQuery(id+"F0.wireOp",EDGE,"E9.11.33.0"),sQuery(id+"F0.wireOp",EDGE,"E9.14.33.0"),sQuery(id+"F0.wireOp",EDGE,"E9.1.34.0"),sQuery(id+"F0.wireOp",EDGE,"E9.3.34.0"),sQuery(id+"F0.wireOp",EDGE,"E9.7.34.0"),sQuery(id+"F0.wireOp",EDGE,"E9.11.34.0"),sQuery(id+"F0.wireOp",EDGE,"E9.14.34.0"),sQuery(id+"F0.wireOp",EDGE,"E9.1.35.0"),sQuery(id+"F0.wireOp",EDGE,"E9.3.35.0"),sQuery(id+"F0.wireOp",EDGE,"E9.7.35.0"),sQuery(id+"F0.wireOp",EDGE,"E9.11.35.0"),sQuery(id+"F0.wireOp",EDGE,"E9.14.35.0"),sQuery(id+"F0.wireOp",EDGE,"E9.1.36.0"),sQuery(id+"F0.wireOp",EDGE,"E9.3.36.0"),sQuery(id+"F0.wireOp",EDGE,"E9.7.36.0"),sQuery(id+"F0.wireOp",EDGE,"E9.11.36.0"),sQuery(id+"F0.wireOp",EDGE,"E9.14.36.0"),sQuery(id+"F0.wireOp",EDGE,"E9.1.37.0"),sQuery(id+"F0.wireOp",EDGE,"E9.3.37.0"),sQuery(id+"F0.wireOp",EDGE,"E9.7.37.0"),sQuery(id+"F0.wireOp",EDGE,"E9.11.37.0"),sQuery(id+"F0.wireOp",EDGE,"E9.14.37.0"),sQuery(id+"F0.wireOp",EDGE,"E9.1.38.0"),sQuery(id+"F0.wireOp",EDGE,"E9.3.38.0"),sQuery(id+"F0.wireOp",EDGE,"E9.7.38.0"),sQuery(id+"F0.wireOp",EDGE,"E9.11.38.0"),sQuery(id+"F0.wireOp",EDGE,"E9.14.38.0"),sQuery(id+"F0.wireOp",EDGE,"E9.1.39.0"),sQuery(id+"F0.wireOp",EDGE,"E9.3.39.0"),sQuery(id+"F0.wireOp",EDGE,"E9.7.39.0"),sQuery(id+"F0.wireOp",EDGE,"E9.11.39.0"),sQuery(id+"F0.wireOp",EDGE,"E9.14.39.0"),sQuery(id+"F0.wireOp",EDGE,"E9.1.40.0"),sQuery(id+"F0.wireOp",EDGE,"E9.3.40.0"),sQuery(id+"F0.wireOp",EDGE,"E9.7.40.0"),sQuery(id+"F0.wireOp",EDGE,"E9.11.40.0"),sQuery(id+"F0.wireOp",EDGE,"E9.14.40.0"),sQuery(id+"F0.wireOp",EDGE,"E9.1.41.0"),sQuery(id+"F0.wireOp",EDGE,"E9.3.41.0"),sQuery(id+"F0.wireOp",EDGE,"E9.7.41.0"),sQuery(id+"F0.wireOp",EDGE,"E9.11.41.0"),sQuery(id+"F0.wireOp",EDGE,"E9.14.41.0"),sQuery(id+"F0.wireOp",EDGE,"E9.1.42.0"),sQuery(id+"F0.wireOp",EDGE,"E9.3.42.0"),sQuery(id+"F0.wireOp",EDGE,"E9.7.42.0"),sQuery(id+"F0.wireOp",EDGE,"E9.11.42.0"),sQuery(id+"F0.wireOp",EDGE,"E9.14.42.0"),sQuery(id+"F0.wireOp",EDGE,"E9.1.43.0"),sQuery(id+"F0.wireOp",EDGE,"E9.3.43.0"),sQuery(id+"F0.wireOp",EDGE,"E9.7.43.0"),sQuery(id+"F0.wireOp",EDGE,"E9.11.43.0"),sQuery(id+"F0.wireOp",EDGE,"E9.14.43.0"),sQuery(id+"F0.wireOp",EDGE,"E9.1.44.0"),sQuery(id+"F0.wireOp",EDGE,"E9.3.44.0"),sQuery(id+"F0.wireOp",EDGE,"E9.7.44.0"),sQuery(id+"F0.wireOp",EDGE,"E9.11.44.0"),sQuery(id+"F0.wireOp",EDGE,"E9.14.44.0"),sQuery(id+"F0.wireOp",EDGE,"E9.1.45.0"),sQuery(id+"F0.wireOp",EDGE,"E9.3.45.0"),sQuery(id+"F0.wireOp",EDGE,"E9.7.45.0"),sQuery(id+"F0.wireOp",EDGE,"E9.11.45.0"),sQuery(id+"F0.wireOp",EDGE,"E9.14.45.0"),sQuery(id+"F0.wireOp",EDGE,"E9.1.46.0"),sQuery(id+"F0.wireOp",EDGE,"E9.3.46.0"),sQuery(id+"F0.wireOp",EDGE,"E9.7.46.0"),sQuery(id+"F0.wireOp",EDGE,"E9.11.46.0"),sQuery(id+"F0.wireOp",EDGE,"E9.14.46.0"),sQuery(id+"F0.wireOp",EDGE,"E9.1.47.0"),sQuery(id+"F0.wireOp",EDGE,"E9.3.47.0"),sQuery(id+"F0.wireOp",EDGE,"E9.7.47.0"),sQuery(id+"F0.wireOp",EDGE,"E9.11.47.0"),sQuery(id+"F0.wireOp",EDGE,"E9.14.47.0"),sQuery(id+"F0.wireOp",EDGE,"E9.1.48.0"),sQuery(id+"F0.wireOp",EDGE,"E9.3.48.0"),sQuery(id+"F0.wireOp",EDGE,"E9.7.48.0"),sQuery(id+"F0.wireOp",EDGE,"E9.11.48.0"),sQuery(id+"F0.wireOp",EDGE,"E9.14.48.0"),sQuery(id+"F0.wireOp",EDGE,"E9.1.49.0"),sQuery(id+"F0.wireOp",EDGE,"E9.3.49.0"),sQuery(id+"F0.wireOp",EDGE,"E9.7.49.0"),sQuery(id+"F0.wireOp",EDGE,"E9.11.49.0"),sQuery(id+"F0.wireOp",EDGE,"E9.14.49.0"),sQuery(id+"F0.wireOp",EDGE,"E9.1.50.0"),sQuery(id+"F0.wireOp",EDGE,"E9.3.50.0"),sQuery(id+"F0.wireOp",EDGE,"E9.7.50.0"),sQuery(id+"F0.wireOp",EDGE,"E9.11.50.0"),sQuery(id+"F0.wireOp",EDGE,"E9.14.50.0"),sQuery(id+"F0.wireOp",EDGE,"E9.1.51.0"),sQuery(id+"F0.wireOp",EDGE,"E9.3.51.0"),sQuery(id+"F0.wireOp",EDGE,"E9.7.51.0"),sQuery(id+"F0.wireOp",EDGE,"E9.11.51.0"),sQuery(id+"F0.wireOp",EDGE,"E9.14.51.0"),sQuery(id+"F0.wireOp",EDGE,"E9.1.52.0"),sQuery(id+"F0.wireOp",EDGE,"E9.3.52.0"),sQuery(id+"F0.wireOp",EDGE,"E9.7.52.0"),sQuery(id+"F0.wireOp",EDGE,"E9.11.52.0"),sQuery(id+"F0.wireOp",EDGE,"E9.14.52.0"),sQuery(id+"F0.wireOp",EDGE,"E9.1.53.0"),sQuery(id+"F0.wireOp",EDGE,"E9.3.53.0"),sQuery(id+"F0.wireOp",EDGE,"E9.7.53.0"),sQuery(id+"F0.wireOp",EDGE,"E9.11.53.0"),sQuery(id+"F0.wireOp",EDGE,"E9.14.53.0"),sQuery(id+"F0.wireOp",EDGE,"E9.1.54.0"),sQuery(id+"F0.wireOp",EDGE,"E9.3.54.0"),sQuery(id+"F0.wireOp",EDGE,"E9.7.54.0"),sQuery(id+"F0.wireOp",EDGE,"E9.11.54.0"),sQuery(id+"F0.wireOp",EDGE,"E9.14.54.0"),sQuery(id+"F0.wireOp",EDGE,"E9.1.55.0"),sQuery(id+"F0.wireOp",EDGE,"E9.3.55.0"),sQuery(id+"F0.wireOp",EDGE,"E9.7.55.0"),sQuery(id+"F0.wireOp",EDGE,"E9.11.55.0"),sQuery(id+"F0.wireOp",EDGE,"E9.14.55.0"),sQuery(id+"F0.wireOp",EDGE,"E9.1.56.0"),sQuery(id+"F0.wireOp",EDGE,"E9.3.56.0"),sQuery(id+"F0.wireOp",EDGE,"E9.7.56.0"),sQuery(id+"F0.wireOp",EDGE,"E9.11.56.0"),sQuery(id+"F0.wireOp",EDGE,"E9.14.56.0"),sQuery(id+"F0.wireOp",EDGE,"E9.1.57.0"),sQuery(id+"F0.wireOp",EDGE,"E9.3.57.0"),sQuery(id+"F0.wireOp",EDGE,"E9.7.57.0"),sQuery(id+"F0.wireOp",EDGE,"E9.11.57.0"),sQuery(id+"F0.wireOp",EDGE,"E9.14.57.0"),sQuery(id+"F0.wireOp",EDGE,"E9.1.58.0"),sQuery(id+"F0.wireOp",EDGE,"E9.3.58.0"),sQuery(id+"F0.wireOp",EDGE,"E9.7.58.0"),sQuery(id+"F0.wireOp",EDGE,"E9.11.58.0"),sQuery(id+"F0.wireOp",EDGE,"E9.14.58.0"),sQuery(id+"F0.wireOp",EDGE,"E9.1.59.0"),sQuery(id+"F0.wireOp",EDGE,"E9.3.59.0"),sQuery(id+"F0.wireOp",EDGE,"E9.7.59.0"),sQuery(id+"F0.wireOp",EDGE,"E9.11.59.0"),sQuery(id+"F0.wireOp",EDGE,"E9.14.59.0"),sQuery(id+"F2.wireOp",EDGE,"E35.trimOffspring")])],"isStart":false})});
            var Q2;
            Q2=makeQuery(id+"F8.boolean.opBoolean","COPY",EDGE,{"derivedFrom":makeQuery(id+"F8.opExtrude","CAP_EDGE",EDGE,{"disambiguationData":[OSD([sQuery(id+"F0.wireOp",EDGE,"E0"),sQuery(id+"F0.wireOp",EDGE,"E1"),sQuery(id+"F0.wireOp",EDGE,"E3"),sQuery(id+"F0.wireOp",EDGE,"E4"),sQuery(id+"F0.wireOp",EDGE,"E5"),sQuery(id+"F0.wireOp",EDGE,"E6.trimOffspring"),sQuery(id+"F0.wireOp",EDGE,"E7"),sQuery(id+"F0.wireOp",EDGE,"E8.1.0"),sQuery(id+"F0.wireOp",EDGE,"E8.1.1"),sQuery(id+"F0.wireOp",EDGE,"E8.1.2"),sQuery(id+"F0.wireOp",EDGE,"E8.1.3"),sQuery(id+"F0.wireOp",EDGE,"E8.1.4"),sQuery(id+"F0.wireOp",EDGE,"E8.2.0"),sQuery(id+"F0.wireOp",EDGE,"E8.2.1"),sQuery(id+"F0.wireOp",EDGE,"E8.2.2"),sQuery(id+"F0.wireOp",EDGE,"E8.2.3"),sQuery(id+"F0.wireOp",EDGE,"E8.2.4"),sQuery(id+"F0.wireOp",EDGE,"E9.1.3.0"),sQuery(id+"F0.wireOp",EDGE,"E9.3.3.0"),sQuery(id+"F0.wireOp",EDGE,"E9.7.3.0"),sQuery(id+"F0.wireOp",EDGE,"E9.11.3.0"),sQuery(id+"F0.wireOp",EDGE,"E9.14.3.0"),sQuery(id+"F0.wireOp",EDGE,"E9.1.4.0"),sQuery(id+"F0.wireOp",EDGE,"E9.3.4.0"),sQuery(id+"F0.wireOp",EDGE,"E9.7.4.0"),sQuery(id+"F0.wireOp",EDGE,"E9.11.4.0"),sQuery(id+"F0.wireOp",EDGE,"E9.14.4.0"),sQuery(id+"F0.wireOp",EDGE,"E9.1.5.0"),sQuery(id+"F0.wireOp",EDGE,"E9.3.5.0"),sQuery(id+"F0.wireOp",EDGE,"E9.7.5.0"),sQuery(id+"F0.wireOp",EDGE,"E9.11.5.0"),sQuery(id+"F0.wireOp",EDGE,"E9.14.5.0"),sQuery(id+"F0.wireOp",EDGE,"E9.1.6.0"),sQuery(id+"F0.wireOp",EDGE,"E9.3.6.0"),sQuery(id+"F0.wireOp",EDGE,"E9.7.6.0"),sQuery(id+"F0.wireOp",EDGE,"E9.11.6.0"),sQuery(id+"F0.wireOp",EDGE,"E9.14.6.0"),sQuery(id+"F0.wireOp",EDGE,"E9.1.7.0"),sQuery(id+"F0.wireOp",EDGE,"E9.3.7.0"),sQuery(id+"F0.wireOp",EDGE,"E9.7.7.0"),sQuery(id+"F0.wireOp",EDGE,"E9.11.7.0"),sQuery(id+"F0.wireOp",EDGE,"E9.14.7.0"),sQuery(id+"F0.wireOp",EDGE,"E9.1.8.0"),sQuery(id+"F0.wireOp",EDGE,"E9.3.8.0"),sQuery(id+"F0.wireOp",EDGE,"E9.7.8.0"),sQuery(id+"F0.wireOp",EDGE,"E9.11.8.0"),sQuery(id+"F0.wireOp",EDGE,"E9.14.8.0"),sQuery(id+"F0.wireOp",EDGE,"E9.1.9.0"),sQuery(id+"F0.wireOp",EDGE,"E9.3.9.0"),sQuery(id+"F0.wireOp",EDGE,"E9.7.9.0"),sQuery(id+"F0.wireOp",EDGE,"E9.11.9.0"),sQuery(id+"F0.wireOp",EDGE,"E9.14.9.0"),sQuery(id+"F0.wireOp",EDGE,"E9.1.10.0"),sQuery(id+"F0.wireOp",EDGE,"E9.3.10.0"),sQuery(id+"F0.wireOp",EDGE,"E9.7.10.0"),sQuery(id+"F0.wireOp",EDGE,"E9.11.10.0"),sQuery(id+"F0.wireOp",EDGE,"E9.14.10.0"),sQuery(id+"F0.wireOp",EDGE,"E9.1.11.0"),sQuery(id+"F0.wireOp",EDGE,"E9.3.11.0"),sQuery(id+"F0.wireOp",EDGE,"E9.7.11.0"),sQuery(id+"F0.wireOp",EDGE,"E9.11.11.0"),sQuery(id+"F0.wireOp",EDGE,"E9.14.11.0"),sQuery(id+"F0.wireOp",EDGE,"E9.1.12.0"),sQuery(id+"F0.wireOp",EDGE,"E9.3.12.0"),sQuery(id+"F0.wireOp",EDGE,"E9.7.12.0"),sQuery(id+"F0.wireOp",EDGE,"E9.11.12.0"),sQuery(id+"F0.wireOp",EDGE,"E9.14.12.0"),sQuery(id+"F0.wireOp",EDGE,"E9.1.13.0"),sQuery(id+"F0.wireOp",EDGE,"E9.3.13.0"),sQuery(id+"F0.wireOp",EDGE,"E9.7.13.0"),sQuery(id+"F0.wireOp",EDGE,"E9.11.13.0"),sQuery(id+"F0.wireOp",EDGE,"E9.14.13.0"),sQuery(id+"F0.wireOp",EDGE,"E9.1.14.0"),sQuery(id+"F0.wireOp",EDGE,"E9.3.14.0"),sQuery(id+"F0.wireOp",EDGE,"E9.7.14.0"),sQuery(id+"F0.wireOp",EDGE,"E9.11.14.0"),sQuery(id+"F0.wireOp",EDGE,"E9.14.14.0"),sQuery(id+"F0.wireOp",EDGE,"E9.1.15.0"),sQuery(id+"F0.wireOp",EDGE,"E9.3.15.0"),sQuery(id+"F0.wireOp",EDGE,"E9.7.15.0"),sQuery(id+"F0.wireOp",EDGE,"E9.11.15.0"),sQuery(id+"F0.wireOp",EDGE,"E9.14.15.0"),sQuery(id+"F0.wireOp",EDGE,"E9.1.16.0"),sQuery(id+"F0.wireOp",EDGE,"E9.3.16.0"),sQuery(id+"F0.wireOp",EDGE,"E9.7.16.0"),sQuery(id+"F0.wireOp",EDGE,"E9.11.16.0"),sQuery(id+"F0.wireOp",EDGE,"E9.14.16.0"),sQuery(id+"F0.wireOp",EDGE,"E9.1.17.0"),sQuery(id+"F0.wireOp",EDGE,"E9.3.17.0"),sQuery(id+"F0.wireOp",EDGE,"E9.7.17.0"),sQuery(id+"F0.wireOp",EDGE,"E9.11.17.0"),sQuery(id+"F0.wireOp",EDGE,"E9.14.17.0"),sQuery(id+"F0.wireOp",EDGE,"E9.1.18.0"),sQuery(id+"F0.wireOp",EDGE,"E9.3.18.0"),sQuery(id+"F0.wireOp",EDGE,"E9.7.18.0"),sQuery(id+"F0.wireOp",EDGE,"E9.11.18.0"),sQuery(id+"F0.wireOp",EDGE,"E9.14.18.0"),sQuery(id+"F0.wireOp",EDGE,"E9.1.19.0"),sQuery(id+"F0.wireOp",EDGE,"E9.3.19.0"),sQuery(id+"F0.wireOp",EDGE,"E9.7.19.0"),sQuery(id+"F0.wireOp",EDGE,"E9.11.19.0"),sQuery(id+"F0.wireOp",EDGE,"E9.14.19.0"),sQuery(id+"F0.wireOp",EDGE,"E9.1.20.0"),sQuery(id+"F0.wireOp",EDGE,"E9.3.20.0"),sQuery(id+"F0.wireOp",EDGE,"E9.7.20.0"),sQuery(id+"F0.wireOp",EDGE,"E9.11.20.0"),sQuery(id+"F0.wireOp",EDGE,"E9.14.20.0"),sQuery(id+"F0.wireOp",EDGE,"E9.1.21.0"),sQuery(id+"F0.wireOp",EDGE,"E9.3.21.0"),sQuery(id+"F0.wireOp",EDGE,"E9.7.21.0"),sQuery(id+"F0.wireOp",EDGE,"E9.11.21.0"),sQuery(id+"F0.wireOp",EDGE,"E9.14.21.0"),sQuery(id+"F0.wireOp",EDGE,"E9.1.22.0"),sQuery(id+"F0.wireOp",EDGE,"E9.3.22.0"),sQuery(id+"F0.wireOp",EDGE,"E9.7.22.0"),sQuery(id+"F0.wireOp",EDGE,"E9.11.22.0"),sQuery(id+"F0.wireOp",EDGE,"E9.14.22.0"),sQuery(id+"F0.wireOp",EDGE,"E9.1.23.0"),sQuery(id+"F0.wireOp",EDGE,"E9.3.23.0"),sQuery(id+"F0.wireOp",EDGE,"E9.7.23.0"),sQuery(id+"F0.wireOp",EDGE,"E9.11.23.0"),sQuery(id+"F0.wireOp",EDGE,"E9.14.23.0"),sQuery(id+"F0.wireOp",EDGE,"E9.1.24.0"),sQuery(id+"F0.wireOp",EDGE,"E9.3.24.0"),sQuery(id+"F0.wireOp",EDGE,"E9.7.24.0"),sQuery(id+"F0.wireOp",EDGE,"E9.11.24.0"),sQuery(id+"F0.wireOp",EDGE,"E9.14.24.0"),sQuery(id+"F0.wireOp",EDGE,"E9.1.25.0"),sQuery(id+"F0.wireOp",EDGE,"E9.3.25.0"),sQuery(id+"F0.wireOp",EDGE,"E9.7.25.0"),sQuery(id+"F0.wireOp",EDGE,"E9.11.25.0"),sQuery(id+"F0.wireOp",EDGE,"E9.14.25.0"),sQuery(id+"F0.wireOp",EDGE,"E9.1.26.0"),sQuery(id+"F0.wireOp",EDGE,"E9.3.26.0"),sQuery(id+"F0.wireOp",EDGE,"E9.7.26.0"),sQuery(id+"F0.wireOp",EDGE,"E9.11.26.0"),sQuery(id+"F0.wireOp",EDGE,"E9.14.26.0"),sQuery(id+"F0.wireOp",EDGE,"E9.1.27.0"),sQuery(id+"F0.wireOp",EDGE,"E9.3.27.0"),sQuery(id+"F0.wireOp",EDGE,"E9.7.27.0"),sQuery(id+"F0.wireOp",EDGE,"E9.11.27.0"),sQuery(id+"F0.wireOp",EDGE,"E9.14.27.0"),sQuery(id+"F0.wireOp",EDGE,"E9.1.28.0"),sQuery(id+"F0.wireOp",EDGE,"E9.3.28.0"),sQuery(id+"F0.wireOp",EDGE,"E9.7.28.0"),sQuery(id+"F0.wireOp",EDGE,"E9.11.28.0"),sQuery(id+"F0.wireOp",EDGE,"E9.14.28.0"),sQuery(id+"F0.wireOp",EDGE,"E9.1.29.0"),sQuery(id+"F0.wireOp",EDGE,"E9.3.29.0"),sQuery(id+"F0.wireOp",EDGE,"E9.7.29.0"),sQuery(id+"F0.wireOp",EDGE,"E9.11.29.0"),sQuery(id+"F0.wireOp",EDGE,"E9.14.29.0"),sQuery(id+"F0.wireOp",EDGE,"E9.1.30.0"),sQuery(id+"F0.wireOp",EDGE,"E9.3.30.0"),sQuery(id+"F0.wireOp",EDGE,"E9.7.30.0"),sQuery(id+"F0.wireOp",EDGE,"E9.11.30.0"),sQuery(id+"F0.wireOp",EDGE,"E9.14.30.0"),sQuery(id+"F0.wireOp",EDGE,"E9.1.31.0"),sQuery(id+"F0.wireOp",EDGE,"E9.3.31.0"),sQuery(id+"F0.wireOp",EDGE,"E9.7.31.0"),sQuery(id+"F0.wireOp",EDGE,"E9.11.31.0"),sQuery(id+"F0.wireOp",EDGE,"E9.14.31.0"),sQuery(id+"F0.wireOp",EDGE,"E9.1.32.0"),sQuery(id+"F0.wireOp",EDGE,"E9.3.32.0"),sQuery(id+"F0.wireOp",EDGE,"E9.7.32.0"),sQuery(id+"F0.wireOp",EDGE,"E9.11.32.0"),sQuery(id+"F0.wireOp",EDGE,"E9.14.32.0"),sQuery(id+"F0.wireOp",EDGE,"E9.1.33.0"),sQuery(id+"F0.wireOp",EDGE,"E9.3.33.0"),sQuery(id+"F0.wireOp",EDGE,"E9.7.33.0"),sQuery(id+"F0.wireOp",EDGE,"E9.11.33.0"),sQuery(id+"F0.wireOp",EDGE,"E9.14.33.0"),sQuery(id+"F0.wireOp",EDGE,"E9.1.34.0"),sQuery(id+"F0.wireOp",EDGE,"E9.3.34.0"),sQuery(id+"F0.wireOp",EDGE,"E9.7.34.0"),sQuery(id+"F0.wireOp",EDGE,"E9.11.34.0"),sQuery(id+"F0.wireOp",EDGE,"E9.14.34.0"),sQuery(id+"F0.wireOp",EDGE,"E9.1.35.0"),sQuery(id+"F0.wireOp",EDGE,"E9.3.35.0"),sQuery(id+"F0.wireOp",EDGE,"E9.7.35.0"),sQuery(id+"F0.wireOp",EDGE,"E9.11.35.0"),sQuery(id+"F0.wireOp",EDGE,"E9.14.35.0"),sQuery(id+"F0.wireOp",EDGE,"E9.1.36.0"),sQuery(id+"F0.wireOp",EDGE,"E9.3.36.0"),sQuery(id+"F0.wireOp",EDGE,"E9.7.36.0"),sQuery(id+"F0.wireOp",EDGE,"E9.11.36.0"),sQuery(id+"F0.wireOp",EDGE,"E9.14.36.0"),sQuery(id+"F0.wireOp",EDGE,"E9.1.37.0"),sQuery(id+"F0.wireOp",EDGE,"E9.3.37.0"),sQuery(id+"F0.wireOp",EDGE,"E9.7.37.0"),sQuery(id+"F0.wireOp",EDGE,"E9.11.37.0"),sQuery(id+"F0.wireOp",EDGE,"E9.14.37.0"),sQuery(id+"F0.wireOp",EDGE,"E9.1.38.0"),sQuery(id+"F0.wireOp",EDGE,"E9.3.38.0"),sQuery(id+"F0.wireOp",EDGE,"E9.7.38.0"),sQuery(id+"F0.wireOp",EDGE,"E9.11.38.0"),sQuery(id+"F0.wireOp",EDGE,"E9.14.38.0"),sQuery(id+"F0.wireOp",EDGE,"E9.1.39.0"),sQuery(id+"F0.wireOp",EDGE,"E9.3.39.0"),sQuery(id+"F0.wireOp",EDGE,"E9.7.39.0"),sQuery(id+"F0.wireOp",EDGE,"E9.11.39.0"),sQuery(id+"F0.wireOp",EDGE,"E9.14.39.0"),sQuery(id+"F0.wireOp",EDGE,"E9.1.40.0"),sQuery(id+"F0.wireOp",EDGE,"E9.3.40.0"),sQuery(id+"F0.wireOp",EDGE,"E9.7.40.0"),sQuery(id+"F0.wireOp",EDGE,"E9.11.40.0"),sQuery(id+"F0.wireOp",EDGE,"E9.14.40.0"),sQuery(id+"F0.wireOp",EDGE,"E9.1.41.0"),sQuery(id+"F0.wireOp",EDGE,"E9.3.41.0"),sQuery(id+"F0.wireOp",EDGE,"E9.7.41.0"),sQuery(id+"F0.wireOp",EDGE,"E9.11.41.0"),sQuery(id+"F0.wireOp",EDGE,"E9.14.41.0"),sQuery(id+"F0.wireOp",EDGE,"E9.1.42.0"),sQuery(id+"F0.wireOp",EDGE,"E9.3.42.0"),sQuery(id+"F0.wireOp",EDGE,"E9.7.42.0"),sQuery(id+"F0.wireOp",EDGE,"E9.11.42.0"),sQuery(id+"F0.wireOp",EDGE,"E9.14.42.0"),sQuery(id+"F0.wireOp",EDGE,"E9.1.43.0"),sQuery(id+"F0.wireOp",EDGE,"E9.3.43.0"),sQuery(id+"F0.wireOp",EDGE,"E9.7.43.0"),sQuery(id+"F0.wireOp",EDGE,"E9.11.43.0"),sQuery(id+"F0.wireOp",EDGE,"E9.14.43.0"),sQuery(id+"F0.wireOp",EDGE,"E9.1.44.0"),sQuery(id+"F0.wireOp",EDGE,"E9.3.44.0"),sQuery(id+"F0.wireOp",EDGE,"E9.7.44.0"),sQuery(id+"F0.wireOp",EDGE,"E9.11.44.0"),sQuery(id+"F0.wireOp",EDGE,"E9.14.44.0"),sQuery(id+"F0.wireOp",EDGE,"E9.1.45.0"),sQuery(id+"F0.wireOp",EDGE,"E9.3.45.0"),sQuery(id+"F0.wireOp",EDGE,"E9.7.45.0"),sQuery(id+"F0.wireOp",EDGE,"E9.11.45.0"),sQuery(id+"F0.wireOp",EDGE,"E9.14.45.0"),sQuery(id+"F0.wireOp",EDGE,"E9.1.46.0"),sQuery(id+"F0.wireOp",EDGE,"E9.3.46.0"),sQuery(id+"F0.wireOp",EDGE,"E9.7.46.0"),sQuery(id+"F0.wireOp",EDGE,"E9.11.46.0"),sQuery(id+"F0.wireOp",EDGE,"E9.14.46.0"),sQuery(id+"F0.wireOp",EDGE,"E9.1.47.0"),sQuery(id+"F0.wireOp",EDGE,"E9.3.47.0"),sQuery(id+"F0.wireOp",EDGE,"E9.7.47.0"),sQuery(id+"F0.wireOp",EDGE,"E9.11.47.0"),sQuery(id+"F0.wireOp",EDGE,"E9.14.47.0"),sQuery(id+"F0.wireOp",EDGE,"E9.1.48.0"),sQuery(id+"F0.wireOp",EDGE,"E9.3.48.0"),sQuery(id+"F0.wireOp",EDGE,"E9.7.48.0"),sQuery(id+"F0.wireOp",EDGE,"E9.11.48.0"),sQuery(id+"F0.wireOp",EDGE,"E9.14.48.0"),sQuery(id+"F0.wireOp",EDGE,"E9.1.49.0"),sQuery(id+"F0.wireOp",EDGE,"E9.3.49.0"),sQuery(id+"F0.wireOp",EDGE,"E9.7.49.0"),sQuery(id+"F0.wireOp",EDGE,"E9.11.49.0"),sQuery(id+"F0.wireOp",EDGE,"E9.14.49.0"),sQuery(id+"F0.wireOp",EDGE,"E9.1.50.0"),sQuery(id+"F0.wireOp",EDGE,"E9.3.50.0"),sQuery(id+"F0.wireOp",EDGE,"E9.7.50.0"),sQuery(id+"F0.wireOp",EDGE,"E9.11.50.0"),sQuery(id+"F0.wireOp",EDGE,"E9.14.50.0"),sQuery(id+"F0.wireOp",EDGE,"E9.1.51.0"),sQuery(id+"F0.wireOp",EDGE,"E9.3.51.0"),sQuery(id+"F0.wireOp",EDGE,"E9.7.51.0"),sQuery(id+"F0.wireOp",EDGE,"E9.11.51.0"),sQuery(id+"F0.wireOp",EDGE,"E9.14.51.0"),sQuery(id+"F0.wireOp",EDGE,"E9.1.52.0"),sQuery(id+"F0.wireOp",EDGE,"E9.3.52.0"),sQuery(id+"F0.wireOp",EDGE,"E9.7.52.0"),sQuery(id+"F0.wireOp",EDGE,"E9.11.52.0"),sQuery(id+"F0.wireOp",EDGE,"E9.14.52.0"),sQuery(id+"F0.wireOp",EDGE,"E9.1.53.0"),sQuery(id+"F0.wireOp",EDGE,"E9.3.53.0"),sQuery(id+"F0.wireOp",EDGE,"E9.7.53.0"),sQuery(id+"F0.wireOp",EDGE,"E9.11.53.0"),sQuery(id+"F0.wireOp",EDGE,"E9.14.53.0"),sQuery(id+"F0.wireOp",EDGE,"E9.1.54.0"),sQuery(id+"F0.wireOp",EDGE,"E9.3.54.0"),sQuery(id+"F0.wireOp",EDGE,"E9.7.54.0"),sQuery(id+"F0.wireOp",EDGE,"E9.11.54.0"),sQuery(id+"F0.wireOp",EDGE,"E9.14.54.0"),sQuery(id+"F0.wireOp",EDGE,"E9.1.55.0"),sQuery(id+"F0.wireOp",EDGE,"E9.3.55.0"),sQuery(id+"F0.wireOp",EDGE,"E9.7.55.0"),sQuery(id+"F0.wireOp",EDGE,"E9.11.55.0"),sQuery(id+"F0.wireOp",EDGE,"E9.14.55.0"),sQuery(id+"F0.wireOp",EDGE,"E9.1.56.0"),sQuery(id+"F0.wireOp",EDGE,"E9.3.56.0"),sQuery(id+"F0.wireOp",EDGE,"E9.7.56.0"),sQuery(id+"F0.wireOp",EDGE,"E9.11.56.0"),sQuery(id+"F0.wireOp",EDGE,"E9.14.56.0"),sQuery(id+"F0.wireOp",EDGE,"E9.1.57.0"),sQuery(id+"F0.wireOp",EDGE,"E9.3.57.0"),sQuery(id+"F0.wireOp",EDGE,"E9.7.57.0"),sQuery(id+"F0.wireOp",EDGE,"E9.11.57.0"),sQuery(id+"F0.wireOp",EDGE,"E9.14.57.0"),sQuery(id+"F0.wireOp",EDGE,"E9.1.58.0"),sQuery(id+"F0.wireOp",EDGE,"E9.3.58.0"),sQuery(id+"F0.wireOp",EDGE,"E9.7.58.0"),sQuery(id+"F0.wireOp",EDGE,"E9.11.58.0"),sQuery(id+"F0.wireOp",EDGE,"E9.14.58.0"),sQuery(id+"F0.wireOp",EDGE,"E9.1.59.0"),sQuery(id+"F0.wireOp",EDGE,"E9.3.59.0"),sQuery(id+"F0.wireOp",EDGE,"E9.7.59.0"),sQuery(id+"F0.wireOp",EDGE,"E9.11.59.0"),sQuery(id+"F0.wireOp",EDGE,"E9.14.59.0"),sQuery(id+"F2.wireOp",EDGE,"E20.0")])],"isStart":false})});
            var Q3;
            Q3=makeQuery(id+"F8.boolean.opBoolean","COPY",EDGE,{"derivedFrom":makeQuery(id+"F8.opExtrude","CAP_EDGE",EDGE,{"disambiguationData":[OSD([sQuery(id+"F0.wireOp",EDGE,"E0"),sQuery(id+"F0.wireOp",EDGE,"E1"),sQuery(id+"F0.wireOp",EDGE,"E3"),sQuery(id+"F0.wireOp",EDGE,"E4"),sQuery(id+"F0.wireOp",EDGE,"E5"),sQuery(id+"F0.wireOp",EDGE,"E6.trimOffspring"),sQuery(id+"F0.wireOp",EDGE,"E7"),sQuery(id+"F0.wireOp",EDGE,"E8.1.0"),sQuery(id+"F0.wireOp",EDGE,"E8.1.1"),sQuery(id+"F0.wireOp",EDGE,"E8.1.2"),sQuery(id+"F0.wireOp",EDGE,"E8.1.3"),sQuery(id+"F0.wireOp",EDGE,"E8.1.4"),sQuery(id+"F0.wireOp",EDGE,"E8.2.0"),sQuery(id+"F0.wireOp",EDGE,"E8.2.1"),sQuery(id+"F0.wireOp",EDGE,"E8.2.2"),sQuery(id+"F0.wireOp",EDGE,"E8.2.3"),sQuery(id+"F0.wireOp",EDGE,"E8.2.4"),sQuery(id+"F0.wireOp",EDGE,"E9.1.3.0"),sQuery(id+"F0.wireOp",EDGE,"E9.3.3.0"),sQuery(id+"F0.wireOp",EDGE,"E9.7.3.0"),sQuery(id+"F0.wireOp",EDGE,"E9.11.3.0"),sQuery(id+"F0.wireOp",EDGE,"E9.14.3.0"),sQuery(id+"F0.wireOp",EDGE,"E9.1.4.0"),sQuery(id+"F0.wireOp",EDGE,"E9.3.4.0"),sQuery(id+"F0.wireOp",EDGE,"E9.7.4.0"),sQuery(id+"F0.wireOp",EDGE,"E9.11.4.0"),sQuery(id+"F0.wireOp",EDGE,"E9.14.4.0"),sQuery(id+"F0.wireOp",EDGE,"E9.1.5.0"),sQuery(id+"F0.wireOp",EDGE,"E9.3.5.0"),sQuery(id+"F0.wireOp",EDGE,"E9.7.5.0"),sQuery(id+"F0.wireOp",EDGE,"E9.11.5.0"),sQuery(id+"F0.wireOp",EDGE,"E9.14.5.0"),sQuery(id+"F0.wireOp",EDGE,"E9.1.6.0"),sQuery(id+"F0.wireOp",EDGE,"E9.3.6.0"),sQuery(id+"F0.wireOp",EDGE,"E9.7.6.0"),sQuery(id+"F0.wireOp",EDGE,"E9.11.6.0"),sQuery(id+"F0.wireOp",EDGE,"E9.14.6.0"),sQuery(id+"F0.wireOp",EDGE,"E9.1.7.0"),sQuery(id+"F0.wireOp",EDGE,"E9.3.7.0"),sQuery(id+"F0.wireOp",EDGE,"E9.7.7.0"),sQuery(id+"F0.wireOp",EDGE,"E9.11.7.0"),sQuery(id+"F0.wireOp",EDGE,"E9.14.7.0"),sQuery(id+"F0.wireOp",EDGE,"E9.1.8.0"),sQuery(id+"F0.wireOp",EDGE,"E9.3.8.0"),sQuery(id+"F0.wireOp",EDGE,"E9.7.8.0"),sQuery(id+"F0.wireOp",EDGE,"E9.11.8.0"),sQuery(id+"F0.wireOp",EDGE,"E9.14.8.0"),sQuery(id+"F0.wireOp",EDGE,"E9.1.9.0"),sQuery(id+"F0.wireOp",EDGE,"E9.3.9.0"),sQuery(id+"F0.wireOp",EDGE,"E9.7.9.0"),sQuery(id+"F0.wireOp",EDGE,"E9.11.9.0"),sQuery(id+"F0.wireOp",EDGE,"E9.14.9.0"),sQuery(id+"F0.wireOp",EDGE,"E9.1.10.0"),sQuery(id+"F0.wireOp",EDGE,"E9.3.10.0"),sQuery(id+"F0.wireOp",EDGE,"E9.7.10.0"),sQuery(id+"F0.wireOp",EDGE,"E9.11.10.0"),sQuery(id+"F0.wireOp",EDGE,"E9.14.10.0"),sQuery(id+"F0.wireOp",EDGE,"E9.1.11.0"),sQuery(id+"F0.wireOp",EDGE,"E9.3.11.0"),sQuery(id+"F0.wireOp",EDGE,"E9.7.11.0"),sQuery(id+"F0.wireOp",EDGE,"E9.11.11.0"),sQuery(id+"F0.wireOp",EDGE,"E9.14.11.0"),sQuery(id+"F0.wireOp",EDGE,"E9.1.12.0"),sQuery(id+"F0.wireOp",EDGE,"E9.3.12.0"),sQuery(id+"F0.wireOp",EDGE,"E9.7.12.0"),sQuery(id+"F0.wireOp",EDGE,"E9.11.12.0"),sQuery(id+"F0.wireOp",EDGE,"E9.14.12.0"),sQuery(id+"F0.wireOp",EDGE,"E9.1.13.0"),sQuery(id+"F0.wireOp",EDGE,"E9.3.13.0"),sQuery(id+"F0.wireOp",EDGE,"E9.7.13.0"),sQuery(id+"F0.wireOp",EDGE,"E9.11.13.0"),sQuery(id+"F0.wireOp",EDGE,"E9.14.13.0"),sQuery(id+"F0.wireOp",EDGE,"E9.1.14.0"),sQuery(id+"F0.wireOp",EDGE,"E9.3.14.0"),sQuery(id+"F0.wireOp",EDGE,"E9.7.14.0"),sQuery(id+"F0.wireOp",EDGE,"E9.11.14.0"),sQuery(id+"F0.wireOp",EDGE,"E9.14.14.0"),sQuery(id+"F0.wireOp",EDGE,"E9.1.15.0"),sQuery(id+"F0.wireOp",EDGE,"E9.3.15.0"),sQuery(id+"F0.wireOp",EDGE,"E9.7.15.0"),sQuery(id+"F0.wireOp",EDGE,"E9.11.15.0"),sQuery(id+"F0.wireOp",EDGE,"E9.14.15.0"),sQuery(id+"F0.wireOp",EDGE,"E9.1.16.0"),sQuery(id+"F0.wireOp",EDGE,"E9.3.16.0"),sQuery(id+"F0.wireOp",EDGE,"E9.7.16.0"),sQuery(id+"F0.wireOp",EDGE,"E9.11.16.0"),sQuery(id+"F0.wireOp",EDGE,"E9.14.16.0"),sQuery(id+"F0.wireOp",EDGE,"E9.1.17.0"),sQuery(id+"F0.wireOp",EDGE,"E9.3.17.0"),sQuery(id+"F0.wireOp",EDGE,"E9.7.17.0"),sQuery(id+"F0.wireOp",EDGE,"E9.11.17.0"),sQuery(id+"F0.wireOp",EDGE,"E9.14.17.0"),sQuery(id+"F0.wireOp",EDGE,"E9.1.18.0"),sQuery(id+"F0.wireOp",EDGE,"E9.3.18.0"),sQuery(id+"F0.wireOp",EDGE,"E9.7.18.0"),sQuery(id+"F0.wireOp",EDGE,"E9.11.18.0"),sQuery(id+"F0.wireOp",EDGE,"E9.14.18.0"),sQuery(id+"F0.wireOp",EDGE,"E9.1.19.0"),sQuery(id+"F0.wireOp",EDGE,"E9.3.19.0"),sQuery(id+"F0.wireOp",EDGE,"E9.7.19.0"),sQuery(id+"F0.wireOp",EDGE,"E9.11.19.0"),sQuery(id+"F0.wireOp",EDGE,"E9.14.19.0"),sQuery(id+"F0.wireOp",EDGE,"E9.1.20.0"),sQuery(id+"F0.wireOp",EDGE,"E9.3.20.0"),sQuery(id+"F0.wireOp",EDGE,"E9.7.20.0"),sQuery(id+"F0.wireOp",EDGE,"E9.11.20.0"),sQuery(id+"F0.wireOp",EDGE,"E9.14.20.0"),sQuery(id+"F0.wireOp",EDGE,"E9.1.21.0"),sQuery(id+"F0.wireOp",EDGE,"E9.3.21.0"),sQuery(id+"F0.wireOp",EDGE,"E9.7.21.0"),sQuery(id+"F0.wireOp",EDGE,"E9.11.21.0"),sQuery(id+"F0.wireOp",EDGE,"E9.14.21.0"),sQuery(id+"F0.wireOp",EDGE,"E9.1.22.0"),sQuery(id+"F0.wireOp",EDGE,"E9.3.22.0"),sQuery(id+"F0.wireOp",EDGE,"E9.7.22.0"),sQuery(id+"F0.wireOp",EDGE,"E9.11.22.0"),sQuery(id+"F0.wireOp",EDGE,"E9.14.22.0"),sQuery(id+"F0.wireOp",EDGE,"E9.1.23.0"),sQuery(id+"F0.wireOp",EDGE,"E9.3.23.0"),sQuery(id+"F0.wireOp",EDGE,"E9.7.23.0"),sQuery(id+"F0.wireOp",EDGE,"E9.11.23.0"),sQuery(id+"F0.wireOp",EDGE,"E9.14.23.0"),sQuery(id+"F0.wireOp",EDGE,"E9.1.24.0"),sQuery(id+"F0.wireOp",EDGE,"E9.3.24.0"),sQuery(id+"F0.wireOp",EDGE,"E9.7.24.0"),sQuery(id+"F0.wireOp",EDGE,"E9.11.24.0"),sQuery(id+"F0.wireOp",EDGE,"E9.14.24.0"),sQuery(id+"F0.wireOp",EDGE,"E9.1.25.0"),sQuery(id+"F0.wireOp",EDGE,"E9.3.25.0"),sQuery(id+"F0.wireOp",EDGE,"E9.7.25.0"),sQuery(id+"F0.wireOp",EDGE,"E9.11.25.0"),sQuery(id+"F0.wireOp",EDGE,"E9.14.25.0"),sQuery(id+"F0.wireOp",EDGE,"E9.1.26.0"),sQuery(id+"F0.wireOp",EDGE,"E9.3.26.0"),sQuery(id+"F0.wireOp",EDGE,"E9.7.26.0"),sQuery(id+"F0.wireOp",EDGE,"E9.11.26.0"),sQuery(id+"F0.wireOp",EDGE,"E9.14.26.0"),sQuery(id+"F0.wireOp",EDGE,"E9.1.27.0"),sQuery(id+"F0.wireOp",EDGE,"E9.3.27.0"),sQuery(id+"F0.wireOp",EDGE,"E9.7.27.0"),sQuery(id+"F0.wireOp",EDGE,"E9.11.27.0"),sQuery(id+"F0.wireOp",EDGE,"E9.14.27.0"),sQuery(id+"F0.wireOp",EDGE,"E9.1.28.0"),sQuery(id+"F0.wireOp",EDGE,"E9.3.28.0"),sQuery(id+"F0.wireOp",EDGE,"E9.7.28.0"),sQuery(id+"F0.wireOp",EDGE,"E9.11.28.0"),sQuery(id+"F0.wireOp",EDGE,"E9.14.28.0"),sQuery(id+"F0.wireOp",EDGE,"E9.1.29.0"),sQuery(id+"F0.wireOp",EDGE,"E9.3.29.0"),sQuery(id+"F0.wireOp",EDGE,"E9.7.29.0"),sQuery(id+"F0.wireOp",EDGE,"E9.11.29.0"),sQuery(id+"F0.wireOp",EDGE,"E9.14.29.0"),sQuery(id+"F0.wireOp",EDGE,"E9.1.30.0"),sQuery(id+"F0.wireOp",EDGE,"E9.3.30.0"),sQuery(id+"F0.wireOp",EDGE,"E9.7.30.0"),sQuery(id+"F0.wireOp",EDGE,"E9.11.30.0"),sQuery(id+"F0.wireOp",EDGE,"E9.14.30.0"),sQuery(id+"F0.wireOp",EDGE,"E9.1.31.0"),sQuery(id+"F0.wireOp",EDGE,"E9.3.31.0"),sQuery(id+"F0.wireOp",EDGE,"E9.7.31.0"),sQuery(id+"F0.wireOp",EDGE,"E9.11.31.0"),sQuery(id+"F0.wireOp",EDGE,"E9.14.31.0"),sQuery(id+"F0.wireOp",EDGE,"E9.1.32.0"),sQuery(id+"F0.wireOp",EDGE,"E9.3.32.0"),sQuery(id+"F0.wireOp",EDGE,"E9.7.32.0"),sQuery(id+"F0.wireOp",EDGE,"E9.11.32.0"),sQuery(id+"F0.wireOp",EDGE,"E9.14.32.0"),sQuery(id+"F0.wireOp",EDGE,"E9.1.33.0"),sQuery(id+"F0.wireOp",EDGE,"E9.3.33.0"),sQuery(id+"F0.wireOp",EDGE,"E9.7.33.0"),sQuery(id+"F0.wireOp",EDGE,"E9.11.33.0"),sQuery(id+"F0.wireOp",EDGE,"E9.14.33.0"),sQuery(id+"F0.wireOp",EDGE,"E9.1.34.0"),sQuery(id+"F0.wireOp",EDGE,"E9.3.34.0"),sQuery(id+"F0.wireOp",EDGE,"E9.7.34.0"),sQuery(id+"F0.wireOp",EDGE,"E9.11.34.0"),sQuery(id+"F0.wireOp",EDGE,"E9.14.34.0"),sQuery(id+"F0.wireOp",EDGE,"E9.1.35.0"),sQuery(id+"F0.wireOp",EDGE,"E9.3.35.0"),sQuery(id+"F0.wireOp",EDGE,"E9.7.35.0"),sQuery(id+"F0.wireOp",EDGE,"E9.11.35.0"),sQuery(id+"F0.wireOp",EDGE,"E9.14.35.0"),sQuery(id+"F0.wireOp",EDGE,"E9.1.36.0"),sQuery(id+"F0.wireOp",EDGE,"E9.3.36.0"),sQuery(id+"F0.wireOp",EDGE,"E9.7.36.0"),sQuery(id+"F0.wireOp",EDGE,"E9.11.36.0"),sQuery(id+"F0.wireOp",EDGE,"E9.14.36.0"),sQuery(id+"F0.wireOp",EDGE,"E9.1.37.0"),sQuery(id+"F0.wireOp",EDGE,"E9.3.37.0"),sQuery(id+"F0.wireOp",EDGE,"E9.7.37.0"),sQuery(id+"F0.wireOp",EDGE,"E9.11.37.0"),sQuery(id+"F0.wireOp",EDGE,"E9.14.37.0"),sQuery(id+"F0.wireOp",EDGE,"E9.1.38.0"),sQuery(id+"F0.wireOp",EDGE,"E9.3.38.0"),sQuery(id+"F0.wireOp",EDGE,"E9.7.38.0"),sQuery(id+"F0.wireOp",EDGE,"E9.11.38.0"),sQuery(id+"F0.wireOp",EDGE,"E9.14.38.0"),sQuery(id+"F0.wireOp",EDGE,"E9.1.39.0"),sQuery(id+"F0.wireOp",EDGE,"E9.3.39.0"),sQuery(id+"F0.wireOp",EDGE,"E9.7.39.0"),sQuery(id+"F0.wireOp",EDGE,"E9.11.39.0"),sQuery(id+"F0.wireOp",EDGE,"E9.14.39.0"),sQuery(id+"F0.wireOp",EDGE,"E9.1.40.0"),sQuery(id+"F0.wireOp",EDGE,"E9.3.40.0"),sQuery(id+"F0.wireOp",EDGE,"E9.7.40.0"),sQuery(id+"F0.wireOp",EDGE,"E9.11.40.0"),sQuery(id+"F0.wireOp",EDGE,"E9.14.40.0"),sQuery(id+"F0.wireOp",EDGE,"E9.1.41.0"),sQuery(id+"F0.wireOp",EDGE,"E9.3.41.0"),sQuery(id+"F0.wireOp",EDGE,"E9.7.41.0"),sQuery(id+"F0.wireOp",EDGE,"E9.11.41.0"),sQuery(id+"F0.wireOp",EDGE,"E9.14.41.0"),sQuery(id+"F0.wireOp",EDGE,"E9.1.42.0"),sQuery(id+"F0.wireOp",EDGE,"E9.3.42.0"),sQuery(id+"F0.wireOp",EDGE,"E9.7.42.0"),sQuery(id+"F0.wireOp",EDGE,"E9.11.42.0"),sQuery(id+"F0.wireOp",EDGE,"E9.14.42.0"),sQuery(id+"F0.wireOp",EDGE,"E9.1.43.0"),sQuery(id+"F0.wireOp",EDGE,"E9.3.43.0"),sQuery(id+"F0.wireOp",EDGE,"E9.7.43.0"),sQuery(id+"F0.wireOp",EDGE,"E9.11.43.0"),sQuery(id+"F0.wireOp",EDGE,"E9.14.43.0"),sQuery(id+"F0.wireOp",EDGE,"E9.1.44.0"),sQuery(id+"F0.wireOp",EDGE,"E9.3.44.0"),sQuery(id+"F0.wireOp",EDGE,"E9.7.44.0"),sQuery(id+"F0.wireOp",EDGE,"E9.11.44.0"),sQuery(id+"F0.wireOp",EDGE,"E9.14.44.0"),sQuery(id+"F0.wireOp",EDGE,"E9.1.45.0"),sQuery(id+"F0.wireOp",EDGE,"E9.3.45.0"),sQuery(id+"F0.wireOp",EDGE,"E9.7.45.0"),sQuery(id+"F0.wireOp",EDGE,"E9.11.45.0"),sQuery(id+"F0.wireOp",EDGE,"E9.14.45.0"),sQuery(id+"F0.wireOp",EDGE,"E9.1.46.0"),sQuery(id+"F0.wireOp",EDGE,"E9.3.46.0"),sQuery(id+"F0.wireOp",EDGE,"E9.7.46.0"),sQuery(id+"F0.wireOp",EDGE,"E9.11.46.0"),sQuery(id+"F0.wireOp",EDGE,"E9.14.46.0"),sQuery(id+"F0.wireOp",EDGE,"E9.1.47.0"),sQuery(id+"F0.wireOp",EDGE,"E9.3.47.0"),sQuery(id+"F0.wireOp",EDGE,"E9.7.47.0"),sQuery(id+"F0.wireOp",EDGE,"E9.11.47.0"),sQuery(id+"F0.wireOp",EDGE,"E9.14.47.0"),sQuery(id+"F0.wireOp",EDGE,"E9.1.48.0"),sQuery(id+"F0.wireOp",EDGE,"E9.3.48.0"),sQuery(id+"F0.wireOp",EDGE,"E9.7.48.0"),sQuery(id+"F0.wireOp",EDGE,"E9.11.48.0"),sQuery(id+"F0.wireOp",EDGE,"E9.14.48.0"),sQuery(id+"F0.wireOp",EDGE,"E9.1.49.0"),sQuery(id+"F0.wireOp",EDGE,"E9.3.49.0"),sQuery(id+"F0.wireOp",EDGE,"E9.7.49.0"),sQuery(id+"F0.wireOp",EDGE,"E9.11.49.0"),sQuery(id+"F0.wireOp",EDGE,"E9.14.49.0"),sQuery(id+"F0.wireOp",EDGE,"E9.1.50.0"),sQuery(id+"F0.wireOp",EDGE,"E9.3.50.0"),sQuery(id+"F0.wireOp",EDGE,"E9.7.50.0"),sQuery(id+"F0.wireOp",EDGE,"E9.11.50.0"),sQuery(id+"F0.wireOp",EDGE,"E9.14.50.0"),sQuery(id+"F0.wireOp",EDGE,"E9.1.51.0"),sQuery(id+"F0.wireOp",EDGE,"E9.3.51.0"),sQuery(id+"F0.wireOp",EDGE,"E9.7.51.0"),sQuery(id+"F0.wireOp",EDGE,"E9.11.51.0"),sQuery(id+"F0.wireOp",EDGE,"E9.14.51.0"),sQuery(id+"F0.wireOp",EDGE,"E9.1.52.0"),sQuery(id+"F0.wireOp",EDGE,"E9.3.52.0"),sQuery(id+"F0.wireOp",EDGE,"E9.7.52.0"),sQuery(id+"F0.wireOp",EDGE,"E9.11.52.0"),sQuery(id+"F0.wireOp",EDGE,"E9.14.52.0"),sQuery(id+"F0.wireOp",EDGE,"E9.1.53.0"),sQuery(id+"F0.wireOp",EDGE,"E9.3.53.0"),sQuery(id+"F0.wireOp",EDGE,"E9.7.53.0"),sQuery(id+"F0.wireOp",EDGE,"E9.11.53.0"),sQuery(id+"F0.wireOp",EDGE,"E9.14.53.0"),sQuery(id+"F0.wireOp",EDGE,"E9.1.54.0"),sQuery(id+"F0.wireOp",EDGE,"E9.3.54.0"),sQuery(id+"F0.wireOp",EDGE,"E9.7.54.0"),sQuery(id+"F0.wireOp",EDGE,"E9.11.54.0"),sQuery(id+"F0.wireOp",EDGE,"E9.14.54.0"),sQuery(id+"F0.wireOp",EDGE,"E9.1.55.0"),sQuery(id+"F0.wireOp",EDGE,"E9.3.55.0"),sQuery(id+"F0.wireOp",EDGE,"E9.7.55.0"),sQuery(id+"F0.wireOp",EDGE,"E9.11.55.0"),sQuery(id+"F0.wireOp",EDGE,"E9.14.55.0"),sQuery(id+"F0.wireOp",EDGE,"E9.1.56.0"),sQuery(id+"F0.wireOp",EDGE,"E9.3.56.0"),sQuery(id+"F0.wireOp",EDGE,"E9.7.56.0"),sQuery(id+"F0.wireOp",EDGE,"E9.11.56.0"),sQuery(id+"F0.wireOp",EDGE,"E9.14.56.0"),sQuery(id+"F0.wireOp",EDGE,"E9.1.57.0"),sQuery(id+"F0.wireOp",EDGE,"E9.3.57.0"),sQuery(id+"F0.wireOp",EDGE,"E9.7.57.0"),sQuery(id+"F0.wireOp",EDGE,"E9.11.57.0"),sQuery(id+"F0.wireOp",EDGE,"E9.14.57.0"),sQuery(id+"F0.wireOp",EDGE,"E9.1.58.0"),sQuery(id+"F0.wireOp",EDGE,"E9.3.58.0"),sQuery(id+"F0.wireOp",EDGE,"E9.7.58.0"),sQuery(id+"F0.wireOp",EDGE,"E9.11.58.0"),sQuery(id+"F0.wireOp",EDGE,"E9.14.58.0"),sQuery(id+"F0.wireOp",EDGE,"E9.1.59.0"),sQuery(id+"F0.wireOp",EDGE,"E9.3.59.0"),sQuery(id+"F0.wireOp",EDGE,"E9.7.59.0"),sQuery(id+"F0.wireOp",EDGE,"E9.11.59.0"),sQuery(id+"F0.wireOp",EDGE,"E9.14.59.0"),sQuery(id+"F2.wireOp",EDGE,"E26")])],"isStart":false})});
            var Q4;
            Q4=makeQuery(id+"F8.boolean.opBoolean","COPY",EDGE,{"derivedFrom":makeQuery(id+"F8.opExtrude","CAP_EDGE",EDGE,{"disambiguationData":[OSD([sQuery(id+"F0.wireOp",EDGE,"E0"),sQuery(id+"F0.wireOp",EDGE,"E1"),sQuery(id+"F0.wireOp",EDGE,"E3"),sQuery(id+"F0.wireOp",EDGE,"E4"),sQuery(id+"F0.wireOp",EDGE,"E5"),sQuery(id+"F0.wireOp",EDGE,"E6.trimOffspring"),sQuery(id+"F0.wireOp",EDGE,"E7"),sQuery(id+"F0.wireOp",EDGE,"E8.1.0"),sQuery(id+"F0.wireOp",EDGE,"E8.1.1"),sQuery(id+"F0.wireOp",EDGE,"E8.1.2"),sQuery(id+"F0.wireOp",EDGE,"E8.1.3"),sQuery(id+"F0.wireOp",EDGE,"E8.1.4"),sQuery(id+"F0.wireOp",EDGE,"E8.2.0"),sQuery(id+"F0.wireOp",EDGE,"E8.2.1"),sQuery(id+"F0.wireOp",EDGE,"E8.2.2"),sQuery(id+"F0.wireOp",EDGE,"E8.2.3"),sQuery(id+"F0.wireOp",EDGE,"E8.2.4"),sQuery(id+"F0.wireOp",EDGE,"E9.1.3.0"),sQuery(id+"F0.wireOp",EDGE,"E9.3.3.0"),sQuery(id+"F0.wireOp",EDGE,"E9.7.3.0"),sQuery(id+"F0.wireOp",EDGE,"E9.11.3.0"),sQuery(id+"F0.wireOp",EDGE,"E9.14.3.0"),sQuery(id+"F0.wireOp",EDGE,"E9.1.4.0"),sQuery(id+"F0.wireOp",EDGE,"E9.3.4.0"),sQuery(id+"F0.wireOp",EDGE,"E9.7.4.0"),sQuery(id+"F0.wireOp",EDGE,"E9.11.4.0"),sQuery(id+"F0.wireOp",EDGE,"E9.14.4.0"),sQuery(id+"F0.wireOp",EDGE,"E9.1.5.0"),sQuery(id+"F0.wireOp",EDGE,"E9.3.5.0"),sQuery(id+"F0.wireOp",EDGE,"E9.7.5.0"),sQuery(id+"F0.wireOp",EDGE,"E9.11.5.0"),sQuery(id+"F0.wireOp",EDGE,"E9.14.5.0"),sQuery(id+"F0.wireOp",EDGE,"E9.1.6.0"),sQuery(id+"F0.wireOp",EDGE,"E9.3.6.0"),sQuery(id+"F0.wireOp",EDGE,"E9.7.6.0"),sQuery(id+"F0.wireOp",EDGE,"E9.11.6.0"),sQuery(id+"F0.wireOp",EDGE,"E9.14.6.0"),sQuery(id+"F0.wireOp",EDGE,"E9.1.7.0"),sQuery(id+"F0.wireOp",EDGE,"E9.3.7.0"),sQuery(id+"F0.wireOp",EDGE,"E9.7.7.0"),sQuery(id+"F0.wireOp",EDGE,"E9.11.7.0"),sQuery(id+"F0.wireOp",EDGE,"E9.14.7.0"),sQuery(id+"F0.wireOp",EDGE,"E9.1.8.0"),sQuery(id+"F0.wireOp",EDGE,"E9.3.8.0"),sQuery(id+"F0.wireOp",EDGE,"E9.7.8.0"),sQuery(id+"F0.wireOp",EDGE,"E9.11.8.0"),sQuery(id+"F0.wireOp",EDGE,"E9.14.8.0"),sQuery(id+"F0.wireOp",EDGE,"E9.1.9.0"),sQuery(id+"F0.wireOp",EDGE,"E9.3.9.0"),sQuery(id+"F0.wireOp",EDGE,"E9.7.9.0"),sQuery(id+"F0.wireOp",EDGE,"E9.11.9.0"),sQuery(id+"F0.wireOp",EDGE,"E9.14.9.0"),sQuery(id+"F0.wireOp",EDGE,"E9.1.10.0"),sQuery(id+"F0.wireOp",EDGE,"E9.3.10.0"),sQuery(id+"F0.wireOp",EDGE,"E9.7.10.0"),sQuery(id+"F0.wireOp",EDGE,"E9.11.10.0"),sQuery(id+"F0.wireOp",EDGE,"E9.14.10.0"),sQuery(id+"F0.wireOp",EDGE,"E9.1.11.0"),sQuery(id+"F0.wireOp",EDGE,"E9.3.11.0"),sQuery(id+"F0.wireOp",EDGE,"E9.7.11.0"),sQuery(id+"F0.wireOp",EDGE,"E9.11.11.0"),sQuery(id+"F0.wireOp",EDGE,"E9.14.11.0"),sQuery(id+"F0.wireOp",EDGE,"E9.1.12.0"),sQuery(id+"F0.wireOp",EDGE,"E9.3.12.0"),sQuery(id+"F0.wireOp",EDGE,"E9.7.12.0"),sQuery(id+"F0.wireOp",EDGE,"E9.11.12.0"),sQuery(id+"F0.wireOp",EDGE,"E9.14.12.0"),sQuery(id+"F0.wireOp",EDGE,"E9.1.13.0"),sQuery(id+"F0.wireOp",EDGE,"E9.3.13.0"),sQuery(id+"F0.wireOp",EDGE,"E9.7.13.0"),sQuery(id+"F0.wireOp",EDGE,"E9.11.13.0"),sQuery(id+"F0.wireOp",EDGE,"E9.14.13.0"),sQuery(id+"F0.wireOp",EDGE,"E9.1.14.0"),sQuery(id+"F0.wireOp",EDGE,"E9.3.14.0"),sQuery(id+"F0.wireOp",EDGE,"E9.7.14.0"),sQuery(id+"F0.wireOp",EDGE,"E9.11.14.0"),sQuery(id+"F0.wireOp",EDGE,"E9.14.14.0"),sQuery(id+"F0.wireOp",EDGE,"E9.1.15.0"),sQuery(id+"F0.wireOp",EDGE,"E9.3.15.0"),sQuery(id+"F0.wireOp",EDGE,"E9.7.15.0"),sQuery(id+"F0.wireOp",EDGE,"E9.11.15.0"),sQuery(id+"F0.wireOp",EDGE,"E9.14.15.0"),sQuery(id+"F0.wireOp",EDGE,"E9.1.16.0"),sQuery(id+"F0.wireOp",EDGE,"E9.3.16.0"),sQuery(id+"F0.wireOp",EDGE,"E9.7.16.0"),sQuery(id+"F0.wireOp",EDGE,"E9.11.16.0"),sQuery(id+"F0.wireOp",EDGE,"E9.14.16.0"),sQuery(id+"F0.wireOp",EDGE,"E9.1.17.0"),sQuery(id+"F0.wireOp",EDGE,"E9.3.17.0"),sQuery(id+"F0.wireOp",EDGE,"E9.7.17.0"),sQuery(id+"F0.wireOp",EDGE,"E9.11.17.0"),sQuery(id+"F0.wireOp",EDGE,"E9.14.17.0"),sQuery(id+"F0.wireOp",EDGE,"E9.1.18.0"),sQuery(id+"F0.wireOp",EDGE,"E9.3.18.0"),sQuery(id+"F0.wireOp",EDGE,"E9.7.18.0"),sQuery(id+"F0.wireOp",EDGE,"E9.11.18.0"),sQuery(id+"F0.wireOp",EDGE,"E9.14.18.0"),sQuery(id+"F0.wireOp",EDGE,"E9.1.19.0"),sQuery(id+"F0.wireOp",EDGE,"E9.3.19.0"),sQuery(id+"F0.wireOp",EDGE,"E9.7.19.0"),sQuery(id+"F0.wireOp",EDGE,"E9.11.19.0"),sQuery(id+"F0.wireOp",EDGE,"E9.14.19.0"),sQuery(id+"F0.wireOp",EDGE,"E9.1.20.0"),sQuery(id+"F0.wireOp",EDGE,"E9.3.20.0"),sQuery(id+"F0.wireOp",EDGE,"E9.7.20.0"),sQuery(id+"F0.wireOp",EDGE,"E9.11.20.0"),sQuery(id+"F0.wireOp",EDGE,"E9.14.20.0"),sQuery(id+"F0.wireOp",EDGE,"E9.1.21.0"),sQuery(id+"F0.wireOp",EDGE,"E9.3.21.0"),sQuery(id+"F0.wireOp",EDGE,"E9.7.21.0"),sQuery(id+"F0.wireOp",EDGE,"E9.11.21.0"),sQuery(id+"F0.wireOp",EDGE,"E9.14.21.0"),sQuery(id+"F0.wireOp",EDGE,"E9.1.22.0"),sQuery(id+"F0.wireOp",EDGE,"E9.3.22.0"),sQuery(id+"F0.wireOp",EDGE,"E9.7.22.0"),sQuery(id+"F0.wireOp",EDGE,"E9.11.22.0"),sQuery(id+"F0.wireOp",EDGE,"E9.14.22.0"),sQuery(id+"F0.wireOp",EDGE,"E9.1.23.0"),sQuery(id+"F0.wireOp",EDGE,"E9.3.23.0"),sQuery(id+"F0.wireOp",EDGE,"E9.7.23.0"),sQuery(id+"F0.wireOp",EDGE,"E9.11.23.0"),sQuery(id+"F0.wireOp",EDGE,"E9.14.23.0"),sQuery(id+"F0.wireOp",EDGE,"E9.1.24.0"),sQuery(id+"F0.wireOp",EDGE,"E9.3.24.0"),sQuery(id+"F0.wireOp",EDGE,"E9.7.24.0"),sQuery(id+"F0.wireOp",EDGE,"E9.11.24.0"),sQuery(id+"F0.wireOp",EDGE,"E9.14.24.0"),sQuery(id+"F0.wireOp",EDGE,"E9.1.25.0"),sQuery(id+"F0.wireOp",EDGE,"E9.3.25.0"),sQuery(id+"F0.wireOp",EDGE,"E9.7.25.0"),sQuery(id+"F0.wireOp",EDGE,"E9.11.25.0"),sQuery(id+"F0.wireOp",EDGE,"E9.14.25.0"),sQuery(id+"F0.wireOp",EDGE,"E9.1.26.0"),sQuery(id+"F0.wireOp",EDGE,"E9.3.26.0"),sQuery(id+"F0.wireOp",EDGE,"E9.7.26.0"),sQuery(id+"F0.wireOp",EDGE,"E9.11.26.0"),sQuery(id+"F0.wireOp",EDGE,"E9.14.26.0"),sQuery(id+"F0.wireOp",EDGE,"E9.1.27.0"),sQuery(id+"F0.wireOp",EDGE,"E9.3.27.0"),sQuery(id+"F0.wireOp",EDGE,"E9.7.27.0"),sQuery(id+"F0.wireOp",EDGE,"E9.11.27.0"),sQuery(id+"F0.wireOp",EDGE,"E9.14.27.0"),sQuery(id+"F0.wireOp",EDGE,"E9.1.28.0"),sQuery(id+"F0.wireOp",EDGE,"E9.3.28.0"),sQuery(id+"F0.wireOp",EDGE,"E9.7.28.0"),sQuery(id+"F0.wireOp",EDGE,"E9.11.28.0"),sQuery(id+"F0.wireOp",EDGE,"E9.14.28.0"),sQuery(id+"F0.wireOp",EDGE,"E9.1.29.0"),sQuery(id+"F0.wireOp",EDGE,"E9.3.29.0"),sQuery(id+"F0.wireOp",EDGE,"E9.7.29.0"),sQuery(id+"F0.wireOp",EDGE,"E9.11.29.0"),sQuery(id+"F0.wireOp",EDGE,"E9.14.29.0"),sQuery(id+"F0.wireOp",EDGE,"E9.1.30.0"),sQuery(id+"F0.wireOp",EDGE,"E9.3.30.0"),sQuery(id+"F0.wireOp",EDGE,"E9.7.30.0"),sQuery(id+"F0.wireOp",EDGE,"E9.11.30.0"),sQuery(id+"F0.wireOp",EDGE,"E9.14.30.0"),sQuery(id+"F0.wireOp",EDGE,"E9.1.31.0"),sQuery(id+"F0.wireOp",EDGE,"E9.3.31.0"),sQuery(id+"F0.wireOp",EDGE,"E9.7.31.0"),sQuery(id+"F0.wireOp",EDGE,"E9.11.31.0"),sQuery(id+"F0.wireOp",EDGE,"E9.14.31.0"),sQuery(id+"F0.wireOp",EDGE,"E9.1.32.0"),sQuery(id+"F0.wireOp",EDGE,"E9.3.32.0"),sQuery(id+"F0.wireOp",EDGE,"E9.7.32.0"),sQuery(id+"F0.wireOp",EDGE,"E9.11.32.0"),sQuery(id+"F0.wireOp",EDGE,"E9.14.32.0"),sQuery(id+"F0.wireOp",EDGE,"E9.1.33.0"),sQuery(id+"F0.wireOp",EDGE,"E9.3.33.0"),sQuery(id+"F0.wireOp",EDGE,"E9.7.33.0"),sQuery(id+"F0.wireOp",EDGE,"E9.11.33.0"),sQuery(id+"F0.wireOp",EDGE,"E9.14.33.0"),sQuery(id+"F0.wireOp",EDGE,"E9.1.34.0"),sQuery(id+"F0.wireOp",EDGE,"E9.3.34.0"),sQuery(id+"F0.wireOp",EDGE,"E9.7.34.0"),sQuery(id+"F0.wireOp",EDGE,"E9.11.34.0"),sQuery(id+"F0.wireOp",EDGE,"E9.14.34.0"),sQuery(id+"F0.wireOp",EDGE,"E9.1.35.0"),sQuery(id+"F0.wireOp",EDGE,"E9.3.35.0"),sQuery(id+"F0.wireOp",EDGE,"E9.7.35.0"),sQuery(id+"F0.wireOp",EDGE,"E9.11.35.0"),sQuery(id+"F0.wireOp",EDGE,"E9.14.35.0"),sQuery(id+"F0.wireOp",EDGE,"E9.1.36.0"),sQuery(id+"F0.wireOp",EDGE,"E9.3.36.0"),sQuery(id+"F0.wireOp",EDGE,"E9.7.36.0"),sQuery(id+"F0.wireOp",EDGE,"E9.11.36.0"),sQuery(id+"F0.wireOp",EDGE,"E9.14.36.0"),sQuery(id+"F0.wireOp",EDGE,"E9.1.37.0"),sQuery(id+"F0.wireOp",EDGE,"E9.3.37.0"),sQuery(id+"F0.wireOp",EDGE,"E9.7.37.0"),sQuery(id+"F0.wireOp",EDGE,"E9.11.37.0"),sQuery(id+"F0.wireOp",EDGE,"E9.14.37.0"),sQuery(id+"F0.wireOp",EDGE,"E9.1.38.0"),sQuery(id+"F0.wireOp",EDGE,"E9.3.38.0"),sQuery(id+"F0.wireOp",EDGE,"E9.7.38.0"),sQuery(id+"F0.wireOp",EDGE,"E9.11.38.0"),sQuery(id+"F0.wireOp",EDGE,"E9.14.38.0"),sQuery(id+"F0.wireOp",EDGE,"E9.1.39.0"),sQuery(id+"F0.wireOp",EDGE,"E9.3.39.0"),sQuery(id+"F0.wireOp",EDGE,"E9.7.39.0"),sQuery(id+"F0.wireOp",EDGE,"E9.11.39.0"),sQuery(id+"F0.wireOp",EDGE,"E9.14.39.0"),sQuery(id+"F0.wireOp",EDGE,"E9.1.40.0"),sQuery(id+"F0.wireOp",EDGE,"E9.3.40.0"),sQuery(id+"F0.wireOp",EDGE,"E9.7.40.0"),sQuery(id+"F0.wireOp",EDGE,"E9.11.40.0"),sQuery(id+"F0.wireOp",EDGE,"E9.14.40.0"),sQuery(id+"F0.wireOp",EDGE,"E9.1.41.0"),sQuery(id+"F0.wireOp",EDGE,"E9.3.41.0"),sQuery(id+"F0.wireOp",EDGE,"E9.7.41.0"),sQuery(id+"F0.wireOp",EDGE,"E9.11.41.0"),sQuery(id+"F0.wireOp",EDGE,"E9.14.41.0"),sQuery(id+"F0.wireOp",EDGE,"E9.1.42.0"),sQuery(id+"F0.wireOp",EDGE,"E9.3.42.0"),sQuery(id+"F0.wireOp",EDGE,"E9.7.42.0"),sQuery(id+"F0.wireOp",EDGE,"E9.11.42.0"),sQuery(id+"F0.wireOp",EDGE,"E9.14.42.0"),sQuery(id+"F0.wireOp",EDGE,"E9.1.43.0"),sQuery(id+"F0.wireOp",EDGE,"E9.3.43.0"),sQuery(id+"F0.wireOp",EDGE,"E9.7.43.0"),sQuery(id+"F0.wireOp",EDGE,"E9.11.43.0"),sQuery(id+"F0.wireOp",EDGE,"E9.14.43.0"),sQuery(id+"F0.wireOp",EDGE,"E9.1.44.0"),sQuery(id+"F0.wireOp",EDGE,"E9.3.44.0"),sQuery(id+"F0.wireOp",EDGE,"E9.7.44.0"),sQuery(id+"F0.wireOp",EDGE,"E9.11.44.0"),sQuery(id+"F0.wireOp",EDGE,"E9.14.44.0"),sQuery(id+"F0.wireOp",EDGE,"E9.1.45.0"),sQuery(id+"F0.wireOp",EDGE,"E9.3.45.0"),sQuery(id+"F0.wireOp",EDGE,"E9.7.45.0"),sQuery(id+"F0.wireOp",EDGE,"E9.11.45.0"),sQuery(id+"F0.wireOp",EDGE,"E9.14.45.0"),sQuery(id+"F0.wireOp",EDGE,"E9.1.46.0"),sQuery(id+"F0.wireOp",EDGE,"E9.3.46.0"),sQuery(id+"F0.wireOp",EDGE,"E9.7.46.0"),sQuery(id+"F0.wireOp",EDGE,"E9.11.46.0"),sQuery(id+"F0.wireOp",EDGE,"E9.14.46.0"),sQuery(id+"F0.wireOp",EDGE,"E9.1.47.0"),sQuery(id+"F0.wireOp",EDGE,"E9.3.47.0"),sQuery(id+"F0.wireOp",EDGE,"E9.7.47.0"),sQuery(id+"F0.wireOp",EDGE,"E9.11.47.0"),sQuery(id+"F0.wireOp",EDGE,"E9.14.47.0"),sQuery(id+"F0.wireOp",EDGE,"E9.1.48.0"),sQuery(id+"F0.wireOp",EDGE,"E9.3.48.0"),sQuery(id+"F0.wireOp",EDGE,"E9.7.48.0"),sQuery(id+"F0.wireOp",EDGE,"E9.11.48.0"),sQuery(id+"F0.wireOp",EDGE,"E9.14.48.0"),sQuery(id+"F0.wireOp",EDGE,"E9.1.49.0"),sQuery(id+"F0.wireOp",EDGE,"E9.3.49.0"),sQuery(id+"F0.wireOp",EDGE,"E9.7.49.0"),sQuery(id+"F0.wireOp",EDGE,"E9.11.49.0"),sQuery(id+"F0.wireOp",EDGE,"E9.14.49.0"),sQuery(id+"F0.wireOp",EDGE,"E9.1.50.0"),sQuery(id+"F0.wireOp",EDGE,"E9.3.50.0"),sQuery(id+"F0.wireOp",EDGE,"E9.7.50.0"),sQuery(id+"F0.wireOp",EDGE,"E9.11.50.0"),sQuery(id+"F0.wireOp",EDGE,"E9.14.50.0"),sQuery(id+"F0.wireOp",EDGE,"E9.1.51.0"),sQuery(id+"F0.wireOp",EDGE,"E9.3.51.0"),sQuery(id+"F0.wireOp",EDGE,"E9.7.51.0"),sQuery(id+"F0.wireOp",EDGE,"E9.11.51.0"),sQuery(id+"F0.wireOp",EDGE,"E9.14.51.0"),sQuery(id+"F0.wireOp",EDGE,"E9.1.52.0"),sQuery(id+"F0.wireOp",EDGE,"E9.3.52.0"),sQuery(id+"F0.wireOp",EDGE,"E9.7.52.0"),sQuery(id+"F0.wireOp",EDGE,"E9.11.52.0"),sQuery(id+"F0.wireOp",EDGE,"E9.14.52.0"),sQuery(id+"F0.wireOp",EDGE,"E9.1.53.0"),sQuery(id+"F0.wireOp",EDGE,"E9.3.53.0"),sQuery(id+"F0.wireOp",EDGE,"E9.7.53.0"),sQuery(id+"F0.wireOp",EDGE,"E9.11.53.0"),sQuery(id+"F0.wireOp",EDGE,"E9.14.53.0"),sQuery(id+"F0.wireOp",EDGE,"E9.1.54.0"),sQuery(id+"F0.wireOp",EDGE,"E9.3.54.0"),sQuery(id+"F0.wireOp",EDGE,"E9.7.54.0"),sQuery(id+"F0.wireOp",EDGE,"E9.11.54.0"),sQuery(id+"F0.wireOp",EDGE,"E9.14.54.0"),sQuery(id+"F0.wireOp",EDGE,"E9.1.55.0"),sQuery(id+"F0.wireOp",EDGE,"E9.3.55.0"),sQuery(id+"F0.wireOp",EDGE,"E9.7.55.0"),sQuery(id+"F0.wireOp",EDGE,"E9.11.55.0"),sQuery(id+"F0.wireOp",EDGE,"E9.14.55.0"),sQuery(id+"F0.wireOp",EDGE,"E9.1.56.0"),sQuery(id+"F0.wireOp",EDGE,"E9.3.56.0"),sQuery(id+"F0.wireOp",EDGE,"E9.7.56.0"),sQuery(id+"F0.wireOp",EDGE,"E9.11.56.0"),sQuery(id+"F0.wireOp",EDGE,"E9.14.56.0"),sQuery(id+"F0.wireOp",EDGE,"E9.1.57.0"),sQuery(id+"F0.wireOp",EDGE,"E9.3.57.0"),sQuery(id+"F0.wireOp",EDGE,"E9.7.57.0"),sQuery(id+"F0.wireOp",EDGE,"E9.11.57.0"),sQuery(id+"F0.wireOp",EDGE,"E9.14.57.0"),sQuery(id+"F0.wireOp",EDGE,"E9.1.58.0"),sQuery(id+"F0.wireOp",EDGE,"E9.3.58.0"),sQuery(id+"F0.wireOp",EDGE,"E9.7.58.0"),sQuery(id+"F0.wireOp",EDGE,"E9.11.58.0"),sQuery(id+"F0.wireOp",EDGE,"E9.14.58.0"),sQuery(id+"F0.wireOp",EDGE,"E9.1.59.0"),sQuery(id+"F0.wireOp",EDGE,"E9.3.59.0"),sQuery(id+"F0.wireOp",EDGE,"E9.7.59.0"),sQuery(id+"F0.wireOp",EDGE,"E9.11.59.0"),sQuery(id+"F0.wireOp",EDGE,"E9.14.59.0"),sQuery(id+"F2.wireOp",EDGE,"E37.trimOffspring")])],"isStart":false})});
            var Q5;
            Q5=makeQuery(id+"F6.boolean.opBoolean","INTERSECT",EDGE,{"derivedFrom":[makeQuery(id+"F4.boolean.opBoolean","COPY",FACE,{"derivedFrom":makeQuery(id+"F4.opExtrude","CAP_FACE",FACE,{"disambiguationData":[OSD([sQuery(id+"F3.wireOp",EDGE,"E42"),sQuery(id+"F3.wireOp",EDGE,"E43")])],"isStart":false})}),makeQuery(id+"F6.opExtrude","SWEPT_FACE",FACE,{"disambiguationData":[OSD([sQuery(id+"F2.wireOp",EDGE,"E20.0")])]})]});
            var Q6;
            Q6=makeQuery(id+"F6.boolean.opBoolean","INTERSECT",EDGE,{"derivedFrom":[makeQuery(id+"F4.boolean.opBoolean","COPY",FACE,{"derivedFrom":makeQuery(id+"F4.opExtrude","CAP_FACE",FACE,{"disambiguationData":[OSD([sQuery(id+"F3.wireOp",EDGE,"E42"),sQuery(id+"F3.wireOp",EDGE,"E43")])],"isStart":false})}),makeQuery(id+"F6.opExtrude","SWEPT_FACE",FACE,{"disambiguationData":[OSD([sQuery(id+"F2.wireOp",EDGE,"E19")])]})]});
            var Q7;
            Q7=makeQuery(id+"F6.boolean.opBoolean","INTERSECT",EDGE,{"derivedFrom":[makeQuery(id+"F4.boolean.opBoolean","COPY",FACE,{"derivedFrom":makeQuery(id+"F4.opExtrude","CAP_FACE",FACE,{"disambiguationData":[OSD([sQuery(id+"F3.wireOp",EDGE,"E42"),sQuery(id+"F3.wireOp",EDGE,"E43")])],"isStart":false})}),makeQuery(id+"F6.opExtrude","SWEPT_FACE",FACE,{"disambiguationData":[OSD([sQuery(id+"F2.wireOp",EDGE,"E22.0")])]})]});
            var Q8;
            Q8=makeQuery(id+"F6.boolean.opBoolean","INTERSECT",EDGE,{"derivedFrom":[makeQuery(id+"F4.boolean.opBoolean","COPY",FACE,{"derivedFrom":makeQuery(id+"F4.opExtrude","CAP_FACE",FACE,{"disambiguationData":[OSD([sQuery(id+"F3.wireOp",EDGE,"E42"),sQuery(id+"F3.wireOp",EDGE,"E43")])],"isStart":false})}),makeQuery(id+"F6.opExtrude","SWEPT_FACE",FACE,{"disambiguationData":[OSD([sQuery(id+"F2.wireOp",EDGE,"E36.trimOffspring")])]})]});
            fillet(context, id + "F9", {"entities" : qUnion([Q0, Q1, Q2, Q3, Q4, Q5, Q6, Q7, Q8]), "radius" : 1 * mm, "tangentPropagation" : true, "allowEdgeOverflow" : false});
        }
        {
            var Q0;
            Q0=makeQuery(id+"F4.boolean.opBoolean","COPY",EDGE,{"derivedFrom":makeQuery(id+"F4.opExtrude","CAP_EDGE",EDGE,{"disambiguationData":[OSD([sQuery(id+"F3.wireOp",EDGE,"E43")])],"isStart":false})});
            var Q1;
            Q1=makeQuery(id+"F8.boolean.opBoolean","COPY",EDGE,{"derivedFrom":makeQuery(id+"F8.opExtrude","CAP_EDGE",EDGE,{"disambiguationData":[OSD([sQuery(id+"F7.wireOp",EDGE,"E47")])],"isStart":false})});
            var Q2;
            Q2=makeQuery(id+"F4.boolean.opBoolean","COPY",EDGE,{"derivedFrom":makeQuery(id+"F4.opExtrude","CAP_EDGE",EDGE,{"disambiguationData":[OSD([sQuery(id+"F3.wireOp",EDGE,"E42")])],"isStart":false})});
            var Q3;
            Q3=makeQuery(id+"F8.boolean.opBoolean","COPY",EDGE,{"derivedFrom":makeQuery(id+"F8.opExtrude","CAP_EDGE",EDGE,{"disambiguationData":[OSD([sQuery(id+"F7.wireOp",EDGE,"E44")])],"isStart":false})});
            fillet(context, id + "F10", {"entities" : qUnion([Q0, Q1, Q2, Q3]), "radius" : 1 * mm, "tangentPropagation" : true, "allowEdgeOverflow" : false});
        }
        {
            var Q0;
            Q0=makeQuery(id+"F9.opFillet","SPLIT",FACE,{"disambiguationData":[OD(0.0)],"derivedFrom":makeQuery(id+"F8.boolean.opBoolean","COPY",FACE,{"derivedFrom":makeQuery(id+"F8.opExtrude","CAP_FACE",FACE,{"disambiguationData":[OSD([sQuery(id+"F0.wireOp",EDGE,"E0"),sQuery(id+"F0.wireOp",EDGE,"E1"),sQuery(id+"F0.wireOp",EDGE,"E3"),sQuery(id+"F0.wireOp",EDGE,"E4"),sQuery(id+"F0.wireOp",EDGE,"E5"),sQuery(id+"F0.wireOp",EDGE,"E6.trimOffspring"),sQuery(id+"F0.wireOp",EDGE,"E7"),sQuery(id+"F0.wireOp",EDGE,"E8.1.0"),sQuery(id+"F0.wireOp",EDGE,"E8.1.1"),sQuery(id+"F0.wireOp",EDGE,"E8.1.2"),sQuery(id+"F0.wireOp",EDGE,"E8.1.3"),sQuery(id+"F0.wireOp",EDGE,"E8.1.4"),sQuery(id+"F0.wireOp",EDGE,"E8.2.0"),sQuery(id+"F0.wireOp",EDGE,"E8.2.1"),sQuery(id+"F0.wireOp",EDGE,"E8.2.2"),sQuery(id+"F0.wireOp",EDGE,"E8.2.3"),sQuery(id+"F0.wireOp",EDGE,"E8.2.4"),sQuery(id+"F0.wireOp",EDGE,"E9.1.3.0"),sQuery(id+"F0.wireOp",EDGE,"E9.3.3.0"),sQuery(id+"F0.wireOp",EDGE,"E9.7.3.0"),sQuery(id+"F0.wireOp",EDGE,"E9.11.3.0"),sQuery(id+"F0.wireOp",EDGE,"E9.14.3.0"),sQuery(id+"F0.wireOp",EDGE,"E9.1.4.0"),sQuery(id+"F0.wireOp",EDGE,"E9.3.4.0"),sQuery(id+"F0.wireOp",EDGE,"E9.7.4.0"),sQuery(id+"F0.wireOp",EDGE,"E9.11.4.0"),sQuery(id+"F0.wireOp",EDGE,"E9.14.4.0"),sQuery(id+"F0.wireOp",EDGE,"E9.1.5.0"),sQuery(id+"F0.wireOp",EDGE,"E9.3.5.0"),sQuery(id+"F0.wireOp",EDGE,"E9.7.5.0"),sQuery(id+"F0.wireOp",EDGE,"E9.11.5.0"),sQuery(id+"F0.wireOp",EDGE,"E9.14.5.0"),sQuery(id+"F0.wireOp",EDGE,"E9.1.6.0"),sQuery(id+"F0.wireOp",EDGE,"E9.3.6.0"),sQuery(id+"F0.wireOp",EDGE,"E9.7.6.0"),sQuery(id+"F0.wireOp",EDGE,"E9.11.6.0"),sQuery(id+"F0.wireOp",EDGE,"E9.14.6.0"),sQuery(id+"F0.wireOp",EDGE,"E9.1.7.0"),sQuery(id+"F0.wireOp",EDGE,"E9.3.7.0"),sQuery(id+"F0.wireOp",EDGE,"E9.7.7.0"),sQuery(id+"F0.wireOp",EDGE,"E9.11.7.0"),sQuery(id+"F0.wireOp",EDGE,"E9.14.7.0"),sQuery(id+"F0.wireOp",EDGE,"E9.1.8.0"),sQuery(id+"F0.wireOp",EDGE,"E9.3.8.0"),sQuery(id+"F0.wireOp",EDGE,"E9.7.8.0"),sQuery(id+"F0.wireOp",EDGE,"E9.11.8.0"),sQuery(id+"F0.wireOp",EDGE,"E9.14.8.0"),sQuery(id+"F0.wireOp",EDGE,"E9.1.9.0"),sQuery(id+"F0.wireOp",EDGE,"E9.3.9.0"),sQuery(id+"F0.wireOp",EDGE,"E9.7.9.0"),sQuery(id+"F0.wireOp",EDGE,"E9.11.9.0"),sQuery(id+"F0.wireOp",EDGE,"E9.14.9.0"),sQuery(id+"F0.wireOp",EDGE,"E9.1.10.0"),sQuery(id+"F0.wireOp",EDGE,"E9.3.10.0"),sQuery(id+"F0.wireOp",EDGE,"E9.7.10.0"),sQuery(id+"F0.wireOp",EDGE,"E9.11.10.0"),sQuery(id+"F0.wireOp",EDGE,"E9.14.10.0"),sQuery(id+"F0.wireOp",EDGE,"E9.1.11.0"),sQuery(id+"F0.wireOp",EDGE,"E9.3.11.0"),sQuery(id+"F0.wireOp",EDGE,"E9.7.11.0"),sQuery(id+"F0.wireOp",EDGE,"E9.11.11.0"),sQuery(id+"F0.wireOp",EDGE,"E9.14.11.0"),sQuery(id+"F0.wireOp",EDGE,"E9.1.12.0"),sQuery(id+"F0.wireOp",EDGE,"E9.3.12.0"),sQuery(id+"F0.wireOp",EDGE,"E9.7.12.0"),sQuery(id+"F0.wireOp",EDGE,"E9.11.12.0"),sQuery(id+"F0.wireOp",EDGE,"E9.14.12.0"),sQuery(id+"F0.wireOp",EDGE,"E9.1.13.0"),sQuery(id+"F0.wireOp",EDGE,"E9.3.13.0"),sQuery(id+"F0.wireOp",EDGE,"E9.7.13.0"),sQuery(id+"F0.wireOp",EDGE,"E9.11.13.0"),sQuery(id+"F0.wireOp",EDGE,"E9.14.13.0"),sQuery(id+"F0.wireOp",EDGE,"E9.1.14.0"),sQuery(id+"F0.wireOp",EDGE,"E9.3.14.0"),sQuery(id+"F0.wireOp",EDGE,"E9.7.14.0"),sQuery(id+"F0.wireOp",EDGE,"E9.11.14.0"),sQuery(id+"F0.wireOp",EDGE,"E9.14.14.0"),sQuery(id+"F0.wireOp",EDGE,"E9.1.15.0"),sQuery(id+"F0.wireOp",EDGE,"E9.3.15.0"),sQuery(id+"F0.wireOp",EDGE,"E9.7.15.0"),sQuery(id+"F0.wireOp",EDGE,"E9.11.15.0"),sQuery(id+"F0.wireOp",EDGE,"E9.14.15.0"),sQuery(id+"F0.wireOp",EDGE,"E9.1.16.0"),sQuery(id+"F0.wireOp",EDGE,"E9.3.16.0"),sQuery(id+"F0.wireOp",EDGE,"E9.7.16.0"),sQuery(id+"F0.wireOp",EDGE,"E9.11.16.0"),sQuery(id+"F0.wireOp",EDGE,"E9.14.16.0"),sQuery(id+"F0.wireOp",EDGE,"E9.1.17.0"),sQuery(id+"F0.wireOp",EDGE,"E9.3.17.0"),sQuery(id+"F0.wireOp",EDGE,"E9.7.17.0"),sQuery(id+"F0.wireOp",EDGE,"E9.11.17.0"),sQuery(id+"F0.wireOp",EDGE,"E9.14.17.0"),sQuery(id+"F0.wireOp",EDGE,"E9.1.18.0"),sQuery(id+"F0.wireOp",EDGE,"E9.3.18.0"),sQuery(id+"F0.wireOp",EDGE,"E9.7.18.0"),sQuery(id+"F0.wireOp",EDGE,"E9.11.18.0"),sQuery(id+"F0.wireOp",EDGE,"E9.14.18.0"),sQuery(id+"F0.wireOp",EDGE,"E9.1.19.0"),sQuery(id+"F0.wireOp",EDGE,"E9.3.19.0"),sQuery(id+"F0.wireOp",EDGE,"E9.7.19.0"),sQuery(id+"F0.wireOp",EDGE,"E9.11.19.0"),sQuery(id+"F0.wireOp",EDGE,"E9.14.19.0"),sQuery(id+"F0.wireOp",EDGE,"E9.1.20.0"),sQuery(id+"F0.wireOp",EDGE,"E9.3.20.0"),sQuery(id+"F0.wireOp",EDGE,"E9.7.20.0"),sQuery(id+"F0.wireOp",EDGE,"E9.11.20.0"),sQuery(id+"F0.wireOp",EDGE,"E9.14.20.0"),sQuery(id+"F0.wireOp",EDGE,"E9.1.21.0"),sQuery(id+"F0.wireOp",EDGE,"E9.3.21.0"),sQuery(id+"F0.wireOp",EDGE,"E9.7.21.0"),sQuery(id+"F0.wireOp",EDGE,"E9.11.21.0"),sQuery(id+"F0.wireOp",EDGE,"E9.14.21.0"),sQuery(id+"F0.wireOp",EDGE,"E9.1.22.0"),sQuery(id+"F0.wireOp",EDGE,"E9.3.22.0"),sQuery(id+"F0.wireOp",EDGE,"E9.7.22.0"),sQuery(id+"F0.wireOp",EDGE,"E9.11.22.0"),sQuery(id+"F0.wireOp",EDGE,"E9.14.22.0"),sQuery(id+"F0.wireOp",EDGE,"E9.1.23.0"),sQuery(id+"F0.wireOp",EDGE,"E9.3.23.0"),sQuery(id+"F0.wireOp",EDGE,"E9.7.23.0"),sQuery(id+"F0.wireOp",EDGE,"E9.11.23.0"),sQuery(id+"F0.wireOp",EDGE,"E9.14.23.0"),sQuery(id+"F0.wireOp",EDGE,"E9.1.24.0"),sQuery(id+"F0.wireOp",EDGE,"E9.3.24.0"),sQuery(id+"F0.wireOp",EDGE,"E9.7.24.0"),sQuery(id+"F0.wireOp",EDGE,"E9.11.24.0"),sQuery(id+"F0.wireOp",EDGE,"E9.14.24.0"),sQuery(id+"F0.wireOp",EDGE,"E9.1.25.0"),sQuery(id+"F0.wireOp",EDGE,"E9.3.25.0"),sQuery(id+"F0.wireOp",EDGE,"E9.7.25.0"),sQuery(id+"F0.wireOp",EDGE,"E9.11.25.0"),sQuery(id+"F0.wireOp",EDGE,"E9.14.25.0"),sQuery(id+"F0.wireOp",EDGE,"E9.1.26.0"),sQuery(id+"F0.wireOp",EDGE,"E9.3.26.0"),sQuery(id+"F0.wireOp",EDGE,"E9.7.26.0"),sQuery(id+"F0.wireOp",EDGE,"E9.11.26.0"),sQuery(id+"F0.wireOp",EDGE,"E9.14.26.0"),sQuery(id+"F0.wireOp",EDGE,"E9.1.27.0"),sQuery(id+"F0.wireOp",EDGE,"E9.3.27.0"),sQuery(id+"F0.wireOp",EDGE,"E9.7.27.0"),sQuery(id+"F0.wireOp",EDGE,"E9.11.27.0"),sQuery(id+"F0.wireOp",EDGE,"E9.14.27.0"),sQuery(id+"F0.wireOp",EDGE,"E9.1.28.0"),sQuery(id+"F0.wireOp",EDGE,"E9.3.28.0"),sQuery(id+"F0.wireOp",EDGE,"E9.7.28.0"),sQuery(id+"F0.wireOp",EDGE,"E9.11.28.0"),sQuery(id+"F0.wireOp",EDGE,"E9.14.28.0"),sQuery(id+"F0.wireOp",EDGE,"E9.1.29.0"),sQuery(id+"F0.wireOp",EDGE,"E9.3.29.0"),sQuery(id+"F0.wireOp",EDGE,"E9.7.29.0"),sQuery(id+"F0.wireOp",EDGE,"E9.11.29.0"),sQuery(id+"F0.wireOp",EDGE,"E9.14.29.0"),sQuery(id+"F0.wireOp",EDGE,"E9.1.30.0"),sQuery(id+"F0.wireOp",EDGE,"E9.3.30.0"),sQuery(id+"F0.wireOp",EDGE,"E9.7.30.0"),sQuery(id+"F0.wireOp",EDGE,"E9.11.30.0"),sQuery(id+"F0.wireOp",EDGE,"E9.14.30.0"),sQuery(id+"F0.wireOp",EDGE,"E9.1.31.0"),sQuery(id+"F0.wireOp",EDGE,"E9.3.31.0"),sQuery(id+"F0.wireOp",EDGE,"E9.7.31.0"),sQuery(id+"F0.wireOp",EDGE,"E9.11.31.0"),sQuery(id+"F0.wireOp",EDGE,"E9.14.31.0"),sQuery(id+"F0.wireOp",EDGE,"E9.1.32.0"),sQuery(id+"F0.wireOp",EDGE,"E9.3.32.0"),sQuery(id+"F0.wireOp",EDGE,"E9.7.32.0"),sQuery(id+"F0.wireOp",EDGE,"E9.11.32.0"),sQuery(id+"F0.wireOp",EDGE,"E9.14.32.0"),sQuery(id+"F0.wireOp",EDGE,"E9.1.33.0"),sQuery(id+"F0.wireOp",EDGE,"E9.3.33.0"),sQuery(id+"F0.wireOp",EDGE,"E9.7.33.0"),sQuery(id+"F0.wireOp",EDGE,"E9.11.33.0"),sQuery(id+"F0.wireOp",EDGE,"E9.14.33.0"),sQuery(id+"F0.wireOp",EDGE,"E9.1.34.0"),sQuery(id+"F0.wireOp",EDGE,"E9.3.34.0"),sQuery(id+"F0.wireOp",EDGE,"E9.7.34.0"),sQuery(id+"F0.wireOp",EDGE,"E9.11.34.0"),sQuery(id+"F0.wireOp",EDGE,"E9.14.34.0"),sQuery(id+"F0.wireOp",EDGE,"E9.1.35.0"),sQuery(id+"F0.wireOp",EDGE,"E9.3.35.0"),sQuery(id+"F0.wireOp",EDGE,"E9.7.35.0"),sQuery(id+"F0.wireOp",EDGE,"E9.11.35.0"),sQuery(id+"F0.wireOp",EDGE,"E9.14.35.0"),sQuery(id+"F0.wireOp",EDGE,"E9.1.36.0"),sQuery(id+"F0.wireOp",EDGE,"E9.3.36.0"),sQuery(id+"F0.wireOp",EDGE,"E9.7.36.0"),sQuery(id+"F0.wireOp",EDGE,"E9.11.36.0"),sQuery(id+"F0.wireOp",EDGE,"E9.14.36.0"),sQuery(id+"F0.wireOp",EDGE,"E9.1.37.0"),sQuery(id+"F0.wireOp",EDGE,"E9.3.37.0"),sQuery(id+"F0.wireOp",EDGE,"E9.7.37.0"),sQuery(id+"F0.wireOp",EDGE,"E9.11.37.0"),sQuery(id+"F0.wireOp",EDGE,"E9.14.37.0"),sQuery(id+"F0.wireOp",EDGE,"E9.1.38.0"),sQuery(id+"F0.wireOp",EDGE,"E9.3.38.0"),sQuery(id+"F0.wireOp",EDGE,"E9.7.38.0"),sQuery(id+"F0.wireOp",EDGE,"E9.11.38.0"),sQuery(id+"F0.wireOp",EDGE,"E9.14.38.0"),sQuery(id+"F0.wireOp",EDGE,"E9.1.39.0"),sQuery(id+"F0.wireOp",EDGE,"E9.3.39.0"),sQuery(id+"F0.wireOp",EDGE,"E9.7.39.0"),sQuery(id+"F0.wireOp",EDGE,"E9.11.39.0"),sQuery(id+"F0.wireOp",EDGE,"E9.14.39.0"),sQuery(id+"F0.wireOp",EDGE,"E9.1.40.0"),sQuery(id+"F0.wireOp",EDGE,"E9.3.40.0"),sQuery(id+"F0.wireOp",EDGE,"E9.7.40.0"),sQuery(id+"F0.wireOp",EDGE,"E9.11.40.0"),sQuery(id+"F0.wireOp",EDGE,"E9.14.40.0"),sQuery(id+"F0.wireOp",EDGE,"E9.1.41.0"),sQuery(id+"F0.wireOp",EDGE,"E9.3.41.0"),sQuery(id+"F0.wireOp",EDGE,"E9.7.41.0"),sQuery(id+"F0.wireOp",EDGE,"E9.11.41.0"),sQuery(id+"F0.wireOp",EDGE,"E9.14.41.0"),sQuery(id+"F0.wireOp",EDGE,"E9.1.42.0"),sQuery(id+"F0.wireOp",EDGE,"E9.3.42.0"),sQuery(id+"F0.wireOp",EDGE,"E9.7.42.0"),sQuery(id+"F0.wireOp",EDGE,"E9.11.42.0"),sQuery(id+"F0.wireOp",EDGE,"E9.14.42.0"),sQuery(id+"F0.wireOp",EDGE,"E9.1.43.0"),sQuery(id+"F0.wireOp",EDGE,"E9.3.43.0"),sQuery(id+"F0.wireOp",EDGE,"E9.7.43.0"),sQuery(id+"F0.wireOp",EDGE,"E9.11.43.0"),sQuery(id+"F0.wireOp",EDGE,"E9.14.43.0"),sQuery(id+"F0.wireOp",EDGE,"E9.1.44.0"),sQuery(id+"F0.wireOp",EDGE,"E9.3.44.0"),sQuery(id+"F0.wireOp",EDGE,"E9.7.44.0"),sQuery(id+"F0.wireOp",EDGE,"E9.11.44.0"),sQuery(id+"F0.wireOp",EDGE,"E9.14.44.0"),sQuery(id+"F0.wireOp",EDGE,"E9.1.45.0"),sQuery(id+"F0.wireOp",EDGE,"E9.3.45.0"),sQuery(id+"F0.wireOp",EDGE,"E9.7.45.0"),sQuery(id+"F0.wireOp",EDGE,"E9.11.45.0"),sQuery(id+"F0.wireOp",EDGE,"E9.14.45.0"),sQuery(id+"F0.wireOp",EDGE,"E9.1.46.0"),sQuery(id+"F0.wireOp",EDGE,"E9.3.46.0"),sQuery(id+"F0.wireOp",EDGE,"E9.7.46.0"),sQuery(id+"F0.wireOp",EDGE,"E9.11.46.0"),sQuery(id+"F0.wireOp",EDGE,"E9.14.46.0"),sQuery(id+"F0.wireOp",EDGE,"E9.1.47.0"),sQuery(id+"F0.wireOp",EDGE,"E9.3.47.0"),sQuery(id+"F0.wireOp",EDGE,"E9.7.47.0"),sQuery(id+"F0.wireOp",EDGE,"E9.11.47.0"),sQuery(id+"F0.wireOp",EDGE,"E9.14.47.0"),sQuery(id+"F0.wireOp",EDGE,"E9.1.48.0"),sQuery(id+"F0.wireOp",EDGE,"E9.3.48.0"),sQuery(id+"F0.wireOp",EDGE,"E9.7.48.0"),sQuery(id+"F0.wireOp",EDGE,"E9.11.48.0"),sQuery(id+"F0.wireOp",EDGE,"E9.14.48.0"),sQuery(id+"F0.wireOp",EDGE,"E9.1.49.0"),sQuery(id+"F0.wireOp",EDGE,"E9.3.49.0"),sQuery(id+"F0.wireOp",EDGE,"E9.7.49.0"),sQuery(id+"F0.wireOp",EDGE,"E9.11.49.0"),sQuery(id+"F0.wireOp",EDGE,"E9.14.49.0"),sQuery(id+"F0.wireOp",EDGE,"E9.1.50.0"),sQuery(id+"F0.wireOp",EDGE,"E9.3.50.0"),sQuery(id+"F0.wireOp",EDGE,"E9.7.50.0"),sQuery(id+"F0.wireOp",EDGE,"E9.11.50.0"),sQuery(id+"F0.wireOp",EDGE,"E9.14.50.0"),sQuery(id+"F0.wireOp",EDGE,"E9.1.51.0"),sQuery(id+"F0.wireOp",EDGE,"E9.3.51.0"),sQuery(id+"F0.wireOp",EDGE,"E9.7.51.0"),sQuery(id+"F0.wireOp",EDGE,"E9.11.51.0"),sQuery(id+"F0.wireOp",EDGE,"E9.14.51.0"),sQuery(id+"F0.wireOp",EDGE,"E9.1.52.0"),sQuery(id+"F0.wireOp",EDGE,"E9.3.52.0"),sQuery(id+"F0.wireOp",EDGE,"E9.7.52.0"),sQuery(id+"F0.wireOp",EDGE,"E9.11.52.0"),sQuery(id+"F0.wireOp",EDGE,"E9.14.52.0"),sQuery(id+"F0.wireOp",EDGE,"E9.1.53.0"),sQuery(id+"F0.wireOp",EDGE,"E9.3.53.0"),sQuery(id+"F0.wireOp",EDGE,"E9.7.53.0"),sQuery(id+"F0.wireOp",EDGE,"E9.11.53.0"),sQuery(id+"F0.wireOp",EDGE,"E9.14.53.0"),sQuery(id+"F0.wireOp",EDGE,"E9.1.54.0"),sQuery(id+"F0.wireOp",EDGE,"E9.3.54.0"),sQuery(id+"F0.wireOp",EDGE,"E9.7.54.0"),sQuery(id+"F0.wireOp",EDGE,"E9.11.54.0"),sQuery(id+"F0.wireOp",EDGE,"E9.14.54.0"),sQuery(id+"F0.wireOp",EDGE,"E9.1.55.0"),sQuery(id+"F0.wireOp",EDGE,"E9.3.55.0"),sQuery(id+"F0.wireOp",EDGE,"E9.7.55.0"),sQuery(id+"F0.wireOp",EDGE,"E9.11.55.0"),sQuery(id+"F0.wireOp",EDGE,"E9.14.55.0"),sQuery(id+"F0.wireOp",EDGE,"E9.1.56.0"),sQuery(id+"F0.wireOp",EDGE,"E9.3.56.0"),sQuery(id+"F0.wireOp",EDGE,"E9.7.56.0"),sQuery(id+"F0.wireOp",EDGE,"E9.11.56.0"),sQuery(id+"F0.wireOp",EDGE,"E9.14.56.0"),sQuery(id+"F0.wireOp",EDGE,"E9.1.57.0"),sQuery(id+"F0.wireOp",EDGE,"E9.3.57.0"),sQuery(id+"F0.wireOp",EDGE,"E9.7.57.0"),sQuery(id+"F0.wireOp",EDGE,"E9.11.57.0"),sQuery(id+"F0.wireOp",EDGE,"E9.14.57.0"),sQuery(id+"F0.wireOp",EDGE,"E9.1.58.0"),sQuery(id+"F0.wireOp",EDGE,"E9.3.58.0"),sQuery(id+"F0.wireOp",EDGE,"E9.7.58.0"),sQuery(id+"F0.wireOp",EDGE,"E9.11.58.0"),sQuery(id+"F0.wireOp",EDGE,"E9.14.58.0"),sQuery(id+"F0.wireOp",EDGE,"E9.1.59.0"),sQuery(id+"F0.wireOp",EDGE,"E9.3.59.0"),sQuery(id+"F0.wireOp",EDGE,"E9.7.59.0"),sQuery(id+"F0.wireOp",EDGE,"E9.11.59.0"),sQuery(id+"F0.wireOp",EDGE,"E9.14.59.0"),sQuery(id+"F2.wireOp",EDGE,"E15"),sQuery(id+"F2.wireOp",EDGE,"E19"),sQuery(id+"F2.wireOp",EDGE,"E20.0"),sQuery(id+"F2.wireOp",EDGE,"E21"),sQuery(id+"F2.wireOp",EDGE,"E22.0"),sQuery(id+"F2.wireOp",EDGE,"E23"),sQuery(id+"F2.wireOp",EDGE,"E24"),sQuery(id+"F2.wireOp",EDGE,"E25"),sQuery(id+"F2.wireOp",EDGE,"E26"),sQuery(id+"F2.wireOp",EDGE,"E27"),sQuery(id+"F2.wireOp",EDGE,"E28"),sQuery(id+"F2.wireOp",EDGE,"E29"),sQuery(id+"F2.wireOp",EDGE,"E30"),sQuery(id+"F2.wireOp",EDGE,"E31"),sQuery(id+"F2.wireOp",EDGE,"E32"),sQuery(id+"F2.wireOp",EDGE,"E33"),sQuery(id+"F2.wireOp",EDGE,"E34"),sQuery(id+"F2.wireOp",EDGE,"E35.trimOffspring"),sQuery(id+"F2.wireOp",EDGE,"E36.trimOffspring"),sQuery(id+"F2.wireOp",EDGE,"E37.trimOffspring"),sQuery(id+"F2.wireOp",EDGE,"E38.trimOffspring"),sQuery(id+"F7.wireOp",EDGE,"E44"),sQuery(id+"F7.wireOp",EDGE,"E47")])],"isStart":false})})});
            var sketch = newSketch(context, id + "F11", { "sketchPlane" : qUnion([Q0])});
            skCircle(sketch, "E48", {"center": v(-53, 0) * mm, "radius": 3 * mm});
            skSolve(sketch);
        }
        {
            var Q0;
            Q0 = qSketchRegion(id + "F11", true);
            extrude(context, id + "F12", {"entities" : qUnion([Q0]), "operationType" : NewBodyOperationType.REMOVE, "endBound" : BoundingType.THROUGH_ALL, "oppositeDirection" : true, "depth" : 25 * mm, "offsetDistance" : 25 * mm});
        }
    });
